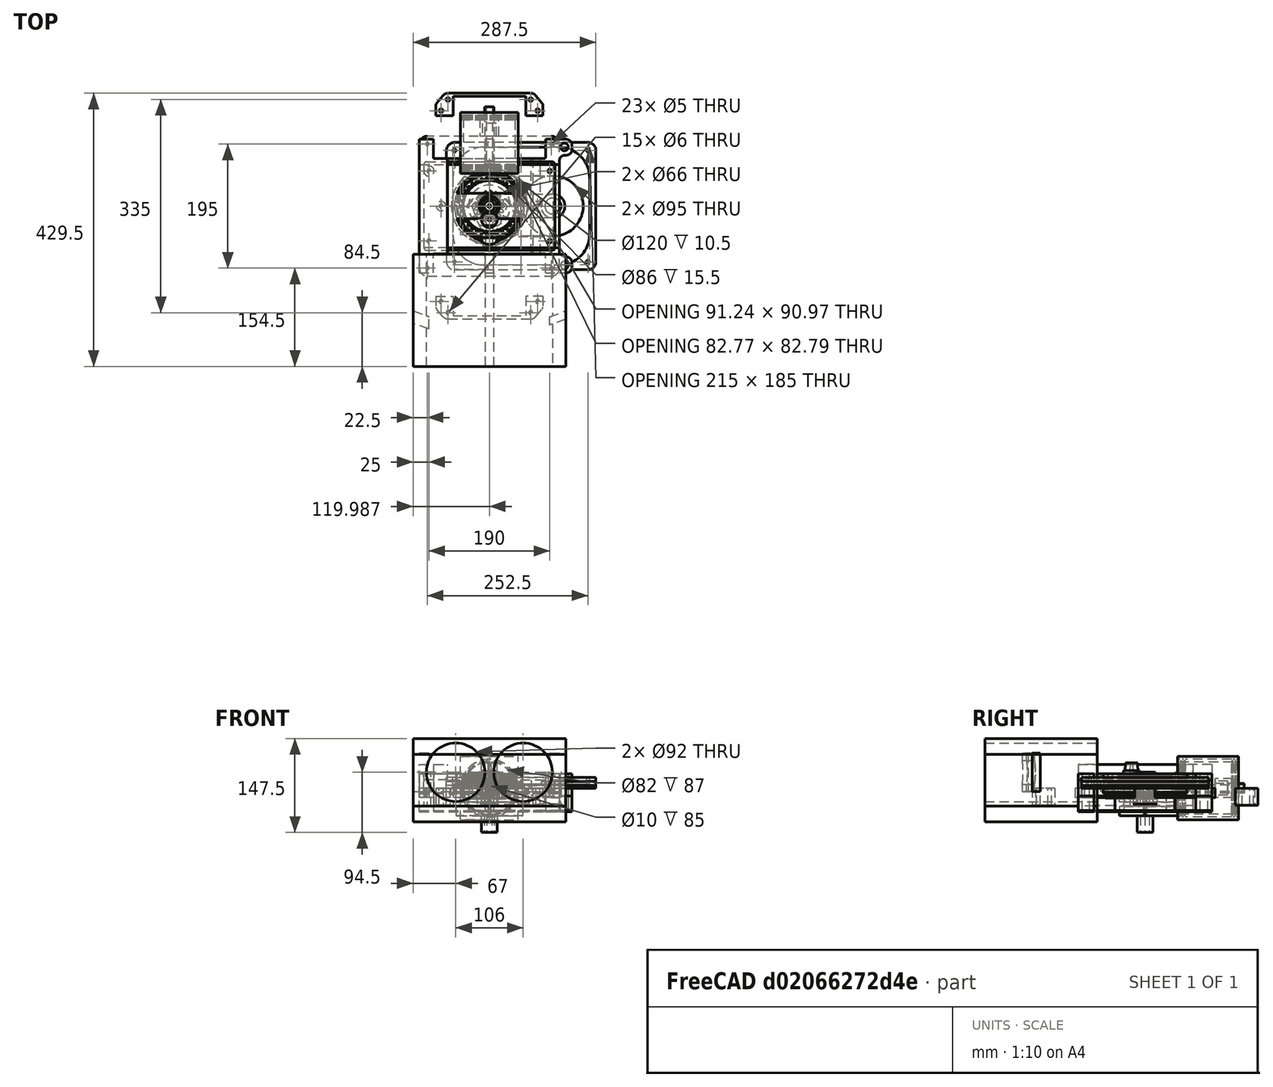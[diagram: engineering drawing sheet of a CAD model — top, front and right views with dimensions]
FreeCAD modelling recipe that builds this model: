
FCSTD DOCUMENT  (FreeCAD 1.0R38641 +678 (Git))
Label: assm4_X_at_Tusi_stirling
License: All rights reserved
objects: Sketcher::SketchObject×46, PartDesign::Body×30, PartDesign::Pad×28, PartDesign::CoordinateSystem×26, App::Link×23, PartDesign::Pocket×19, Mesh::Feature×12, PartDesign::FeatureBase×8, PartDesign::SubtractiveCylinder×5, App::DocumentObjectGroup×4, PartDesign::AdditiveCylinder×4, PartDesign::Boolean×2, Part::Extrusion×2, Part::FeaturePython×2, PartDesign::Hole×2, PartDesign::Fillet×2, App::FeaturePython×1, Spreadsheet::Sheet×1, Part::MultiFuse×1, PartDesign::Chamfer×1, +3 more types
note: 359 computed .brp shape members not serialized (recipe doc carries the construction recipe); baked Part::Feature solids carry a one-line shape summary decoded from their .brp

FEATURE [PartDesign::CoordinateSystem] LCS_Origin
  AttacherType = Attacher::AttachEngine3D
  AttachmentSupport = -> [X_Axis]
  MapMode = 2
FEATURE [App::DocumentObjectGroup] Constraints
FEATURE [App::FeaturePython] Variables  # WARN: FeaturePython — macro-defined, semantics opaque (R4)
  Crank_Angle = 0
  Type = App::PropertyContainer
FEATURE [App::DocumentObjectGroup] Configurations
FEATURE [Sketcher::SketchObject] Sketch002
  ArcFitTolerance = 0
  AttachmentSupport = -> [XY_Plane006]
  FullyConstrained = true
  MakeInternals = false
  MapMode = 5
  expr: Constraints[0] = <<Dim_table>>.crank_dia1
  expr: Constraints[20] = <<Dim_table>>.hex_size
  sketch-geometry (8):
    g0: Circle CenterX=0 CenterY=0 CenterZ=0 NormalX=0 NormalY=0 NormalZ=1 AngleXU=0 Radius=12.5
    g1: LineSegment StartX=4.04145 StartY=7 StartZ=0 EndX=-4.04145 EndY=7 EndZ=0
    g2: LineSegment StartX=-4.04145 StartY=7 StartZ=0 EndX=-8.0829 EndY=0 EndZ=0
    g3: LineSegment StartX=-8.0829 StartY=0 StartZ=0 EndX=-4.04145 EndY=-7 EndZ=0
    g4: LineSegment StartX=-4.04145 StartY=-7 StartZ=0 EndX=4.04145 EndY=-7 EndZ=0
    g5: LineSegment StartX=4.04145 StartY=-7 StartZ=0 EndX=8.0829 EndY=-9e-16 EndZ=0
    g6: LineSegment StartX=8.0829 StartY=-9e-16 StartZ=0 EndX=4.04145 EndY=7 EndZ=0
    g7: Circle [constr] CenterX=0 CenterY=0 CenterZ=0 NormalX=0 NormalY=0 NormalZ=1 AngleXU=0 Radius=8.0829
  constraints (18):
    c: Diameter(g0) = 25
    c: Coincident(g1,g2)
    c: Coincident(g2,g3)
    c: Coincident(g3,g4)
    c: Coincident(g4,g5)
    c: Coincident(g5,g6)
    c: Coincident(g6,g1)
    c: Equal(g1, g2-g6) x5
    c: PointOnObject(g1,g7)
    c: PointOnObject(g2,g7)
    c: PointOnObject(g3,g7)
    c: PointOnObject(g4,g7)
    c: PointOnObject(g5,g7)
    c: PointOnObject(g6,g7)
    c: Coincident(g7,g0)
    c: Horizontal(g1)
    c: DistanceY(g3,g1) = 14
    c: Coincident(g0,g-1)
FEATURE [PartDesign::Pad] Pad005
  Direction = (0,0,1)
  Length = 26
  Length2 = 10
  Profile = -> Sketch002
  ReferenceAxis = -> Sketch002 [N_Axis]
  Reversed = true
  Suppressed = false
  Type = 0
FEATURE [PartDesign::Body] Body005  label="Шейка коренная"
  AllowCompound = false
  Group = -> [Sketch002,Pad005]
  Origin = -> Origin006
  Placement = pos=(0,0,47) rot=(0,0,1;0rad)
  Tip = -> Pad005
FEATURE [PartDesign::FeatureBase] Clone004
  BaseFeature = -> Body005
  Suppressed = false
FEATURE [PartDesign::Body] Body054
  AllowCompound = false
  Group = -> [Clone004]
  Origin = -> Origin055
  Placement = pos=(0,0,-43.5) rot=(0,0,1;0rad)
  Tip = -> Clone004
FEATURE [Sketcher::SketchObject] Sketch003
  ArcFitTolerance = 0
  AttachmentSupport = -> [XY_Plane005]
  FullyConstrained = true
  MakeInternals = false
  MapMode = 5
  expr: Constraints[17] = <<Dim_table>>.fillet_r
  expr: Constraints[18] = <<Dim_table>>.fillet_r
  expr: Constraints[21] = <<Dim_table>>.inter_shaft_len - <<Dim_table>>.zazor
  expr: Constraints[23] = <<Dim_table>>.axle_hole_dia
  expr: Constraints[25] = 70
  expr: Constraints[26] = <<Dim_table>>.crank_dia2 * 1.5
  expr: Constraints[27] = <<Dim_table>>.crank_len
  sketch-geometry (14):
    g0: ArcOfCircle CenterX=0 CenterY=0 CenterZ=0 NormalX=0 NormalY=0 NormalZ=1 AngleXU=0 Radius=52.5 StartAngle=0.0396143 EndAngle=3.10198
    g1: ArcOfCircle CenterX=-1.2e-15 CenterY=-21.25 CenterZ=0 NormalX=0 NormalY=0 NormalZ=1 AngleXU=0 Radius=18.75 StartAngle=3.49066 EndAngle=5.93412
    g2: LineSegment [constr] StartX=-17.6192 StartY=-27.6629 StartZ=0 EndX=17.6192 EndY=-27.6629 EndZ=0
    g3: LineSegment StartX=-50.4604 StartY=0 StartZ=0 EndX=-29.0881 EndY=0 EndZ=0
    g4: LineSegment StartX=-27.2087 StartY=-1.31596 StartZ=0 EndX=-17.6192 EndY=-27.6629 EndZ=0
    g5: LineSegment StartX=17.6192 StartY=-27.6629 StartZ=0 EndX=27.2087 EndY=-1.31596 EndZ=0
    g6: LineSegment StartX=29.0881 StartY=-7e-16 StartZ=0 EndX=50.4604 EndY=-7e-16 EndZ=0
    g7: ArcOfCircle CenterX=-29.0881 CenterY=-2 CenterZ=0 NormalX=0 NormalY=0 NormalZ=1 AngleXU=0 Radius=2 StartAngle=0.349066 EndAngle=1.5708
    g8: ArcOfCircle CenterX=29.0881 CenterY=-2 CenterZ=0 NormalX=0 NormalY=0 NormalZ=1 AngleXU=0 Radius=2 StartAngle=1.5708 EndAngle=2.79253
    g9: ArcOfCircle CenterX=50.4604 CenterY=2 CenterZ=0 NormalX=0 NormalY=0 NormalZ=1 AngleXU=0 Radius=2 StartAngle=4.71239 EndAngle=6.3228
    g10: ArcOfCircle CenterX=-50.4604 CenterY=2 CenterZ=0 NormalX=0 NormalY=0 NormalZ=1 AngleXU=0 Radius=2 StartAngle=3.10198 EndAngle=4.71239
    g11: Circle [constr] CenterX=0 CenterY=0 CenterZ=0 NormalX=0 NormalY=0 NormalZ=1 AngleXU=0 Radius=49.75
    g12: Circle CenterX=0 CenterY=0 CenterZ=0 NormalX=0 NormalY=0 NormalZ=1 AngleXU=0 Radius=2.5
    g13: Circle [constr] CenterX=-1.2e-15 CenterY=-21.25 CenterZ=0 NormalX=0 NormalY=0 NormalZ=1 AngleXU=0 Radius=2.5
  constraints (31):
    c: Coincident(g2,g1)
    c: Coincident(g2,g1)
    c: Horizontal(g2)
    c: Horizontal(g3)
    c: Horizontal(g6)
    c: Tangent(g4,g1) = -1.5708
    c: Tangent(g5,g1) = -1.5708
    c: Tangent(g3,g7) = 1.5708
    c: Tangent(g4,g7) = 1.5708
    c: Tangent(g6,g8) = 1.5708
    c: Tangent(g5,g8) = 1.5708
    c: Tangent(g6,g9) = -1.5708
    c: Tangent(g0,g9) = -1.5708
    c: Tangent(g0,g10) = -1.5708
    c: Tangent(g3,g10) = -1.5708
    c: Symmetric(g7,g8,g-2)
    c: Symmetric(g10,g9,g-2)
    c: Radius(g10) = 2
    c: Radius(g7) = 2
    c: Coincident(g0,g-1)
    c: Coincident(g11,g0)
    c: Diameter(g11) = 99.5
    c: Coincident(g12,g11)
    c: Diameter(g12) = 5
    c: Diameter(g0) = 105
    c: Angle(g5) = 1.22173
    c: Diameter(g1) = 37.5
    c: DistanceY(g1,g12) = 21.25
    c: PointOnObject(g3,g-1)
    c: Coincident(g13,g1)
    c: Equal(g13,g12)
FEATURE [PartDesign::Pad] Pad004
  Direction = (0,0,1)
  Length = 15
  Length2 = 10
  Profile = -> Sketch003
  ReferenceAxis = -> Sketch003 [N_Axis]
  Suppressed = false
  Type = 0
FEATURE [PartDesign::Body] Body004  label="Щека"
  AllowCompound = false
  Group = -> [Sketch003,Pad004]
  Origin = -> Origin005
  Placement = pos=(0,0,12.5) rot=(0,0,1;0rad)
  Tip = -> Pad004
FEATURE [PartDesign::FeatureBase] Clone005
  BaseFeature = -> Body004
  Suppressed = false
FEATURE [PartDesign::Body] Body055
  AllowCompound = false
  Group = -> [Clone005]
  Origin = -> Origin056
  Placement = pos=(0,0,-43.5) rot=(0,0,1;0rad)
  Tip = -> Clone005
FEATURE [Sketcher::SketchObject] Sketch004
  ArcFitTolerance = 0
  AttachmentSupport = -> [XY_Plane004]
  FullyConstrained = true
  MakeInternals = false
  MapMode = 5
  expr: Constraints[0] = <<Dim_table>>.crank_dia2
  expr: Constraints[2] = <<Dim_table>>.crank_len
  expr: Constraints[4] = <<Dim_table>>.axle_hole_dia
  sketch-geometry (2):
    g0: Circle CenterX=0 CenterY=-21.25 CenterZ=0 NormalX=0 NormalY=0 NormalZ=1 AngleXU=0 Radius=12.5
    g1: Circle CenterX=0 CenterY=-21.25 CenterZ=0 NormalX=0 NormalY=0 NormalZ=1 AngleXU=0 Radius=2.5
  constraints (5):
    c: Diameter(g0) = 25
    c: PointOnObject(g0,g-2)
    c: DistanceY(g0,g-1) = 21.25
    c: Coincident(g1,g0)
    c: Diameter(g1) = 5
FEATURE [PartDesign::Pad] Pad003
  Direction = (0,0,1)
  Length = 63
  Length2 = 0
  Profile = -> Sketch004
  ReferenceAxis = -> Sketch004 [N_Axis]
  Suppressed = false
  Type = 0
FEATURE [Sketcher::SketchObject] Sketch005
  ArcFitTolerance = 0
  AttachmentSupport = -> [XY_Plane002]
  FullyConstrained = true
  MakeInternals = false
  MapMode = 5
  expr: Constraints[1] = <<Dim_table>>.crank_dia2 + <<Dim_table>>.zazor
  expr: Constraints[26] = 10
  expr: Constraints[27] = <<Dim_table>>.ecc_dia * 0.8
  expr: Constraints[28] = <<Dim_table>>.crank_dia2 * 2
  expr: Constraints[2] = <<Dim_table>>.ecc_dia + <<Dim_table>>.roller_dia
  expr: Constraints[3] = <<Dim_table>>.crank_len
  sketch-geometry (14):
    g0: Circle CenterX=0 CenterY=-21.25 CenterZ=0 NormalX=0 NormalY=0 NormalZ=1 AngleXU=0 Radius=41.5
    g1: Circle CenterX=0 CenterY=0 CenterZ=0 NormalX=0 NormalY=0 NormalZ=1 AngleXU=0 Radius=12.75
    g2: ArcOfCircle CenterX=0 CenterY=-21.25 CenterZ=0 NormalX=0 NormalY=0 NormalZ=1 AngleXU=0 Radius=32 StartAngle=3.32205 EndAngle=4.38515
    g3: ArcOfCircle CenterX=0 CenterY=-21.25 CenterZ=0 NormalX=0 NormalY=0 NormalZ=1 AngleXU=0 Radius=32 StartAngle=5.03963 EndAngle=6.10273
    g4: LineSegment StartX=-5 StartY=-27.5681 StartZ=0 EndX=-5 EndY=-47.7641 EndZ=0
    g5: LineSegment StartX=5 StartY=-27.5681 StartZ=0 EndX=5 EndY=-47.7641 EndZ=0
    g6: ArcOfCircle CenterX=0 CenterY=0 CenterZ=0 NormalX=0 NormalY=0 NormalZ=1 AngleXU=0 Radius=25 StartAngle=3.98424 EndAngle=4.39683
    g7: ArcOfCircle CenterX=0 CenterY=0 CenterZ=0 NormalX=0 NormalY=0 NormalZ=1 AngleXU=0 Radius=25 StartAngle=5.02794 EndAngle=5.44053
    g8: ArcOfCircle CenterX=-22.6265 CenterY=-25.3779 CenterZ=0 NormalX=0 NormalY=0 NormalZ=1 AngleXU=0 Radius=9 StartAngle=0.842651 EndAngle=3.32205
    g9: ArcOfCircle CenterX=22.6265 CenterY=-25.3779 CenterZ=0 NormalX=0 NormalY=0 NormalZ=1 AngleXU=0 Radius=9 StartAngle=6.10273 EndAngle=8.58213
    g10: ArcOfCircle CenterX=-9 CenterY=-47.7641 CenterZ=0 NormalX=0 NormalY=0 NormalZ=1 AngleXU=0 Radius=4 StartAngle=4.38515 EndAngle=6.28319
    g11: ArcOfCircle CenterX=9 CenterY=-47.7641 CenterZ=0 NormalX=0 NormalY=0 NormalZ=1 AngleXU=0 Radius=4 StartAngle=3.14159 EndAngle=5.03963
    g12: ArcOfCircle CenterX=-9 CenterY=-27.5681 CenterZ=0 NormalX=0 NormalY=0 NormalZ=1 AngleXU=0 Radius=4 StartAngle=0 EndAngle=1.25524
    g13: ArcOfCircle CenterX=9 CenterY=-27.5681 CenterZ=0 NormalX=0 NormalY=0 NormalZ=1 AngleXU=0 Radius=4 StartAngle=1.88635 EndAngle=3.14159
  constraints (32):
    c: PointOnObject(g0,g-2)
    c: Diameter(g1) = 25.5
    c: Diameter(g0) = 83
    c: Distance(g1,g0) = 21.25
    c: Coincident(g1,g-1)
    c: Coincident(g2,g0)
    c: Coincident(g3,g0)
    c: Equal(g2,g3)
    c: Vertical(g4)
    c: Coincident(g6,g1)
    c: Coincident(g7,g1)
    c: Tangent(g2,g8) = -1.5708
    c: Tangent(g6,g8) = 1.5708
    c: Tangent(g7,g9) = 1.5708
    c: Tangent(g3,g9) = -1.5708
    c: Tangent(g2,g10) = -1.5708
    c: Tangent(g4,g10) = 1.5708
    c: Tangent(g5,g11) = -1.5708
    c: Tangent(g3,g11) = -1.5708
    c: Tangent(g6,g12) = 1.5708
    c: Tangent(g4,g12) = 1.5708
    c: Tangent(g5,g13) = -1.5708
    c: Tangent(g7,g13) = 1.5708
    c: Symmetric(g12,g13,g-2)
    c: Symmetric(g10,g11,g-2)
    c: Symmetric(g8,g9,g-2)
    c: DistanceX(g4,g5) = 10
    c: Diameter(g2) = 64
    c: Diameter(g6) = 50
    c: Radius(g10) = 4
    c: Equal(g10,g12)
    c: Radius(g8) = 9
FEATURE [PartDesign::CoordinateSystem] Eccentr
  AttacherType = Attacher::AttachEngine3D
  AttachmentOffset = pos=(0,0,0) rot=(0,0,1;1.5708rad)
  AttachmentSupport = -> [Sketch005]
  MapMode = 11
  Placement = pos=(0,0,0) rot=(0,0,1;3.14159rad)
FEATURE [PartDesign::Pad] Pad001
  Direction = (0,0,1)
  Length = 16.5
  Length2 = 0
  Profile = -> Sketch005
  ReferenceAxis = -> Sketch005 [N_Axis]
  Reversed = true
  Suppressed = false
  Type = 0
  expr: Length = <<Dim_table>>.ecc_hei
FEATURE [Sketcher::SketchObject] Sketch007
  ArcFitTolerance = 0
  AttachmentSupport = -> [XY_Plane003]
  FullyConstrained = true
  MakeInternals = false
  MapMode = 5
  expr: Constraints[15] = <<Dim_table>>.ecc_dia * 1.3
  expr: Constraints[17] = <<Dim_table>>.ecc_dia * 0.8
  expr: Constraints[1] = <<Dim_table>>.ecc_dia + 2 * <<Dim_table>>.roller_dia
  sketch-geometry (15):
    g0: Circle CenterX=0 CenterY=0 CenterZ=0 NormalX=0 NormalY=0 NormalZ=1 AngleXU=0 Radius=43
    g1: ArcOfCircle CenterX=0 CenterY=0 CenterZ=0 NormalX=0 NormalY=0 NormalZ=1 AngleXU=0 Radius=52 StartAngle=1.86916 EndAngle=3.14159
    g2: ArcOfCircle CenterX=0 CenterY=0 CenterZ=0 NormalX=0 NormalY=0 NormalZ=1 AngleXU=0 Radius=52 StartAngle=0 EndAngle=1.27243
    g3: LineSegment StartX=-11.8314 StartY=53.6134 StartZ=0 EndX=-10 EndY=64 EndZ=0
    g4: LineSegment StartX=-10 StartY=64 StartZ=0 EndX=10 EndY=64 EndZ=0
    g5: LineSegment StartX=10 StartY=64 StartZ=0 EndX=11.8314 EndY=53.6134 EndZ=0
    g6: ArcOfCircle CenterX=-16.7555 CenterY=54.4817 CenterZ=0 NormalX=0 NormalY=0 NormalZ=1 AngleXU=0 Radius=5 StartAngle=5.01075 EndAngle=6.10865
    g7: ArcOfCircle CenterX=16.7555 CenterY=54.4817 CenterZ=0 NormalX=0 NormalY=0 NormalZ=1 AngleXU=0 Radius=5 StartAngle=3.31613 EndAngle=4.41403
    g8: ArcOfCircle CenterX=-2.7e-15 CenterY=2.94305e-05 CenterZ=0 NormalX=0 NormalY=0 NormalZ=1 AngleXU=0 Radius=52 StartAngle=3.14159 EndAngle=4.41403
    g9: ArcOfCircle CenterX=-16.7555 CenterY=-54.4817 CenterZ=0 NormalX=0 NormalY=0 NormalZ=1 AngleXU=0 Radius=5 StartAngle=0.174533 EndAngle=1.27243
    g10: LineSegment StartX=-11.8314 StartY=-53.6134 StartZ=0 EndX=-10 EndY=-64 EndZ=0
    g11: LineSegment StartX=-10 StartY=-64 StartZ=0 EndX=10 EndY=-64 EndZ=0
    g12: LineSegment StartX=10 StartY=-64 StartZ=0 EndX=11.8314 EndY=-53.6134 EndZ=0
    g13: ArcOfCircle CenterX=16.7555 CenterY=-54.4817 CenterZ=0 NormalX=0 NormalY=0 NormalZ=1 AngleXU=0 Radius=5 StartAngle=1.86916 EndAngle=2.96706
    g14: ArcOfCircle CenterX=-2.7e-15 CenterY=2.94305e-05 CenterZ=0 NormalX=0 NormalY=0 NormalZ=1 AngleXU=0 Radius=52 StartAngle=5.01075 EndAngle=6.28318
  constraints (36):
    c: Coincident(g0,g-1)
    c: Diameter(g0) = 86
    c: Coincident(g1,g0)
    c: Coincident(g2,g0)
    c: Equal(g1,g2)
    c: Coincident(g3,g4)
    c: Coincident(g4,g5)
    c: Tangent(g1,g6) = 1.5708
    c: Tangent(g3,g6) = -1.5708
    c: Tangent(g5,g7) = -1.5708
    c: Tangent(g2,g7) = 1.5708
    c: Symmetric(g6,g7,g-2)
    c: Symmetric(g3,g4,g-2)
    c: PointOnObject(g1,g-1)
    c: PointOnObject(g2,g-1)
    c: Diameter(g1) = 104
    c: Distance(g4,g4) = 20
    c: DistanceY(g0,g4) = 64
    c: Radius(g6) = 5
    c: Angle(g3,g-2) = 0.174533
    c: Equal(g8,g14)
    c: Coincident(g10,g11)
    c: Coincident(g11,g12)
    c: Tangent(g8,g9) = 1.5708
    c: Tangent(g10,g9) = 1.5708
    c: Tangent(g12,g13) = 1.5708
    c: Tangent(g14,g13) = 1.5708
    c: Equal(g8,g1)
    c: Equal(g13,g7)
    c: Symmetric(g9,g13,g-2)
    c: Symmetric(g11,g4,g-1)
    c: Symmetric(g10,g11,g-2)
    c: Parallel(g12,g3)
    c: Coincident(g8,g1)
    c: Coincident(g14,g2)
    c: Coincident(g8,g14)
FEATURE [PartDesign::Pad] Pad002
  Direction = (0,0,1)
  Length = 15.5
  Length2 = 10
  Midplane = true
  Profile = -> Sketch007
  ReferenceAxis = -> Sketch007 [N_Axis]
  Suppressed = false
  Type = 0
  expr: Length = <<Dim_table>>.ecc_hei - 1
FEATURE [PartDesign::CoordinateSystem] Shtok
  AttacherType = Attacher::AttachEngine3D
  AttachmentSupport = -> [Pad002]
  MapMode = 45
  Placement = pos=(-7.2e-15,2.69855e-05,-3e-16) rot=(0,0,1;0rad)
FEATURE [Sketcher::SketchObject] Main
  ArcFitTolerance = 0
  AttachmentSupport = -> [LCS_Origin]
  FullyConstrained = true
  MakeInternals = false
  MapMode = 5
  expr: Constraints[19] = <<Dim_table>>.piston_dia
  expr: Constraints[1] = <<Variables>>.Crank_Angle
  expr: Constraints[20] = <<Dim_table>>.piston_hei
  expr: Constraints[22] = <<Dim_table>>.ecc_dia
  expr: Constraints[23] = -<<Variables>>.Crank_Angle
  expr: Constraints[2] = <<Dim_table>>.crank_len
  expr: Constraints[35] = <<Dim_table>>.rod_len
  expr: Constraints[5] = <<Dim_table>>.crank_dia1
  expr: Constraints[6] = <<Dim_table>>.crank_dia2
  expr: Constraints[74] = <<Dim_table>>.crank_len / 2
  expr: Constraints[77] = <<Dim_table>>.crank_len / 2
  expr: Constraints[8] = <<Dim_table>>.crank_len * 2
  sketch-geometry (29):
    g0: LineSegment StartX=0 StartY=0 StartZ=0 EndX=-2.63e-14 EndY=21.25 EndZ=0
    g1: Circle [constr] CenterX=0 CenterY=0 CenterZ=0 NormalX=0 NormalY=0 NormalZ=1 AngleXU=0 Radius=12.5
    g2: Circle CenterX=-2.63e-14 CenterY=21.25 CenterZ=0 NormalX=0 NormalY=0 NormalZ=1 AngleXU=0 Radius=12.5
    g3: LineSegment [constr] StartX=-4.66e-14 StartY=1.23e-14 StartZ=0 EndX=-2.5e-15 EndY=42.5 EndZ=0
    g4: LineSegment StartX=-36 StartY=221.5 StartZ=0 EndX=36 EndY=221.5 EndZ=0
    g5: LineSegment StartX=36 StartY=221.5 StartZ=0 EndX=36 EndY=182.5 EndZ=0
    g6: LineSegment StartX=36 StartY=182.5 StartZ=0 EndX=-36 EndY=182.5 EndZ=0
    g7: LineSegment StartX=-36 StartY=182.5 StartZ=0 EndX=-36 EndY=221.5 EndZ=0
    g8: LineSegment [constr] StartX=-36 StartY=182.5 StartZ=0 EndX=36 EndY=221.5 EndZ=0
    g9: Circle CenterX=-2.5e-15 CenterY=42.5 CenterZ=0 NormalX=0 NormalY=0 NormalZ=1 AngleXU=0 Radius=40
    g10: LineSegment StartX=140 StartY=36 StartZ=0 EndX=140 EndY=-36 EndZ=0
    g11: LineSegment StartX=140 StartY=-36 StartZ=0 EndX=179 EndY=-36 EndZ=0
    g12: LineSegment StartX=179 StartY=-36 StartZ=0 EndX=179 EndY=36 EndZ=0
    g13: LineSegment StartX=179 StartY=36 StartZ=0 EndX=140 EndY=36 EndZ=0
    g14: LineSegment StartX=-2.5e-15 StartY=182.5 StartZ=0 EndX=-2.5e-15 EndY=42.5 EndZ=0
    g15: LineSegment [constr] StartX=140 StartY=1.23e-14 StartZ=0 EndX=-5.68e-14 EndY=1.23e-14 EndZ=0
    g16: LineSegment StartX=-36 StartY=-136.5 StartZ=0 EndX=36 EndY=-136.5 EndZ=0
    g17: LineSegment StartX=36 StartY=-136.5 StartZ=0 EndX=36 EndY=-97.5 EndZ=0
    g18: LineSegment StartX=36 StartY=-97.5 StartZ=0 EndX=-36 EndY=-97.5 EndZ=0
    g19: LineSegment StartX=-36 StartY=-97.5 StartZ=0 EndX=-36 EndY=-136.5 EndZ=0
    g20: LineSegment [constr] StartX=-2.5e-15 StartY=-97.5 StartZ=0 EndX=-2.5e-15 EndY=42.5 EndZ=0
    g21: LineSegment StartX=-140 StartY=36 StartZ=0 EndX=-140 EndY=-36 EndZ=0
    g22: LineSegment StartX=-140 StartY=-36 StartZ=0 EndX=-179 EndY=-36 EndZ=0
    g23: LineSegment StartX=-179 StartY=-36 StartZ=0 EndX=-179 EndY=36 EndZ=0
    g24: LineSegment StartX=-179 StartY=36 StartZ=0 EndX=-140 EndY=36 EndZ=0
    g25: LineSegment [constr] StartX=-140 StartY=1.23e-14 StartZ=0 EndX=-5.68e-14 EndY=1.23e-14 EndZ=0
    g26: Circle CenterX=-4.66e-14 CenterY=1.23e-14 CenterZ=0 NormalX=0 NormalY=0 NormalZ=1 AngleXU=0 Radius=40
    g27: LineSegment StartX=-2.63e-14 StartY=21.25 StartZ=0 EndX=-1.05e-14 EndY=31.875 EndZ=0
    g28: LineSegment StartX=-4.66e-14 StartY=1.23e-14 StartZ=0 EndX=10.625 EndY=1.23e-14 EndZ=0
  constraints (78):
    c: Coincident(g0,g-1)
    c: Angle(g0,g-2) = 0
    c: Distance(g0) = 21.25
    c: Coincident(g1,g0)
    c: Coincident(g2,g0)
    c: Diameter(g1) = 25
    c: Diameter(g2) = 25
    c: Symmetric(g3,g3,g0)
    c: Distance(g3) = 42.5
    c: Coincident(g4,g5)
    c: Coincident(g5,g6)
    c: Coincident(g6,g7)
    c: Coincident(g7,g4)
    c: Horizontal(g4)
    c: Horizontal(g6)
    c: Vertical(g5)
    c: Vertical(g7)
    c: Coincident(g8,g6)
    c: Coincident(g8,g4)
    c: Distance(g4) = 72
    c: Distance(g5) = 39
    c: Coincident(g9,g3)
    c: Diameter(g9) = 80
    c: Angle(g3,g-2) = 0
    c: Coincident(g10,g11)
    c: Coincident(g11,g12)
    c: Coincident(g12,g13)
    c: Coincident(g13,g10)
    c: Vertical(g10)
    c: Vertical(g12)
    c: Horizontal(g11)
    c: Horizontal(g13)
    c: Vertical(g14)
    c: Symmetric(g6,g5,g14)
    c: Coincident(g14,g3)
    c: Distance(g14,g14) = 140
    c: Symmetric(g10,g10,g15)
    c: Horizontal(g15)
    c: Equal(g5,g13)
    c: Equal(g4,g12)
    c: Equal(g14,g15)
    c: Coincident(g3,g15)
    c: Coincident(g16,g17)
    c: Coincident(g17,g18)
    c: Coincident(g18,g19)
    c: Coincident(g19,g16)
    c: Horizontal(g16)
    c: Horizontal(g18)
    c: Vertical(g17)
    c: Vertical(g19)
    c: Vertical(g20)
    c: Symmetric(g18,g17,g20)
    c: Equal(g18,g12)
    c: Equal(g17,g13)
    c: Equal(g20,g15)
    c: Coincident(g3,g20)
    c: Coincident(g21,g22)
    c: Coincident(g22,g23)
    c: Coincident(g23,g24)
    c: Coincident(g24,g21)
    c: Vertical(g21)
    c: Vertical(g23)
    c: Horizontal(g22)
    c: Horizontal(g24)
    c: Symmetric(g21,g21,g25)
    c: Horizontal(g25)
    c: Equal(g24,g13)
    c: Equal(g23,g12)
    c: Equal(g25,g15)
    c: Coincident(g3,g25)
    c: Coincident(g26,g3)
    c: Equal(g26,g9)
    c: Coincident(g27,g0)
    c: PointOnObject(g27,g3)
    c: Distance(g27,g27) = 10.625
    c: Coincident(g28,g3)
    c: PointOnObject(g28,g15)
    c: DistanceX(g28,g28) = 10.625
FEATURE [Sketcher::SketchObject] Sketch021
  ArcFitTolerance = 0
  AttachmentSupport = -> [XY_Plane062]
  FullyConstrained = false
  MakeInternals = false
  MapMode = 5
  sketch-geometry (30):
    g0: LineSegment [constr] StartX=-110 StartY=225 StartZ=0 EndX=110 EndY=225 EndZ=0
    g1: LineSegment [constr] StartX=110 StartY=225 StartZ=0 EndX=110 EndY=-225 EndZ=0
    g2: LineSegment [constr] StartX=110 StartY=-225 StartZ=0 EndX=-110 EndY=-225 EndZ=0
    g3: LineSegment [constr] StartX=-110 StartY=-225 StartZ=0 EndX=-110 EndY=225 EndZ=0
    g4: LineSegment [constr] StartX=-110 StartY=225 StartZ=0 EndX=-110 EndY=105 EndZ=0
    g5: LineSegment [constr] StartX=-110 StartY=105 StartZ=0 EndX=110 EndY=105 EndZ=0
    g6: LineSegment [constr] StartX=110 StartY=105 StartZ=0 EndX=110 EndY=225 EndZ=0
    g7: LineSegment [constr] StartX=-110 StartY=-225 StartZ=0 EndX=-110 EndY=-105 EndZ=0
    g8: LineSegment StartX=-110 StartY=-105 StartZ=0 EndX=110 EndY=-105 EndZ=0
    g9: LineSegment [constr] StartX=110 StartY=-105 StartZ=0 EndX=110 EndY=-225 EndZ=0
    g10: LineSegment [constr] StartX=-110 StartY=-105 StartZ=0 EndX=-110 EndY=105 EndZ=0
    g11: LineSegment StartX=110 StartY=105 StartZ=0 EndX=-110 EndY=105 EndZ=0
    g12: Circle CenterX=0 CenterY=0 CenterZ=0 NormalX=0 NormalY=0 NormalZ=1 AngleXU=0 Radius=33
    g13: LineSegment StartX=-110 StartY=105 StartZ=0 EndX=-110 EndY=0 EndZ=0
    g14: LineSegment [constr] StartX=110 StartY=-105 StartZ=0 EndX=110 EndY=105 EndZ=0
    g15: LineSegment StartX=110 StartY=105 StartZ=0 EndX=120.902 EndY=105 EndZ=0
    g16: LineSegment StartX=130 StartY=95.9016 StartZ=0 EndX=130 EndY=89.0984 EndZ=0
    g17: LineSegment StartX=120.902 StartY=80 StartZ=0 EndX=119.098 EndY=80 EndZ=0
    g18: ArcOfCircle CenterX=120.902 CenterY=95.9016 CenterZ=0 NormalX=0 NormalY=0 NormalZ=1 AngleXU=0 Radius=9.09838 StartAngle=0 EndAngle=1.5708
    g19: ArcOfCircle CenterX=120.902 CenterY=89.0984 CenterZ=0 NormalX=0 NormalY=0 NormalZ=1 AngleXU=0 Radius=9.09838 StartAngle=4.71239 EndAngle=6.28319
    g20: LineSegment StartX=110 StartY=70.9016 StartZ=0 EndX=110 EndY=0 EndZ=0
    g21: ArcOfCircle CenterX=119.098 CenterY=70.9016 CenterZ=0 NormalX=0 NormalY=0 NormalZ=1 AngleXU=0 Radius=9.09838 StartAngle=1.5708 EndAngle=3.14159
    g22: LineSegment StartX=110 StartY=-105 StartZ=0 EndX=120.902 EndY=-105 EndZ=0
    g23: LineSegment StartX=130 StartY=-95.9016 StartZ=0 EndX=130 EndY=-89.0984 EndZ=0
    g24: LineSegment StartX=120.902 StartY=-80 StartZ=0 EndX=119.098 EndY=-80 EndZ=0
    g25: ArcOfCircle CenterX=120.902 CenterY=-95.9016 CenterZ=0 NormalX=0 NormalY=0 NormalZ=1 AngleXU=0 Radius=9.09838 StartAngle=4.71239 EndAngle=6.28319
    g26: ArcOfCircle CenterX=120.902 CenterY=-89.0984 CenterZ=0 NormalX=0 NormalY=0 NormalZ=1 AngleXU=0 Radius=9.09838 StartAngle=0 EndAngle=1.5708
    g27: LineSegment StartX=110 StartY=-70.9016 StartZ=0 EndX=110 EndY=0 EndZ=0
    g28: ArcOfCircle CenterX=119.098 CenterY=-70.9016 CenterZ=0 NormalX=0 NormalY=0 NormalZ=1 AngleXU=0 Radius=9.09838 StartAngle=3.14159 EndAngle=4.71239
    g29: LineSegment StartX=-110 StartY=-105 StartZ=0 EndX=-110 EndY=0 EndZ=0
  constraints (61):
    c: Coincident(g0,g1)
    c: Coincident(g1,g2)
    c: Coincident(g2,g3)
    c: Coincident(g3,g0)
    c: Horizontal(g2)
    c: Vertical(g1)
    c: Symmetric(g0,g0,g-2)
    c: Symmetric(g0,g2,g-1)
    c: Coincident(g0,g4)
    c: PointOnObject(g4,g3)
    c: Coincident(g4,g5)
    c: PointOnObject(g5,g1)
    c: Horizontal(g5)
    c: Coincident(g6,g0)
    c: Coincident(g2,g7)
    c: PointOnObject(g7,g3)
    c: Horizontal(g8)
    c: Coincident(g9,g2)
    c: Equal(g9,g6)
    c: DistanceX(g2,g2) = 220
    c: DistanceY(g3,g3) = 450
    c: DistanceY(g9,g9) = 120
    c: Coincident(g10,g4)
    c: Coincident(g11,g10)
    c: Diameter(g12) = 66
    c: PointOnObject(g13,g-1)
    c: Vertical(g13)
    c: Vertical(g10)
    c: Vertical(g6)
    c: Coincident(g8,g9)
    c: Coincident(g8,g7)
    c: Coincident(g11,g5)
    c: Symmetric(g8,g11,g-1)
    c: Horizontal(g15)
    c: Horizontal(g17)
    c: Vertical(g16)
    c: Tangent(g15,g18) = 1.5708
    c: Tangent(g16,g18) = 1.5708
    c: Tangent(g16,g19) = 1.5708
    c: Tangent(g17,g19) = 1.5708
    c: Equal(g19,g18)
    c: Vertical(g20)
    c: Tangent(g17,g21) = -1.5708
    c: Tangent(g20,g21) = -1.5708
    c: Equal(g19,g21)
    c: Vertical(g14)
    c: Horizontal(g22)
    c: Horizontal(g24)
    c: Vertical(g23)
    c: Tangent(g22,g25) = -1.5708
    c: Tangent(g23,g25) = -1.5708
    c: Tangent(g23,g26) = -1.5708
    c: Tangent(g24,g26) = -1.5708
    c: Equal(g26,g25)
    c: Vertical(g27)
    c: Tangent(g24,g28) = 1.5708
    c: Tangent(g27,g28) = 1.5708
    c: Equal(g26,g28)
    c: Coincident(g13,g11)
    c: Coincident(g29,g8)
    c: Coincident(g29,g13)
FEATURE [Sketcher::SketchObject] Sketch022
  ArcFitTolerance = 0
  AttachmentSupport = -> [XY_Plane062]
  FullyConstrained = true
  MakeInternals = false
  MapMode = 5
  sketch-geometry (5):
    g0: LineSegment StartX=-110 StartY=-105 StartZ=0 EndX=-65.5 EndY=-105 EndZ=0
    g1: LineSegment StartX=-65.5 StartY=-105 StartZ=0 EndX=-65.5 EndY=105 EndZ=0
    g2: LineSegment StartX=-65.5 StartY=105 StartZ=0 EndX=-110 EndY=105 EndZ=0
    g3: LineSegment StartX=-110 StartY=105 StartZ=0 EndX=-110 EndY=-105 EndZ=0
    g4: LineSegment [constr] StartX=65.5 StartY=52.9337 StartZ=0 EndX=65.5 EndY=105 EndZ=0
  constraints (14):
    c: Coincident(g0,g1)
    c: Coincident(g1,g2)
    c: Coincident(g2,g3)
    c: Coincident(g3,g0)
    c: Horizontal(g0)
    c: Horizontal(g2)
    c: Vertical(g3)
    c: Vertical(g4)
    c: DistanceX(g1,g4) = 131
    c: Symmetric(g1,g4,g-2)
    c: DistanceY(g1,g1) = 210
    c: DistanceX(g0,g0) = 44.5
    c: Symmetric(g0,g1,g-1)
    c: Block(g4)
FEATURE [PartDesign::Pad] Pad012
  Direction = (0,0,1)
  Length = 35
  Length2 = 12.5
  Profile = -> Sketch021
  ReferenceAxis = -> Sketch021 [N_Axis]
  Reversed = true
  Suppressed = false
  Type = 4
FEATURE [PartDesign::Pad] Pad013
  BaseFeature = -> Pad012
  Direction = (0,0,1)
  Length = 37.5
  Length2 = -12.5
  Profile = -> Sketch022
  ReferenceAxis = -> Sketch022 [N_Axis]
  Suppressed = false
  Type = 4
FEATURE [Sketcher::SketchObject] Sketch_1
  ArcFitTolerance = 0
  FullyConstrained = false
  MakeInternals = false
  sketch-geometry (8):
    g0: Circle [constr] CenterX=0 CenterY=0 CenterZ=0 NormalX=0 NormalY=0 NormalZ=1 AngleXU=0 Radius=65.5
    g1: ArcOfCircle [constr] CenterX=0 CenterY=0 CenterZ=0 NormalX=0 NormalY=0 NormalZ=1 AngleXU=0 Radius=65.5 StartAngle=1.5708 EndAngle=4.71239
    g2: LineSegment StartX=145.598 StartY=65.5 StartZ=0 EndX=0 EndY=65.5 EndZ=0
    g3: LineSegment StartX=145.598 StartY=-65.5 StartZ=0 EndX=0 EndY=-65.5 EndZ=0
    g4: LineSegment StartX=145.598 StartY=65.5 StartZ=0 EndX=145.598 EndY=-65.5 EndZ=0
    g5: LineSegment StartX=-153.016 StartY=65.5 StartZ=0 EndX=0 EndY=65.5 EndZ=0
    g6: LineSegment StartX=-1.2e-14 StartY=-65.5 StartZ=0 EndX=-153.016 EndY=-65.5 EndZ=0
    g7: LineSegment StartX=-153.016 StartY=-65.5 StartZ=0 EndX=-153.016 EndY=65.5 EndZ=0
  constraints (18):
    c: Coincident(g0,g-1)
    c: Diameter(g0) = 131
    c: Coincident(g1,g0)
    c: PointOnObject(g1,g0)
    c: Horizontal(g2)
    c: Horizontal(g3)
    c: Tangent(g3,g1) = 1.5708
    c: Tangent(g1,g2) = -1.5708
    c: Coincident(g4,g2)
    c: Coincident(g4,g3)
    c: Vertical(g4)
    c: Coincident(g6,g7)
    c: Coincident(g7,g5)
    c: Horizontal(g5)
    c: Horizontal(g6)
    c: Vertical(g7)
    c: Coincident(g5,g2)
    c: Coincident(g6,g3)
FEATURE [PartDesign::Pocket] Pocket005
  BaseFeature = -> Pad013
  Direction = (0,0,-1)
  Length = 6.5
  Length2 = 13
  Profile = -> Sketch_1
  ReferenceAxis = -> Sketch_1 [N_Axis]
  Suppressed = false
  Type = 4
FEATURE [PartDesign::CoordinateSystem] Block_ribb
  AttacherType = Attacher::AttachEngine3D
  AttachmentSupport = -> [Pocket005]
  MapMode = 2
FEATURE [Sketcher::SketchObject] Sketch_2
  ArcFitTolerance = 0
  FullyConstrained = false
  MakeInternals = false
  sketch-geometry (44):
    g0: LineSegment StartX=-0.25 StartY=33.6074 StartZ=0 EndX=-0.25 EndY=47.5 EndZ=0
    g1: LineSegment StartX=-0.25 StartY=47.5 StartZ=0 EndX=126.736 EndY=47.5 EndZ=0
    g2: LineSegment StartX=126.736 StartY=47.5 StartZ=0 EndX=126.736 EndY=47 EndZ=0
    g3: LineSegment StartX=126.736 StartY=47 StartZ=0 EndX=0.25 EndY=47 EndZ=0
    g4: LineSegment StartX=0.25 StartY=47 StartZ=0 EndX=0.25 EndY=33.6074 EndZ=0
    g5: LineSegment StartX=0.25 StartY=33.6074 StartZ=0 EndX=-0.25 EndY=33.6074 EndZ=0
    g6: ArcOfCircle CenterX=86.75 CenterY=76.5 CenterZ=0 NormalX=0 NormalY=0 NormalZ=1 AngleXU=0 Radius=1.5 StartAngle=4.71239 EndAngle=6.28319
    g7: ArcOfCircle CenterX=8.25 CenterY=76.5 CenterZ=0 NormalX=0 NormalY=0 NormalZ=1 AngleXU=0 Radius=1.5 StartAngle=3.14159 EndAngle=4.71239
    g8: LineSegment StartX=86.75 StartY=75 StartZ=0 EndX=8.25 EndY=75 EndZ=0
    g9: LineSegment StartX=88.25 StartY=105 StartZ=0 EndX=6.75 EndY=105 EndZ=0
    g10: LineSegment StartX=6.75 StartY=105 StartZ=0 EndX=6.75 EndY=76.5 EndZ=0
    g11: LineSegment StartX=88.25 StartY=105 StartZ=0 EndX=88.25 EndY=76.5 EndZ=0
    g12: GeomPoint [constr] X=47.5 Y=105 Z=0
    g13: Circle CenterX=-118 CenterY=93 CenterZ=0 NormalX=0 NormalY=0 NormalZ=1 AngleXU=0 Radius=6
    g14: Circle CenterX=118 CenterY=93 CenterZ=0 NormalX=0 NormalY=0 NormalZ=1 AngleXU=0 Radius=6
    g15: LineSegment StartX=-0.067348 StartY=-33.6074 StartZ=0 EndX=-0.067348 EndY=-47.5 EndZ=0
    g16: LineSegment StartX=-0.067348 StartY=-47.5 StartZ=0 EndX=126.736 EndY=-47.5 EndZ=0
    g17: LineSegment StartX=126.736 StartY=-47.5 StartZ=0 EndX=126.736 EndY=-47 EndZ=0
    g18: LineSegment StartX=126.736 StartY=-47 StartZ=0 EndX=0.25 EndY=-47 EndZ=0
    g19: LineSegment StartX=0.25 StartY=-47 StartZ=0 EndX=0.25 EndY=-33.6074 EndZ=0
    g20: LineSegment StartX=0.25 StartY=-33.6074 StartZ=0 EndX=-0.067348 EndY=-33.6074 EndZ=0
    g21: ArcOfCircle CenterX=-86.75 CenterY=76.5 CenterZ=0 NormalX=0 NormalY=0 NormalZ=1 AngleXU=0 Radius=1.5 StartAngle=3.14159 EndAngle=4.71239
    g22: ArcOfCircle CenterX=-8.25 CenterY=76.5 CenterZ=0 NormalX=0 NormalY=0 NormalZ=1 AngleXU=0 Radius=1.5 StartAngle=4.71239 EndAngle=6.28319
    g23: LineSegment StartX=-86.75 StartY=75 StartZ=0 EndX=-8.25 EndY=75 EndZ=0
    g24: LineSegment StartX=-88.25 StartY=105 StartZ=0 EndX=-6.75 EndY=105 EndZ=0
    g25: LineSegment StartX=-6.75 StartY=105 StartZ=0 EndX=-6.75 EndY=76.5 EndZ=0
    g26: LineSegment StartX=-88.25 StartY=105 StartZ=0 EndX=-88.25 EndY=76.5 EndZ=0
    g27: GeomPoint [constr] X=-47.5 Y=105 Z=0
    g28: ArcOfCircle CenterX=86.75 CenterY=-76.5 CenterZ=0 NormalX=0 NormalY=0 NormalZ=1 AngleXU=0 Radius=1.5 StartAngle=0 EndAngle=1.5708
    g29: ArcOfCircle CenterX=8.25 CenterY=-76.5 CenterZ=0 NormalX=0 NormalY=0 NormalZ=1 AngleXU=0 Radius=1.5 StartAngle=1.5708 EndAngle=3.14159
    g30: LineSegment StartX=86.75 StartY=-75 StartZ=0 EndX=8.25 EndY=-75 EndZ=0
    g31: LineSegment StartX=88.25 StartY=-105 StartZ=0 EndX=6.75 EndY=-105 EndZ=0
    g32: LineSegment StartX=6.75 StartY=-105 StartZ=0 EndX=6.75 EndY=-76.5 EndZ=0
    g33: LineSegment StartX=88.25 StartY=-105 StartZ=0 EndX=88.25 EndY=-76.5 EndZ=0
    g34: GeomPoint [constr] X=47.5 Y=-105 Z=0
    g35: Circle CenterX=-118 CenterY=-93 CenterZ=0 NormalX=0 NormalY=0 NormalZ=1 AngleXU=0 Radius=6
    g36: Circle CenterX=118 CenterY=-93 CenterZ=0 NormalX=0 NormalY=0 NormalZ=1 AngleXU=0 Radius=6
    g37: ArcOfCircle CenterX=-86.75 CenterY=-76.5 CenterZ=0 NormalX=0 NormalY=0 NormalZ=1 AngleXU=0 Radius=1.5 StartAngle=1.5708 EndAngle=3.14159
    g38: ArcOfCircle CenterX=-8.25 CenterY=-76.5 CenterZ=0 NormalX=0 NormalY=0 NormalZ=1 AngleXU=0 Radius=1.5 StartAngle=0 EndAngle=1.5708
    g39: LineSegment StartX=-86.75 StartY=-75 StartZ=0 EndX=-8.25 EndY=-75 EndZ=0
    g40: LineSegment StartX=-88.25 StartY=-105 StartZ=0 EndX=-6.75 EndY=-105 EndZ=0
    g41: LineSegment StartX=-6.75 StartY=-105 StartZ=0 EndX=-6.75 EndY=-76.5 EndZ=0
    g42: LineSegment StartX=-88.25 StartY=-105 StartZ=0 EndX=-88.25 EndY=-76.5 EndZ=0
    g43: GeomPoint [constr] X=-47.5 Y=-105 Z=0
  constraints (95):
    c: Vertical(g0)
    c: Coincident(g0,g1)
    c: Horizontal(g1)
    c: Coincident(g1,g2)
    c: Coincident(g2,g3)
    c: Horizontal(g3)
    c: Coincident(g3,g4)
    c: Vertical(g4)
    c: Coincident(g4,g5)
    c: Coincident(g5,g0)
    c: Vertical(g2)
    c: DistanceY(g2,g2) = 0.5
    c: DistanceX(g5,g5) = 0.5
    c: Tangent(g6,g8) = 1.5708
    c: Tangent(g8,g7) = 1.5708
    c: Equal(g6,g7)
    c: Horizontal(g8)
    c: Horizontal(g9)
    c: Vertical(g11)
    c: Vertical(g10)
    c: Tangent(g6,g11) = 1.5708
    c: Tangent(g7,g10) = -1.5708
    c: Coincident(g11,g9)
    c: Coincident(g9,g10)
    c: Symmetric(g9,g9,g12)
    c: Radius(g7) = 1.5
    c: Distance(g7,g9) = 30
    c: Diameter(g13) = 12
    c: Symmetric(g0,g4,g-2)
    c: DistanceY(g-1,g13) = 93
    c: DistanceX(g13,g-1) = 118
    c: DistanceY(g-1,g9) = 105
    c: DistanceX(g9,g9) = 81.5
    c: DistanceX(g-1,g9) = 6.75
    c: Diameter(g14) = 12
    c: Vertical(g15)
    c: Coincident(g15,g16)
    c: Horizontal(g16)
    c: Coincident(g16,g17)
    c: Coincident(g17,g18)
    c: Horizontal(g18)
    c: Coincident(g18,g19)
    c: Vertical(g19)
    c: Coincident(g19,g20)
    c: Coincident(g20,g15)
    c: Vertical(g17)
    c: Tangent(g21,g23) = -1.5708
    c: Tangent(g23,g22) = -1.5708
    c: Equal(g21,g22)
    c: Horizontal(g23)
    c: Horizontal(g24)
    c: Vertical(g26)
    c: Vertical(g25)
    c: Tangent(g21,g26) = -1.5708
    c: Tangent(g22,g25) = 1.5708
    c: Coincident(g26,g24)
    c: Coincident(g24,g25)
    c: Symmetric(g24,g24,g27)
    c: Radius(g22) = 1.5
    c: Distance(g22,g24) = 30
    c: Tangent(g28,g30) = -1.5708
    c: Tangent(g30,g29) = -1.5708
    c: Equal(g28,g29)
    c: Horizontal(g30)
    c: Horizontal(g31)
    c: Vertical(g33)
    c: Vertical(g32)
    c: Tangent(g28,g33) = -1.5708
    c: Tangent(g29,g32) = 1.5708
    c: Coincident(g33,g31)
    c: Coincident(g31,g32)
    c: Symmetric(g31,g31,g34)
    c: Radius(g29) = 1.5
    c: Distance(g29,g31) = 30
    c: Diameter(g35) = 12
    c: Diameter(g36) = 12
    c: Tangent(g37,g39) = 1.5708
    c: Tangent(g39,g38) = 1.5708
    c: Equal(g37,g38)
    c: Horizontal(g39)
    c: Horizontal(g40)
    c: Vertical(g42)
    c: Vertical(g41)
    c: Tangent(g37,g42) = 1.5708
    c: Tangent(g38,g41) = -1.5708
    c: Coincident(g42,g40)
    c: Coincident(g40,g41)
    c: Symmetric(g40,g40,g43)
    c: Radius(g38) = 1.5
    c: Distance(g38,g40) = 30
    c: Symmetric(g19,g4,g-1)
    c: Horizontal(g20)
    c: Symmetric(g17,g2,g-1)
    c: DistanceY(g17,g17) = 0.5
    c: DistanceY(g16,g1) = 95
FEATURE [PartDesign::Pocket] Pocket006
  BaseFeature = -> Pocket005
  Direction = (0,0,-1)
  Length = 50
  Length2 = 50
  Profile = -> Sketch_2
  ReferenceAxis = -> Sketch_2 [N_Axis]
  Suppressed = false
  Type = 4
FEATURE [Sketcher::SketchObject] Sketch028
  ArcFitTolerance = 0
  FullyConstrained = true
  MakeInternals = false
  MapMode = 5
  Placement = pos=(0,-75,0) rot=(1,0,0;1.5708rad)
  sketch-geometry (1):
    g0: Circle CenterX=74 CenterY=-21.75 CenterZ=0 NormalX=0 NormalY=0 NormalZ=1 AngleXU=0 Radius=6
  constraints (3):
    c: Diameter(g0) = 12
    c: DistanceY(g0,g-1) = 21.75
    c: DistanceX(g-1,g0) = 74
FEATURE [PartDesign::Pocket] Pocket011
  BaseFeature = -> Pocket006
  Direction = (0,1,-2e-16)
  Length = 5
  Length2 = 5
  Profile = -> Sketch028
  ReferenceAxis = -> Sketch028 [N_Axis]
  Suppressed = false
  Type = 1
FEATURE [PartDesign::Body] Body061  label="перегородка"
  AllowCompound = false
  Group = -> [Sketch022,Sketch021,Pad012,Pad013,Sketch_1,Pocket005,Block_ribb,Sketch_2,Pocket006,Sketch028,Pocket011]
  Origin = -> Origin062
  Tip = -> Pocket011
FEATURE [PartDesign::Pad] Pad017
  Direction = (0,0,1)
  Length = 37
  Length2 = 22.5
  Profile = -> Sketch021
  ReferenceAxis = -> Sketch021 [N_Axis]
  Reversed = true
  Suppressed = false
  Type = 4
FEATURE [PartDesign::Pocket] Pocket017
  BaseFeature = -> Pad017
  Direction = (0,0,-1)
  Length = 8.5
  Length2 = 13
  Profile = -> Sketch_1
  ReferenceAxis = -> Sketch_1 [N_Axis]
  Suppressed = false
  Type = 4
FEATURE [PartDesign::CoordinateSystem] Block_ribb001
  AttacherType = Attacher::AttachEngine3D
  AttachmentSupport = -> [Pocket017]
  MapMode = 2
FEATURE [PartDesign::Pocket] Pocket018
  BaseFeature = -> Pocket017
  Direction = (0,0,-1)
  Length = 50
  Length2 = 50
  Profile = -> Sketch_2
  ReferenceAxis = -> Sketch_2 [N_Axis]
  Suppressed = false
  Type = 4
FEATURE [PartDesign::Pocket] Pocket019
  BaseFeature = -> Pocket018
  Direction = (0,1,-2e-16)
  Length = 5
  Length2 = 5
  Profile = -> Sketch028
  ReferenceAxis = -> Sketch028 [N_Axis]
  Suppressed = false
  Type = 1
FEATURE [Sketcher::SketchObject] Sketch034
  ArcFitTolerance = 0
  AttachmentSupport = -> [XY_Plane062]
  FullyConstrained = false
  MakeInternals = false
  MapMode = 5
  sketch-geometry (4):
    g0: LineSegment StartX=-154.224 StartY=65.5 StartZ=0 EndX=161.628 EndY=65.5 EndZ=0
    g1: LineSegment StartX=161.628 StartY=65.5 StartZ=0 EndX=161.628 EndY=-65.5 EndZ=0
    g2: LineSegment StartX=161.628 StartY=-65.5 StartZ=0 EndX=-154.224 EndY=-65.5 EndZ=0
    g3: LineSegment StartX=-154.224 StartY=-65.5 StartZ=0 EndX=-154.224 EndY=65.5 EndZ=0
  constraints (9):
    c: Coincident(g0,g1)
    c: Coincident(g1,g2)
    c: Coincident(g2,g3)
    c: Coincident(g3,g0)
    c: Horizontal(g0)
    c: Horizontal(g2)
    c: Vertical(g3)
    c: Symmetric(g1,g0,g-1)
    c: DistanceY(g1,g1) = 131
FEATURE [PartDesign::Pocket] Pocket020
  BaseFeature = -> Pocket019
  Direction = (0,0,-1)
  Length = 25
  Length2 = -10.5
  Profile = -> Sketch034
  ReferenceAxis = -> Sketch034 [N_Axis]
  Reversed = true
  Suppressed = false
  Type = 4
FEATURE [PartDesign::Body] Body063  label="Перегородка_передняя"
  AllowCompound = false
  Group = -> [Pad017,Pocket017,Block_ribb001,Pocket018,Pocket019,Sketch034,Pocket020]
  Origin = -> Origin064
  Tip = -> Pocket020
FEATURE [PartDesign::CoordinateSystem] Block_ribb002
  AttacherType = Attacher::AttachEngine3D
  MapMode = 2
FEATURE [PartDesign::Pad] Pad018
  Direction = (0,0,1)
  Length = 12.5
  Length2 = 12.5
  Profile = -> Sketch021
  ReferenceAxis = -> Sketch021 [N_Axis]
  Reversed = true
  Suppressed = false
  Type = 4
FEATURE [Sketcher::SketchObject] Sketch035
  ArcFitTolerance = 0
  FullyConstrained = false
  MakeInternals = false
  MapMode = 5
  sketch-geometry (9):
    g0: LineSegment [constr] StartX=-110 StartY=-105 StartZ=0 EndX=-65.5 EndY=-105 EndZ=0
    g1: LineSegment [constr] StartX=-65.5 StartY=-105 StartZ=0 EndX=-65.5 EndY=105 EndZ=0
    g2: LineSegment [constr] StartX=-65.5 StartY=105 StartZ=0 EndX=-110 EndY=105 EndZ=0
    g3: LineSegment [constr] StartX=-110 StartY=105 StartZ=0 EndX=-110 EndY=-105 EndZ=0
    g4: LineSegment [constr] StartX=65.5 StartY=52.7372 StartZ=0 EndX=65.5 EndY=105 EndZ=0
    g5: LineSegment StartX=-110 StartY=-105 StartZ=0 EndX=65.5 EndY=-105 EndZ=0
    g6: LineSegment StartX=65.5 StartY=-105 StartZ=0 EndX=65.5 EndY=105 EndZ=0
    g7: LineSegment StartX=65.5 StartY=105 StartZ=0 EndX=-110 EndY=105 EndZ=0
    g8: LineSegment StartX=-110 StartY=105 StartZ=0 EndX=-110 EndY=-105 EndZ=0
  constraints (23):
    c: Coincident(g0,g1)
    c: Coincident(g1,g2)
    c: Coincident(g2,g3)
    c: Coincident(g3,g0)
    c: Horizontal(g0)
    c: Horizontal(g2)
    c: Vertical(g3)
    c: Vertical(g4)
    c: DistanceX(g1,g4) = 131
    c: Symmetric(g1,g4,g-2)
    c: DistanceY(g1,g1) = 210
    c: DistanceX(g0,g0) = 44.5
    c: Symmetric(g0,g1,g-1)
    c: Coincident(g5,g6)
    c: Coincident(g6,g7)
    c: Coincident(g7,g8)
    c: Coincident(g8,g5)
    c: Horizontal(g5)
    c: Horizontal(g7)
    c: Vertical(g6)
    c: Vertical(g8)
    c: Coincident(g5,g0)
    c: Coincident(g6,g4)
FEATURE [Sketcher::SketchObject] Sketch_004
  ArcFitTolerance = 0
  FullyConstrained = false
  MakeInternals = false
  sketch-geometry (32):
    g0: ArcOfCircle CenterX=86.75 CenterY=76.5 CenterZ=0 NormalX=0 NormalY=0 NormalZ=1 AngleXU=0 Radius=1.5 StartAngle=4.71239 EndAngle=6.28319
    g1: ArcOfCircle CenterX=8.25 CenterY=76.5 CenterZ=0 NormalX=0 NormalY=0 NormalZ=1 AngleXU=0 Radius=1.5 StartAngle=3.14159 EndAngle=4.71239
    g2: LineSegment StartX=86.75 StartY=75 StartZ=0 EndX=8.25 EndY=75 EndZ=0
    g3: LineSegment StartX=88.25 StartY=105 StartZ=0 EndX=6.75 EndY=105 EndZ=0
    g4: LineSegment StartX=6.75 StartY=105 StartZ=0 EndX=6.75 EndY=76.5 EndZ=0
    g5: LineSegment StartX=88.25 StartY=105 StartZ=0 EndX=88.25 EndY=76.5 EndZ=0
    g6: GeomPoint [constr] X=47.5 Y=105 Z=0
    g7: Circle CenterX=-118 CenterY=93 CenterZ=0 NormalX=0 NormalY=0 NormalZ=1 AngleXU=0 Radius=6
    g8: Circle CenterX=118 CenterY=93 CenterZ=0 NormalX=0 NormalY=0 NormalZ=1 AngleXU=0 Radius=6
    g9: ArcOfCircle CenterX=-86.75 CenterY=76.5 CenterZ=0 NormalX=0 NormalY=0 NormalZ=1 AngleXU=0 Radius=1.5 StartAngle=3.14159 EndAngle=4.71239
    g10: ArcOfCircle CenterX=-8.25 CenterY=76.5 CenterZ=0 NormalX=0 NormalY=0 NormalZ=1 AngleXU=0 Radius=1.5 StartAngle=4.71239 EndAngle=6.28319
    g11: LineSegment StartX=-86.75 StartY=75 StartZ=0 EndX=-8.25 EndY=75 EndZ=0
    g12: LineSegment StartX=-88.25 StartY=105 StartZ=0 EndX=-6.75 EndY=105 EndZ=0
    g13: LineSegment StartX=-6.75 StartY=105 StartZ=0 EndX=-6.75 EndY=76.5 EndZ=0
    g14: LineSegment StartX=-88.25 StartY=105 StartZ=0 EndX=-88.25 EndY=76.5 EndZ=0
    g15: GeomPoint [constr] X=-47.5 Y=105 Z=0
    g16: ArcOfCircle CenterX=86.75 CenterY=-76.5 CenterZ=0 NormalX=0 NormalY=0 NormalZ=1 AngleXU=0 Radius=1.5 StartAngle=0 EndAngle=1.5708
    g17: ArcOfCircle CenterX=8.25 CenterY=-76.5 CenterZ=0 NormalX=0 NormalY=0 NormalZ=1 AngleXU=0 Radius=1.5 StartAngle=1.5708 EndAngle=3.14159
    g18: LineSegment StartX=86.75 StartY=-75 StartZ=0 EndX=8.25 EndY=-75 EndZ=0
    g19: LineSegment StartX=88.25 StartY=-105 StartZ=0 EndX=6.75 EndY=-105 EndZ=0
    g20: LineSegment StartX=6.75 StartY=-105 StartZ=0 EndX=6.75 EndY=-76.5 EndZ=0
    g21: LineSegment StartX=88.25 StartY=-105 StartZ=0 EndX=88.25 EndY=-76.5 EndZ=0
    g22: GeomPoint [constr] X=47.5 Y=-105 Z=0
    g23: Circle CenterX=-118 CenterY=-93 CenterZ=0 NormalX=0 NormalY=0 NormalZ=1 AngleXU=0 Radius=6
    g24: Circle CenterX=118 CenterY=-93 CenterZ=0 NormalX=0 NormalY=0 NormalZ=1 AngleXU=0 Radius=6
    g25: ArcOfCircle CenterX=-86.75 CenterY=-76.5 CenterZ=0 NormalX=0 NormalY=0 NormalZ=1 AngleXU=0 Radius=1.5 StartAngle=1.5708 EndAngle=3.14159
    g26: ArcOfCircle CenterX=-8.25 CenterY=-76.5 CenterZ=0 NormalX=0 NormalY=0 NormalZ=1 AngleXU=0 Radius=1.5 StartAngle=0 EndAngle=1.5708
    g27: LineSegment StartX=-86.75 StartY=-75 StartZ=0 EndX=-8.25 EndY=-75 EndZ=0
    g28: LineSegment StartX=-88.25 StartY=-105 StartZ=0 EndX=-6.75 EndY=-105 EndZ=0
    g29: LineSegment StartX=-6.75 StartY=-105 StartZ=0 EndX=-6.75 EndY=-76.5 EndZ=0
    g30: LineSegment StartX=-88.25 StartY=-105 StartZ=0 EndX=-88.25 EndY=-76.5 EndZ=0
    g31: GeomPoint [constr] X=-47.5 Y=-105 Z=0
  constraints (65):
    c: Tangent(g0,g2) = 1.5708
    c: Tangent(g2,g1) = 1.5708
    c: Equal(g0,g1)
    c: Horizontal(g2)
    c: Horizontal(g3)
    c: Vertical(g5)
    c: Vertical(g4)
    c: Tangent(g0,g5) = 1.5708
    c: Tangent(g1,g4) = -1.5708
    c: Coincident(g5,g3)
    c: Coincident(g3,g4)
    c: Symmetric(g3,g3,g6)
    c: Radius(g1) = 1.5
    c: Distance(g1,g3) = 30
    c: Diameter(g7) = 12
    c: DistanceY(g-1,g7) = 93
    c: DistanceX(g7,g-1) = 118
    c: DistanceY(g-1,g3) = 105
    c: DistanceX(g3,g3) = 81.5
    c: DistanceX(g-1,g3) = 6.75
    c: Diameter(g8) = 12
    c: Tangent(g9,g11) = -1.5708
    c: Tangent(g11,g10) = -1.5708
    c: Equal(g9,g10)
    c: Horizontal(g11)
    c: Horizontal(g12)
    c: Vertical(g14)
    c: Vertical(g13)
    c: Tangent(g9,g14) = -1.5708
    c: Tangent(g10,g13) = 1.5708
    c: Coincident(g14,g12)
    c: Coincident(g12,g13)
    c: Symmetric(g12,g12,g15)
    c: Radius(g10) = 1.5
    c: Distance(g10,g12) = 30
    c: Tangent(g16,g18) = -1.5708
    c: Tangent(g18,g17) = -1.5708
    c: Equal(g16,g17)
    c: Horizontal(g18)
    c: Horizontal(g19)
    c: Vertical(g21)
    c: Vertical(g20)
    c: Tangent(g16,g21) = -1.5708
    c: Tangent(g17,g20) = 1.5708
    c: Coincident(g21,g19)
    c: Coincident(g19,g20)
    c: Symmetric(g19,g19,g22)
    c: Radius(g17) = 1.5
    c: Distance(g17,g19) = 30
    c: Diameter(g23) = 12
    c: Diameter(g24) = 12
    c: Tangent(g25,g27) = 1.5708
    c: Tangent(g27,g26) = 1.5708
    c: Equal(g25,g26)
    c: Horizontal(g27)
    c: Horizontal(g28)
    c: Vertical(g30)
    c: Vertical(g29)
    c: Tangent(g25,g30) = 1.5708
    c: Tangent(g26,g29) = -1.5708
    c: Coincident(g30,g28)
    c: Coincident(g28,g29)
    c: Symmetric(g28,g28,g31)
    c: Radius(g26) = 1.5
    c: Distance(g26,g28) = 30
FEATURE [PartDesign::Pocket] Pocket021
  BaseFeature = -> Pad018
  Direction = (0,0,-1)
  Length = 20
  Length2 = 20
  Profile = -> Sketch_004
  ReferenceAxis = -> Sketch_004 [N_Axis]
  Suppressed = false
  Type = 4
FEATURE [PartDesign::Pocket] Pocket022
  BaseFeature = -> Pocket021
  Direction = (0,0,-1)
  Length = 20
  Length2 = 20
  Profile = -> Sketch035
  ReferenceAxis = -> Sketch035 [N_Axis]
  Suppressed = false
  Type = 4
FEATURE [PartDesign::Body] Body064  label="перегородка_ползуна"
  AllowCompound = false
  Group = -> [Sketch035,Pad018,Block_ribb002,Sketch_004,Pocket021,Pocket022]
  Origin = -> Origin065
  Tip = -> Pocket022
FEATURE [Sketcher::SketchObject] Sketch038
  ArcFitTolerance = 0
  FullyConstrained = true
  MakeInternals = false
  MapMode = 5
  sketch-geometry (26):
    g0: LineSegment [constr] StartX=-103 StartY=-65 StartZ=0 EndX=103 EndY=-65 EndZ=0
    g1: LineSegment StartX=103 StartY=-65 StartZ=0 EndX=103 EndY=65 EndZ=0
    g2: LineSegment [constr] StartX=103 StartY=65 StartZ=0 EndX=-103 EndY=65 EndZ=0
    g3: LineSegment StartX=-103 StartY=65 StartZ=0 EndX=-103 EndY=-65 EndZ=0
    g4: ArcOfCircle CenterX=0 CenterY=40 CenterZ=0 NormalX=0 NormalY=0 NormalZ=1 AngleXU=0 Radius=20.25 StartAngle=1.05267 EndAngle=2.08892
    g5: ArcOfCircle CenterX=0 CenterY=0 CenterZ=0 NormalX=0 NormalY=0 NormalZ=1 AngleXU=0 Radius=55 StartAngle=2.08892 EndAngle=4.19427
    g6: ArcOfCircle CenterX=0 CenterY=0 CenterZ=0 NormalX=0 NormalY=0 NormalZ=1 AngleXU=0 Radius=55 StartAngle=5.23051 EndAngle=7.33586
    g7: ArcOfCircle CenterX=0 CenterY=-40 CenterZ=0 NormalX=0 NormalY=0 NormalZ=1 AngleXU=0 Radius=20.25 StartAngle=4.19427 EndAngle=5.23051
    g8: LineSegment StartX=-27.2388 StartY=47.7813 StartZ=0 EndX=-10.0288 EndY=57.5922 EndZ=0
    g9: LineSegment StartX=10.0288 StartY=57.5922 StartZ=0 EndX=27.2388 EndY=47.7813 EndZ=0
    g10: LineSegment StartX=-27.2388 StartY=-47.7812 StartZ=0 EndX=-10.0288 EndY=-57.5922 EndZ=0
    g11: LineSegment StartX=10.0288 StartY=-57.5922 StartZ=0 EndX=27.2388 EndY=-47.7812 EndZ=0
    g12: LineSegment StartX=-99 StartY=69.5 StartZ=0 EndX=99 EndY=69.5 EndZ=0
    g13: LineSegment StartX=-103 StartY=65 StartZ=0 EndX=-103 EndY=65.5 EndZ=0
    g14: LineSegment StartX=103 StartY=65.5 StartZ=0 EndX=103 EndY=65 EndZ=0
    g15: ArcOfCircle CenterX=-99 CenterY=65.5 CenterZ=0 NormalX=0 NormalY=0 NormalZ=1 AngleXU=0 Radius=4 StartAngle=1.5708 EndAngle=3.14159
    g16: ArcOfCircle CenterX=99 CenterY=65.5 CenterZ=0 NormalX=0 NormalY=0 NormalZ=1 AngleXU=0 Radius=4 StartAngle=4e-16 EndAngle=1.5708
    g17: ArcOfCircle CenterX=-99 CenterY=-65.5 CenterZ=0 NormalX=0 NormalY=0 NormalZ=1 AngleXU=0 Radius=4 StartAngle=3.14159 EndAngle=4.71239
    g18: LineSegment StartX=-103 StartY=-65 StartZ=0 EndX=-103 EndY=-65.5 EndZ=0
    g19: LineSegment StartX=-99 StartY=-69.5 StartZ=0 EndX=99 EndY=-69.5 EndZ=0
    g20: ArcOfCircle CenterX=99 CenterY=-65.5 CenterZ=0 NormalX=0 NormalY=0 NormalZ=1 AngleXU=0 Radius=4 StartAngle=4.71239 EndAngle=6.28319
    g21: LineSegment StartX=103 StartY=-65.5 StartZ=0 EndX=103 EndY=-65 EndZ=0
    g22: Circle CenterX=-95 CenterY=55 CenterZ=0 NormalX=0 NormalY=0 NormalZ=1 AngleXU=0 Radius=3
    g23: Circle CenterX=95 CenterY=55 CenterZ=0 NormalX=0 NormalY=0 NormalZ=1 AngleXU=0 Radius=3
    g24: Circle CenterX=-95 CenterY=-55 CenterZ=0 NormalX=0 NormalY=0 NormalZ=1 AngleXU=0 Radius=3
    g25: Circle CenterX=95 CenterY=-55 CenterZ=0 NormalX=0 NormalY=0 NormalZ=1 AngleXU=0 Radius=3
  constraints (58):
    c: Coincident(g0,g1)
    c: Coincident(g1,g2)
    c: Coincident(g2,g3)
    c: Coincident(g3,g0)
    c: Horizontal(g0)
    c: Vertical(g1)
    c: Symmetric(g2,g1,g-2)
    c: Symmetric(g2,g0,g-1)
    c: DistanceX(g2,g2) = 206
    c: PointOnObject(g4,g-2)
    c: Diameter(g4) = 40.5
    c: Equal(g4,g7)
    c: Symmetric(g4,g7,g-1)
    c: Equal(g5,g6)
    c: Tangent(g5,g10) = -1.5708
    c: Tangent(g5,g8) = 1.5708
    c: Tangent(g4,g8) = 1.5708
    c: Tangent(g4,g9) = 1.5708
    c: Tangent(g7,g11) = -1.5708
    c: Tangent(g7,g10) = -1.5708
    c: Tangent(g6,g9) = 1.5708
    c: Tangent(g6,g11) = -1.5708
    c: Distance(g-1,g4) = 40
    c: DistanceY(g1,g1) = 130
    c: Radius(g6) = 55
    c: Coincident(g5,g-1)
    c: Coincident(g6,g5)
    c: Coincident(g13,g3)
    c: Coincident(g14,g1)
    c: Tangent(g13,g15) = 1.5708
    c: Tangent(g12,g15) = 1.5708
    c: Tangent(g12,g16) = 1.5708
    c: Tangent(g14,g16) = 1.5708
    c: Vertical(g13)
    c: Vertical(g14)
    c: Symmetric(g15,g16,g-2)
    c: DistanceY(g1,g12) = 4.5
    c: Radius(g16) = 4
    c: Tangent(g18,g17) = -1.5708
    c: Tangent(g19,g17) = -1.5708
    c: Tangent(g19,g20) = -1.5708
    c: Vertical(g18)
    c: Symmetric(g17,g20,g-2)
    c: Symmetric(g17,g15,g-1)
    c: Coincident(g18,g3)
    c: Coincident(g21,g1)
    c: Vertical(g21)
    c: Equal(g21,g18)
    c: Coincident(g20,g21)
    c: Equal(g22,g23)
    c: Equal(g23,g25)
    c: Equal(g25,g24)
    c: Diameter(g23) = 6
    c: Symmetric(g22,g23,g-2)
    c: Symmetric(g24,g25,g-2)
    c: Symmetric(g24,g22,g-1)
    c: DistanceY(g24,g22) = 110
    c: DistanceX(g24,g25) = 190
FEATURE [PartDesign::Pad] Pad020
  Direction = (0,0,1)
  Length = 22.5
  Length2 = 5.5
  Midplane = true
  Profile = -> Sketch038
  ReferenceAxis = -> Sketch038 [N_Axis]
  Suppressed = false
  Type = 4
FEATURE [PartDesign::CoordinateSystem] Shtok003
  AttacherType = Attacher::AttachEngine3D
  AttachmentSupport = -> [Sketch038]
  MapMode = 2
FEATURE [PartDesign::CoordinateSystem] Piston001
  AttacherType = Attacher::AttachEngine3D
  AttachmentSupport = -> [XZ_Plane071]
  MapMode = 2
  Placement = pos=(0,0,0) rot=(1,0,0;1.5708rad)
FEATURE [Sketcher::SketchObject] Sketch041
  ArcFitTolerance = 0
  AttachmentSupport = -> [XY_Plane069]
  FullyConstrained = true
  MakeInternals = false
  MapMode = 5
  sketch-geometry (6):
    g0: Circle [constr] CenterX=0 CenterY=85 CenterZ=0 NormalX=0 NormalY=0 NormalZ=1 AngleXU=0 Radius=11.5
    g1: LineSegment StartX=-45.5 StartY=147 StartZ=0 EndX=45.5 EndY=147 EndZ=0
    g2: LineSegment StartX=-45.5 StartY=147 StartZ=0 EndX=-45.5 EndY=51 EndZ=0
    g3: LineSegment StartX=0 StartY=51 StartZ=0 EndX=-45.5 EndY=51 EndZ=0
    g4: LineSegment StartX=45.5 StartY=147 StartZ=0 EndX=45.5 EndY=51 EndZ=0
    g5: LineSegment StartX=0 StartY=51 StartZ=0 EndX=45.5 EndY=51 EndZ=0
  constraints (15):
    c: Coincident(g2,g1)
    c: Vertical(g2)
    c: Symmetric(g1,g1,g-2)
    c: DistanceX(g1,g1) = 91
    c: PointOnObject(g3,g-2)
    c: Vertical(g4)
    c: Block(g0)
    c: Coincident(g1,g4)
    c: DistanceY(g0,g1) = 62
    c: DistanceY(g3,g0) = 34
    c: Horizontal(g3)
    c: Coincident(g2,g3)
    c: Coincident(g5,g3)
    c: Coincident(g5,g4)
    c: Horizontal(g5)
FEATURE [PartDesign::Pad] Pad021
  Direction = (0,0,1)
  Length = 100
  Length2 = 10
  Midplane = true
  Profile = -> Sketch041
  ReferenceAxis = -> Sketch041 [N_Axis]
  Suppressed = false
  Type = 0
FEATURE [PartDesign::Body] Body070  label="Поршень003"
  AllowCompound = false
  Group = -> [Sketch041,Pad021]
  Origin = -> Origin071
  Tip = -> Pad021
FEATURE [Sketcher::SketchObject] Sketch042
  ArcFitTolerance = 0
  AttachmentSupport = -> [XZ_Plane071]
  FullyConstrained = false
  MakeInternals = false
  MapMode = 5
  Placement = pos=(0,0,0) rot=(1,0,0;1.5708rad)
  sketch-geometry (2):
    g0: GeomPoint [constr] X=-87.5 Y=-1.47e-14 Z=0
    g1: Circle CenterX=0 CenterY=0 CenterZ=0 NormalX=0 NormalY=0 NormalZ=1 AngleXU=0 Radius=45.5
  constraints (2):
    c: Coincident(g1,g-1)
    c: Diameter(g1) = 91
FEATURE [PartDesign::Pad] Pad022
  Direction = (0,-1,2e-16)
  Length = 200
  Length2 = 10
  Placement = pos=(0,0,0) rot=(1,0,0;1.5708rad)
  Profile = -> Sketch042
  ReferenceAxis = -> Sketch042 [N_Axis]
  Reversed = true
  Suppressed = false
  Type = 0
FEATURE [PartDesign::Boolean] Boolean004
  BaseFeature = -> Pad022
  Group = -> [Body070]
  Suppressed = false
  Type = 2
  UsePlacement = false
FEATURE [Sketcher::SketchObject] Sketch043
  ArcFitTolerance = 0
  FullyConstrained = true
  MakeInternals = false
  MapMode = 5
  Placement = pos=(0,0,0) rot=(1,0,0;1.5708rad)
  sketch-geometry (2):
    g0: Circle CenterX=0 CenterY=0 CenterZ=0 NormalX=0 NormalY=0 NormalZ=1 AngleXU=0 Radius=41
    g1: Circle CenterX=0 CenterY=0 CenterZ=0 NormalX=0 NormalY=0 NormalZ=1 AngleXU=0 Radius=15
  constraints (4):
    c: Coincident(g0,g-1)
    c: Diameter(g0) = 82
    c: Coincident(g1,g0)
    c: Diameter(g1) = 30
FEATURE [PartDesign::Pocket] Pocket025
  BaseFeature = -> Boolean004
  Direction = (0,1,-2e-16)
  Length = 138
  Length2 = 5
  Profile = -> Sketch043
  ReferenceAxis = -> Sketch043 [N_Axis]
  Suppressed = false
  Type = 0
FEATURE [Sketcher::SketchObject] Sketch044
  ArcFitTolerance = 0
  AttachmentSupport = -> [XZ_Plane071]
  FullyConstrained = false
  MakeInternals = false
  MapMode = 5
  Placement = pos=(0,0,0) rot=(1,0,0;1.5708rad)
  sketch-geometry (3):
    g0: GeomPoint [constr] X=-87.5 Y=-1.47e-14 Z=0
    g1: Circle CenterX=0 CenterY=0 CenterZ=0 NormalX=0 NormalY=0 NormalZ=1 AngleXU=0 Radius=43
    g2: Circle CenterX=0 CenterY=0 CenterZ=0 NormalX=0 NormalY=0 NormalZ=1 AngleXU=0 Radius=47.5
  constraints (4):
    c: Coincident(g1,g-1)
    c: Coincident(g2,g1)
    c: Diameter(g1) = 86
    c: Diameter(g2) = 95
FEATURE [PartDesign::Pocket] Pocket026  label="Pocket002-ring002"
  BaseFeature = -> Pocket025
  Direction = (0,1,-2e-16)
  Length = 143
  Length2 = -141
  Profile = -> Sketch044
  ReferenceAxis = -> Sketch044 [N_Axis]
  Suppressed = false
  Type = 4
FEATURE [PartDesign::Pocket] Pocket027  label="Pocket003-ring003"
  BaseFeature = -> Pocket026
  Direction = (0,1,-2e-16)
  Length = 138
  Length2 = -136
  Profile = -> Sketch044
  ReferenceAxis = -> Sketch044 [N_Axis]
  Suppressed = false
  Type = 4
FEATURE [PartDesign::Pocket] Pocket028  label="Pocket004-komp-ring001"
  BaseFeature = -> Pocket027
  Direction = (0,1,-2e-16)
  Length = 55
  Length2 = -58
  Profile = -> Sketch044
  ReferenceAxis = -> Sketch044 [N_Axis]
  Suppressed = false
  Type = 4
FEATURE [Sketcher::SketchObject] Sketch045
  ArcFitTolerance = 0
  AttachmentSupport = -> [XY_Plane072]
  FullyConstrained = true
  MakeInternals = false
  MapMode = 5
  sketch-geometry (11):
    g0: LineSegment [constr] StartX=-120 StartY=252 StartZ=0 EndX=120 EndY=252 EndZ=0
    g1: LineSegment [constr] StartX=120 StartY=252 StartZ=0 EndX=120 EndY=-252 EndZ=0
    g2: LineSegment StartX=120 StartY=-252 StartZ=0 EndX=-120 EndY=-252 EndZ=0
    g3: LineSegment [constr] StartX=-120 StartY=-252 StartZ=0 EndX=-120 EndY=252 EndZ=0
    g4: LineSegment [constr] StartX=-120 StartY=252 StartZ=0 EndX=-120 EndY=75.5 EndZ=0
    g5: LineSegment [constr] StartX=-120 StartY=75.5 StartZ=0 EndX=120 EndY=75.5 EndZ=0
    g6: LineSegment [constr] StartX=120 StartY=75.5 StartZ=0 EndX=120 EndY=252 EndZ=0
    g7: LineSegment StartX=-120 StartY=-252 StartZ=0 EndX=-120 EndY=-75.5 EndZ=0
    g8: LineSegment StartX=-120 StartY=-75.5 StartZ=0 EndX=120 EndY=-75.5 EndZ=0
    g9: LineSegment [constr] StartX=120 StartY=-75.5 StartZ=0 EndX=120 EndY=-252 EndZ=0
    g10: LineSegment StartX=120 StartY=-75.5 StartZ=0 EndX=120 EndY=-252 EndZ=0
  constraints (28):
    c: Coincident(g0,g1)
    c: Coincident(g1,g2)
    c: Coincident(g2,g3)
    c: Coincident(g3,g0)
    c: Horizontal(g2)
    c: Vertical(g1)
    c: Symmetric(g0,g0,g-2)
    c: Symmetric(g0,g2,g-1)
    c: Coincident(g0,g4)
    c: PointOnObject(g4,g3)
    c: Coincident(g4,g5)
    c: PointOnObject(g5,g1)
    c: Horizontal(g5)
    c: Coincident(g5,g6)
    c: Coincident(g6,g0)
    c: Coincident(g2,g7)
    c: PointOnObject(g7,g3)
    c: Coincident(g7,g8)
    c: PointOnObject(g8,g1)
    c: Horizontal(g8)
    c: Coincident(g8,g9)
    c: Coincident(g9,g2)
    c: Equal(g9,g6)
    c: DistanceX(g2,g2) = 240
    c: Coincident(g10,g8)
    c: Coincident(g10,g2)
    c: DistanceY(g2,g-1) = 252
    c: DistanceY(g7,g7) = 176.5
FEATURE [PartDesign::Pad] Pad024
  Direction = (0,0,1)
  Length = 28
  Length2 = 78
  Midplane = true
  Profile = -> Sketch045
  ReferenceAxis = -> Sketch045 [N_Axis]
  Suppressed = false
  Type = 4
FEATURE [PartDesign::Body] Body073
  AllowCompound = false
  Group = -> [Sketch045,Pad024]
  Origin = -> Origin074
  Placement = pos=(0,0,25) rot=(0,0,1;0rad)
  Tip = -> Pad024
FEATURE [PartDesign::CoordinateSystem] Cylynder001
  AttacherType = Attacher::AttachEngine3D
  AttachmentSupport = -> [Body073]
  MapMode = 2
  Placement = pos=(0,0,25) rot=(0,0,1;0rad)
FEATURE [Sketcher::SketchObject] Sketch046
  ArcFitTolerance = 0
  AttachmentSupport = -> [XZ_Plane072]
  FullyConstrained = false
  MakeInternals = false
  MapMode = 5
  Placement = pos=(0,0,0) rot=(1,0,0;1.5708rad)
  sketch-geometry (12):
    g0: ArcOfCircle [constr] CenterX=-53 CenterY=1.3e-15 CenterZ=0 NormalX=0 NormalY=0 NormalZ=1 AngleXU=0 Radius=46 StartAngle=1.5708 EndAngle=4.71239
    g1: ArcOfCircle [constr] CenterX=0 CenterY=0 CenterZ=0 NormalX=0 NormalY=0 NormalZ=1 AngleXU=0 Radius=46 StartAngle=4.71239 EndAngle=7.85398
    g2: LineSegment [constr] StartX=-53 StartY=-46 StartZ=0 EndX=-7.1e-15 EndY=-46 EndZ=0
    g3: LineSegment [constr] StartX=1.41e-14 StartY=46 StartZ=0 EndX=-53 EndY=46 EndZ=0
    g4: LineSegment StartX=-222.305 StartY=100 StartZ=0 EndX=222.305 EndY=100 EndZ=0
    g5: LineSegment StartX=222.305 StartY=100 StartZ=0 EndX=222.305 EndY=-100 EndZ=0
    g6: LineSegment StartX=222.305 StartY=-100 StartZ=0 EndX=-222.305 EndY=-100 EndZ=0
    g7: LineSegment StartX=-222.305 StartY=-100 StartZ=0 EndX=-222.305 EndY=100 EndZ=0
    g8: Circle CenterX=-53 CenterY=1.3e-15 CenterZ=0 NormalX=0 NormalY=0 NormalZ=1 AngleXU=0 Radius=46
    g9: Circle [constr] CenterX=0 CenterY=0 CenterZ=0 NormalX=0 NormalY=0 NormalZ=1 AngleXU=0 Radius=46
    g10: Circle CenterX=53 CenterY=0 CenterZ=0 NormalX=0 NormalY=0 NormalZ=1 AngleXU=0 Radius=46
    g11: LineSegment [constr] StartX=1.41e-14 StartY=46 StartZ=0 EndX=53 EndY=46 EndZ=0
  constraints (28):
    c: Tangent(g0,g2) = -1.5708
    c: Tangent(g2,g1) = -1.5708
    c: Tangent(g1,g3) = -1.5708
    c: Tangent(g3,g0) = -1.5708
    c: Equal(g0,g1)
    c: Horizontal(g2)
    c: DistanceY(g0,g0) = 92
    c: Coincident(g4,g5)
    c: Coincident(g5,g6)
    c: Coincident(g6,g7)
    c: Coincident(g7,g4)
    c: Horizontal(g6)
    c: Vertical(g7)
    c: DistanceY(g5,g5) = 200
    c: Symmetric(g5,g4,g-1)
    c: Symmetric(g4,g4,g-2)
    c: Coincident(g8,g0)
    c: Coincident(g9,g1)
    c: Equal(g8,g0)
    c: Equal(g9,g1)
    c: Coincident(g9,g-1)
    c: PointOnObject(g10,g-1)
    c: Equal(g9,g10)
    c: Coincident(g11,g1)
    c: PointOnObject(g11,g10)
    c: Horizontal(g11)
    c: Equal(g3,g11)
    c: DistanceX(g8,g10) = 106
FEATURE [PartDesign::Pad] Pad023
  Direction = (0,-1,2e-16)
  Length = 300
  Length2 = 10
  Placement = pos=(0,0,0) rot=(1,0,0;1.5708rad)
  Profile = -> Sketch046
  ReferenceAxis = -> Sketch046 [N_Axis]
  Suppressed = false
  Type = 0
FEATURE [PartDesign::Boolean] Boolean005
  BaseFeature = -> Pad023
  Group = -> [Body073]
  Suppressed = false
  Type = 2
  UsePlacement = false
FEATURE [Sketcher::SketchObject] Sketch047
  ArcFitTolerance = 0
  AttachmentSupport = -> [XY_Plane071]
  FullyConstrained = true
  MakeInternals = false
  MapMode = 5
  sketch-geometry (2):
    g0: Circle CenterX=-137 CenterY=-90 CenterZ=0 NormalX=0 NormalY=0 NormalZ=1 AngleXU=0 Radius=30.5
    g1: Circle CenterX=137 CenterY=-90 CenterZ=0 NormalX=0 NormalY=0 NormalZ=1 AngleXU=0 Radius=30.5
  constraints (5):
    c: Diameter(g0) = 61
    c: Symmetric(g0,g1,g-2)
    c: DistanceY(g0,g-1) = 90
    c: DistanceX(g0,g1) = 274
    c: Equal(g1,g0)
FEATURE [Sketcher::SketchObject] Sketch048
  ArcFitTolerance = 0
  AttachmentSupport = -> [XY_Plane071]
  FullyConstrained = false
  MakeInternals = false
  MapMode = 5
  sketch-geometry (17):
    g0: LineSegment [constr] StartX=72.5228 StartY=-25.9373 StartZ=0 EndX=72.5228 EndY=-109 EndZ=0
    g1: LineSegment [constr] StartX=72.5228 StartY=-109 StartZ=0 EndX=-72.5228 EndY=-109 EndZ=0
    g2: LineSegment [constr] StartX=-72.5228 StartY=-109 StartZ=0 EndX=-72.5228 EndY=-25.9373 EndZ=0
    g3: LineSegment StartX=-72.5228 StartY=-25.9373 StartZ=0 EndX=-160.839 EndY=-25.9373 EndZ=0
    g4: LineSegment StartX=-160.839 StartY=-25.9373 StartZ=0 EndX=-160.839 EndY=-150.037 EndZ=0
    g5: LineSegment StartX=-160.839 StartY=-150.037 StartZ=0 EndX=-95 EndY=-174 EndZ=0
    g6: LineSegment StartX=-95 StartY=-174 StartZ=0 EndX=-95 EndY=-193.155 EndZ=0
    g7: LineSegment StartX=-95 StartY=-193.155 StartZ=0 EndX=-179.18 EndY=-162.516 EndZ=0
    g8: LineSegment StartX=-179.18 StartY=-162.516 StartZ=0 EndX=-179.18 EndY=-8.0171 EndZ=0
    g9: LineSegment StartX=-179.18 StartY=-8.0171 StartZ=0 EndX=179.18 EndY=-8.0171 EndZ=0
    g10: LineSegment StartX=179.18 StartY=-8.0171 StartZ=0 EndX=179.18 EndY=-156.131 EndZ=0
    g11: LineSegment StartX=179.18 StartY=-156.131 StartZ=0 EndX=95 EndY=-186.77 EndZ=0
    g12: LineSegment StartX=95 StartY=-186.77 StartZ=0 EndX=95 EndY=-174 EndZ=0
    g13: LineSegment StartX=95 StartY=-174 StartZ=0 EndX=160.839 EndY=-150.037 EndZ=0
    g14: LineSegment StartX=160.839 StartY=-150.037 StartZ=0 EndX=160.839 EndY=-25.9373 EndZ=0
    g15: LineSegment StartX=160.839 StartY=-25.9373 StartZ=0 EndX=72.5228 EndY=-25.9373 EndZ=0
    g16: LineSegment StartX=-72.5228 StartY=-25.9373 StartZ=0 EndX=72.5228 EndY=-25.9373 EndZ=0
  constraints (43):
    c: Coincident(g0,g1)
    c: Coincident(g1,g2)
    c: Vertical(g0)
    c: Vertical(g2)
    c: DistanceY(g0,g-1) = 109
    c: Symmetric(g1,g0,g-2)
    c: Coincident(g2,g3)
    c: Horizontal(g3)
    c: Coincident(g3,g4)
    c: Vertical(g4)
    c: Coincident(g4,g5)
    c: Coincident(g5,g6)
    c: Vertical(g6)
    c: Coincident(g6,g7)
    c: Coincident(g7,g8)
    c: Vertical(g8)
    c: Coincident(g8,g9)
    c: Coincident(g9,g10)
    c: Vertical(g10)
    c: Coincident(g10,g11)
    c: Coincident(g11,g12)
    c: Vertical(g12)
    c: Coincident(g12,g13)
    c: Coincident(g13,g14)
    c: Vertical(g14)
    c: Coincident(g14,g15)
    c: Coincident(g15,g0)
    c: Horizontal(g15)
    c: Symmetric(g8,g9,g-2)
    c: Equal(g3,g15)
    c: Parallel(g5,g7)
    c: Parallel(g13,g11)
    c: Distance(g12,g11) = 12
    c: Angle(g5) = -0.349066
    c: Angle(g13) = 0.349066
    c: Symmetric(g5,g12,g-2)
    c: DistanceX(g5,g12) = 190
    c: DistanceY(g5,g-1) = 174
    c: Block(g9)
    c: Distance(g5,g7) = 18
    c: Coincident(g16,g3)
    c: Coincident(g16,g15)
    c: Horizontal(g16)
FEATURE [PartDesign::Pocket] Pocket029
  BaseFeature = -> Boolean005
  Direction = (0,0,-1)
  Length = 60
  Length2 = 5
  Midplane = true
  Profile = -> Sketch048
  ReferenceAxis = -> Sketch048 [N_Axis]
  Suppressed = false
  Type = 0
FEATURE [Sketcher::SketchObject] Sketch049
  ArcFitTolerance = 0
  FullyConstrained = true
  MakeInternals = false
  MapMode = 5
  Placement = pos=(0,0,0) rot=(1,0,0;1.5708rad)
  sketch-geometry (1):
    g0: Circle CenterX=0 CenterY=0 CenterZ=0 NormalX=0 NormalY=0 NormalZ=1 AngleXU=0 Radius=30
  constraints (2):
    c: Coincident(g0,g-1)
    c: Diameter(g0) = 60
FEATURE [PartDesign::Pocket] Pocket030  label="Pocket023-conrod-polzun001"
  BaseFeature = -> Pocket028
  Direction = (0,1,-2e-16)
  Length = 110
  Length2 = 5
  Profile = -> Sketch049
  ReferenceAxis = -> Sketch049 [N_Axis]
  Suppressed = false
  Type = 0
FEATURE [PartDesign::Pocket] Pocket031  label="Pocket002-ring3"
  BaseFeature = -> Pocket030
  Direction = (0,1,-2e-16)
  Length = 63
  Length2 = -61
  Profile = -> Sketch044
  ReferenceAxis = -> Sketch044 [N_Axis]
  Suppressed = false
  Type = 4
FEATURE [Sketcher::SketchObject] Sketch050
  ArcFitTolerance = 0
  AttachmentSupport = -> [YZ_Plane072]
  FullyConstrained = false
  MakeInternals = false
  MapMode = 5
  Placement = pos=(0,0,0) rot=(0.57735,0.57735,0.57735;2.0944rad)
  sketch-geometry (4):
    g0: LineSegment StartX=-184.527 StartY=91.8627 StartZ=0 EndX=-217.963 EndY=0 EndZ=0
    g1: LineSegment StartX=-217.963 StartY=0 StartZ=0 EndX=-202 EndY=0 EndZ=0
    g2: LineSegment StartX=-202 StartY=0 StartZ=0 EndX=-168.565 EndY=91.8627 EndZ=0
    g3: LineSegment StartX=-168.565 StartY=91.8627 StartZ=0 EndX=-184.527 EndY=91.8627 EndZ=0
  constraints (11):
    c: Coincident(g0,g1)
    c: Horizontal(g1)
    c: Coincident(g1,g2)
    c: Coincident(g2,g3)
    c: Coincident(g3,g0)
    c: Horizontal(g3)
    c: Equal(g1,g3)
    c: Angle(g2) = 1.22173
    c: Distance(g1,g0) = 15
    c: PointOnObject(g1,g-1)
    c: DistanceX(g1,g-1) = 202
FEATURE [PartDesign::Body] Body072  label="Цилиндр"
  AllowCompound = false
  Group = -> [Sketch046,Pad023,Boolean005,Cylynder001,Sketch047,Sketch048,Pocket029,Sketch050]
  Origin = -> Origin073
  Placement = pos=(0,0,25) rot=(0,0,1;0rad)
  Tip = -> Pocket029
FEATURE [PartDesign::CoordinateSystem] Pin
  AttacherType = Attacher::AttachEngine3D
  AttachmentSupport = -> [XY_Plane001]
  MapMode = 5
FEATURE [Sketcher::SketchObject] Sketch052
  ArcFitTolerance = 0
  FullyConstrained = true
  MakeInternals = false
  MapMode = 5
  Placement = pos=(0,0,0) rot=(1,0,0;1.5708rad)
  sketch-geometry (1):
    g0: Circle CenterX=0 CenterY=0 CenterZ=0 NormalX=0 NormalY=0 NormalZ=1 AngleXU=0 Radius=11
  constraints (2):
    c: Coincident(g0,g-1)
    c: Diameter(g0) = 22
FEATURE [PartDesign::Pocket] Pocket032
  BaseFeature = -> Pocket031
  Direction = (0,1,-2e-16)
  Length = 130
  Length2 = 5
  Profile = -> Sketch052
  ReferenceAxis = -> Sketch052 [N_Axis]
  Suppressed = false
  Type = 4
FEATURE [PartDesign::Body] Body071  label="Поршень_2T_92mm"
  AllowCompound = false
  Group = -> [Sketch042,Pad022,Boolean004,Sketch043,Pocket025,Sketch044,Pocket026,Pocket027,Pocket028,Piston001,Sketch049,Pocket030,Pocket031,Sketch052,Pocket032]
  Origin = -> Origin072
  Tip = -> Pocket032
FEATURE [Sketcher::SketchObject] Sketch053
  ArcFitTolerance = 0
  AttachmentOffset = pos=(0,0,-66) rot=(0,0,1;0rad)
  AttachmentSupport = -> [XZ_Plane001]
  FullyConstrained = true
  MakeInternals = false
  MapMode = 5
  Placement = pos=(0,66,-1.47e-14) rot=(1,0,0;1.5708rad)
  sketch-geometry (2):
    g0: Circle CenterX=0 CenterY=0 CenterZ=0 NormalX=0 NormalY=0 NormalZ=1 AngleXU=0 Radius=7.5
    g1: Circle CenterX=0 CenterY=0 CenterZ=0 NormalX=0 NormalY=0 NormalZ=1 AngleXU=0 Radius=5
  constraints (4):
    c: Coincident(g0,g-1)
    c: Coincident(g1,g0)
    c: Diameter(g0) = 15
    c: Diameter(g1) = 10
FEATURE [PartDesign::Pad] Pad
  Direction = (0,-1,2e-16)
  Length = 90
  Length2 = 1
  Placement = pos=(0,0,0) rot=(1,0,0;1.5708rad)
  Profile = -> Sketch053
  ReferenceAxis = -> Sketch053 [N_Axis]
  Reversed = true
  Suppressed = false
  Type = 0
FEATURE [Sketcher::SketchObject] Sketch055
  ArcFitTolerance = 0
  AttachmentOffset = pos=(0,0,-66) rot=(0,0,1;0rad)
  AttachmentSupport = -> [XZ_Plane001]
  FullyConstrained = true
  MakeInternals = false
  MapMode = 5
  Placement = pos=(0,66,-1.47e-14) rot=(1,0,0;1.5708rad)
  sketch-geometry (2):
    g0: Circle CenterX=0 CenterY=0 CenterZ=0 NormalX=0 NormalY=0 NormalZ=1 AngleXU=0 Radius=5
    g1: Circle CenterX=0 CenterY=0 CenterZ=0 NormalX=0 NormalY=0 NormalZ=1 AngleXU=0 Radius=2
  constraints (4):
    c: Diameter(g0) = 10
    c: Coincident(g1,g0)
    c: Coincident(g0,g-1)
    c: Diameter(g1) = 4
FEATURE [PartDesign::Pad] Pad026
  BaseFeature = -> Pad
  Direction = (0,-1,2e-16)
  Length = 5
  Length2 = 17
  Placement = pos=(0,0,0) rot=(1,0,0;1.5708rad)
  Profile = -> Sketch055
  ReferenceAxis = -> Sketch055 [N_Axis]
  Reversed = true
  Suppressed = false
  Type = 4
FEATURE [Sketcher::SketchObject] Sketch058
  ArcFitTolerance = 0
  AttachmentSupport = -> [XY_Plane077]
  FullyConstrained = false
  MakeInternals = false
  MapMode = 5
  sketch-geometry (32):
    g0: LineSegment [constr] StartX=-103 StartY=-65 StartZ=0 EndX=103 EndY=-65 EndZ=0
    g1: LineSegment [constr] StartX=103 StartY=-65 StartZ=0 EndX=103 EndY=65 EndZ=0
    g2: LineSegment [constr] StartX=103 StartY=65 StartZ=0 EndX=-103 EndY=65 EndZ=0
    g3: LineSegment [constr] StartX=-103 StartY=65 StartZ=0 EndX=-103 EndY=-65 EndZ=0
    g4: LineSegment [constr] StartX=-99 StartY=69.5 StartZ=0 EndX=99 EndY=69.5 EndZ=0
    g5: LineSegment [constr] StartX=-103 StartY=65 StartZ=0 EndX=-103 EndY=65.5 EndZ=0
    g6: LineSegment [constr] StartX=103 StartY=65.5 StartZ=0 EndX=103 EndY=65 EndZ=0
    g7: ArcOfCircle [constr] CenterX=-99 CenterY=65.5 CenterZ=0 NormalX=0 NormalY=0 NormalZ=1 AngleXU=0 Radius=4 StartAngle=1.5708 EndAngle=3.14159
    g8: ArcOfCircle [constr] CenterX=99 CenterY=65.5 CenterZ=0 NormalX=0 NormalY=0 NormalZ=1 AngleXU=0 Radius=4 StartAngle=-9e-16 EndAngle=1.5708
    g9: ArcOfCircle [constr] CenterX=-99 CenterY=-65.5 CenterZ=0 NormalX=0 NormalY=0 NormalZ=1 AngleXU=0 Radius=4 StartAngle=3.14159 EndAngle=4.71239
    g10: LineSegment [constr] StartX=-103 StartY=-65 StartZ=0 EndX=-103 EndY=-65.5 EndZ=0
    g11: LineSegment [constr] StartX=-99 StartY=-69.5 StartZ=0 EndX=99 EndY=-69.5 EndZ=0
    g12: ArcOfCircle [constr] CenterX=99 CenterY=-65.5 CenterZ=0 NormalX=0 NormalY=0 NormalZ=1 AngleXU=0 Radius=4 StartAngle=4.71239 EndAngle=6.28319
    g13: LineSegment [constr] StartX=103 StartY=-65.5 StartZ=0 EndX=103 EndY=-65 EndZ=0
    g14: Circle CenterX=-95 CenterY=55 CenterZ=0 NormalX=0 NormalY=0 NormalZ=1 AngleXU=0 Radius=3
    g15: Circle [constr] CenterX=95 CenterY=55 CenterZ=0 NormalX=0 NormalY=0 NormalZ=1 AngleXU=0 Radius=3
    g16: Circle [constr] CenterX=-95 CenterY=-55 CenterZ=0 NormalX=0 NormalY=0 NormalZ=1 AngleXU=0 Radius=3
    g17: Circle [constr] CenterX=95 CenterY=-55 CenterZ=0 NormalX=0 NormalY=0 NormalZ=1 AngleXU=0 Radius=3
    g18: Circle [constr] CenterX=0 CenterY=0 CenterZ=0 NormalX=0 NormalY=0 NormalZ=1 AngleXU=0 Radius=32.25
    g19: LineSegment [constr] StartX=-103 StartY=-65 StartZ=0 EndX=-91.9993 EndY=-65 EndZ=0
    g20: LineSegment [constr] StartX=-91.9993 StartY=-65 StartZ=0 EndX=-91.9993 EndY=-49.9993 EndZ=0
    g21: LineSegment [constr] StartX=-91.9993 StartY=-49.9993 StartZ=0 EndX=-103 EndY=-49.9993 EndZ=0
    g22: LineSegment [constr] StartX=-103 StartY=-49.9993 StartZ=0 EndX=-103 EndY=-65 EndZ=0
    g23: LineSegment [constr] StartX=103 StartY=-65 StartZ=0 EndX=91.9993 EndY=-65 EndZ=0
    g24: LineSegment [constr] StartX=91.9993 StartY=-65 StartZ=0 EndX=91.9993 EndY=-49.9993 EndZ=0
    g25: LineSegment [constr] StartX=91.9993 StartY=-49.9993 StartZ=0 EndX=103 EndY=-49.9993 EndZ=0
    g26: LineSegment [constr] StartX=103 StartY=-49.9993 StartZ=0 EndX=103 EndY=-65 EndZ=0
    g27: LineSegment [constr] StartX=103 StartY=65 StartZ=0 EndX=91.9993 EndY=65 EndZ=0
    g28: LineSegment [constr] StartX=91.9993 StartY=65 StartZ=0 EndX=91.9993 EndY=49.9993 EndZ=0
    g29: LineSegment [constr] StartX=91.9993 StartY=49.9993 StartZ=0 EndX=103 EndY=49.9993 EndZ=0
    g30: LineSegment [constr] StartX=103 StartY=49.9993 StartZ=0 EndX=103 EndY=65 EndZ=0
    g31: Circle CenterX=-95 CenterY=55 CenterZ=0 NormalX=0 NormalY=0 NormalZ=1 AngleXU=0 Radius=8
  constraints (75):
    c: Coincident(g0,g1)
    c: Coincident(g1,g2)
    c: Coincident(g2,g3)
    c: Coincident(g3,g0)
    c: Horizontal(g0)
    c: Vertical(g1)
    c: Symmetric(g2,g1,g-2)
    c: Symmetric(g2,g0,g-1)
    c: DistanceX(g2,g2) = 206
    c: DistanceY(g1,g1) = 130
    c: Coincident(g5,g3)
    c: Coincident(g6,g1)
    c: Tangent(g5,g7) = 1.5708
    c: Tangent(g4,g7) = 1.5708
    c: Tangent(g4,g8) = 1.5708
    c: Tangent(g6,g8) = 1.5708
    c: Vertical(g5)
    c: Vertical(g6)
    c: Symmetric(g7,g8,g-2)
    c: DistanceY(g1,g4) = 4.5
    c: Radius(g8) = 4
    c: Tangent(g10,g9) = -1.5708
    c: Tangent(g11,g9) = -1.5708
    c: Tangent(g11,g12) = -1.5708
    c: Vertical(g10)
    c: Symmetric(g9,g12,g-2)
    c: Symmetric(g9,g7,g-1)
    c: Coincident(g10,g3)
    c: Coincident(g13,g1)
    c: Vertical(g13)
    c: Equal(g13,g10)
    c: Coincident(g12,g13)
    c: Equal(g14,g15)
    c: Equal(g15,g17)
    c: Equal(g17,g16)
    c: Diameter(g15) = 6
    c: Symmetric(g14,g15,g-2)
    c: Symmetric(g16,g17,g-2)
    c: Symmetric(g16,g14,g-1)
    c: DistanceY(g16,g14) = 110
    c: DistanceX(g16,g17) = 190
    c: Coincident(g18,g-1)
    c: Diameter(g18) = 64.5
    c: Coincident(g19,g20)
    c: Coincident(g20,g21)
    c: Coincident(g21,g22)
    c: Coincident(g22,g19)
    c: Horizontal(g19)
    c: Horizontal(g21)
    c: Vertical(g20)
    c: Vertical(g22)
    c: Coincident(g19,g0)
    c: Coincident(g23,g24)
    c: Coincident(g24,g25)
    c: Coincident(g25,g26)
    c: Coincident(g26,g23)
    c: Horizontal(g23)
    c: Horizontal(g25)
    c: Vertical(g24)
    c: Vertical(g26)
    c: Coincident(g23,g0)
    c: Coincident(g27,g28)
    c: Coincident(g28,g29)
    c: Coincident(g29,g30)
    c: Coincident(g30,g27)
    c: Horizontal(g27)
    c: Horizontal(g29)
    c: Vertical(g28)
    c: Vertical(g30)
    c: Coincident(g27,g1)
    c: Equal(g25,g29)
    c: Equal(g28,g24)
    c: Equal(g24,g20)
    c: Coincident(g31,g14)
    c: Tangent(g31,g3)
FEATURE [PartDesign::Pad] Pad029
  Direction = (0,0,1)
  Length = 25
  Length2 = 28.5
  Midplane = true
  Profile = -> Sketch058
  ReferenceAxis = -> Sketch058 [N_Axis]
  Suppressed = false
  Type = 4
FEATURE [PartDesign::CoordinateSystem] Shtok005
  AttacherType = Attacher::AttachEngine3D
  AttachmentSupport = -> [Sketch058]
  MapMode = 2
FEATURE [PartDesign::Body] Body077  label="проставка_корпуса"
  AllowCompound = false
  Group = -> [Sketch058,Pad029,Shtok005]
  Origin = -> Origin078
  Tip = -> Pad029
FEATURE [Sketcher::SketchObject] Sketch060
  ArcFitTolerance = 0
  FullyConstrained = true
  MakeInternals = false
  Placement = pos=(0,0,0) rot=(1,0,0;3.14159rad)
  expr: Constraints[11] = <<Dim_table>>.crank_dia1 + <<Dim_table>>.zazor
  expr: Constraints[14] = <<Dim_table>>.crank_dia2
  expr: Constraints[15] = <<Dim_table>>.inter_shaft_len / 2
  expr: Constraints[6] = <<Dim_table>>.inter_shaft_len
  expr: Constraints[7] = <<Dim_table>>.crank_dia1 * 1.5
  sketch-geometry (7):
    g0: ArcOfCircle CenterX=0 CenterY=0 CenterZ=0 NormalX=0 NormalY=0 NormalZ=1 AngleXU=0 Radius=18.75 StartAngle=1.5708 EndAngle=4.71239
    g1: ArcOfCircle CenterX=100 CenterY=-1.6e-15 CenterZ=0 NormalX=0 NormalY=0 NormalZ=1 AngleXU=0 Radius=18.75 StartAngle=4.71239 EndAngle=7.85398
    g2: LineSegment StartX=-3.4e-15 StartY=-18.75 StartZ=0 EndX=100 EndY=-18.75 EndZ=0
    g3: LineSegment StartX=100 StartY=18.75 StartZ=0 EndX=1.42e-14 EndY=18.75 EndZ=0
    g4: Circle CenterX=0 CenterY=0 CenterZ=0 NormalX=0 NormalY=0 NormalZ=1 AngleXU=0 Radius=12.75
    g5: Circle CenterX=100 CenterY=-1.6e-15 CenterZ=0 NormalX=0 NormalY=0 NormalZ=1 AngleXU=0 Radius=12.75
    g6: Circle CenterX=50 CenterY=0 CenterZ=0 NormalX=0 NormalY=0 NormalZ=1 AngleXU=0 Radius=12.5
  constraints (16):
    c: Tangent(g0,g2) = -1.5708
    c: Tangent(g2,g1) = -1.5708
    c: Tangent(g1,g3) = -1.5708
    c: Tangent(g3,g0) = -1.5708
    c: Equal(g0,g1)
    c: Horizontal(g2)
    c: DistanceX(g0,g1) = 100
    c: Diameter(g0) = 37.5
    c: Coincident(g4,g0)
    c: Coincident(g5,g1)
    c: Equal(g4,g5)
    c: Diameter(g4) = 25.5
    c: Coincident(g0,g-1)
    c: PointOnObject(g6,g-1)
    c: Diameter(g6) = 25
    c: DistanceX(g0,g6) = 50
FEATURE [Sketcher::SketchObject] Sketch061
  ArcFitTolerance = 0
  AttachmentSupport = -> [Pad020]
  FullyConstrained = false
  MakeInternals = false
  MapMode = 5
  Placement = pos=(0,0,22.5) rot=(0,0,1;0rad)
  sketch-geometry (5):
    g0: Circle CenterX=0 CenterY=0 CenterZ=0 NormalX=0 NormalY=0 NormalZ=1 AngleXU=0 Radius=8.25
    g1: LineSegment StartX=-79.3827 StartY=20 StartZ=0 EndX=79.3827 EndY=20 EndZ=0
    g2: LineSegment StartX=79.3827 StartY=20 StartZ=0 EndX=79.3827 EndY=-20 EndZ=0
    g3: LineSegment StartX=79.3827 StartY=-20 StartZ=0 EndX=-79.3827 EndY=-20 EndZ=0
    g4: LineSegment StartX=-79.3827 StartY=-20 StartZ=0 EndX=-79.3827 EndY=20 EndZ=0
  constraints (12):
    c: Coincident(g0,g-1)
    c: Diameter(g0) = 16.5
    c: Coincident(g1,g2)
    c: Coincident(g2,g3)
    c: Coincident(g3,g4)
    c: Coincident(g4,g1)
    c: Horizontal(g1)
    c: Horizontal(g3)
    c: Vertical(g2)
    c: Vertical(g4)
    c: Symmetric(g3,g1,g0)
    c: DistanceY(g2,g2) = 40
FEATURE [PartDesign::Pad] Pad032
  BaseFeature = -> Pad020
  Direction = (0,0,1)
  Length = 16
  Length2 = 10
  Profile = -> Sketch061
  ReferenceAxis = -> Sketch061 [N_Axis]
  Reversed = true
  Suppressed = false
  Type = 0
FEATURE [PartDesign::Body] Body066  label="направляющая_орто_ползуна"
  AllowCompound = false
  Group = -> [Sketch038,Pad020,Shtok003,Sketch061,Pad032]
  Origin = -> Origin067
  Tip = -> Pad032
FEATURE [Spreadsheet::Sheet] Spreadsheet  label="Dim_table"
  cells = A1(crank_dia1)=25; B1='crank_dia1; A2(crank_dia2)=25; B2='crank_dia2; A3(crank_dia3)=16; B3='crank_dia3; A4(crank_len)==85 / 4; B4='crank_len; A5(crank_gear_ecc)=10; B5='crank_gear_ecc; A6(ecc_dia)=80; B6='ecc_dia; A7(ecc_hei)=16.5; B7='ecc_hei; A8(inter_shaft_len)=100; B8='inter_shaft_len; A9(piston_dia)=72; B9='piston_dia; A10(piston_hei)=39; B10='piston_hei; A11(piston_pin_dia)=12; B11='piston_pin_dia; A12(rod_len)=140; B12='rod_len; A13(zazor)=0.5; B13='zazor; A14(delta)=0.05; B14='delta; A15(hex_size)=14; B15='hex_size; A16(fillet_r)=2; B16='fillet_r; A17(axle_hole_dia)=5; B17='axle_hole_dia; A18(roller_dia)=3; B18='roller_dia
FEATURE [Sketcher::SketchObject] Sketch064
  ArcFitTolerance = 0
  FullyConstrained = true
  MakeInternals = false
  Placement = pos=(0,0,0) rot=(1,0,0;3.14159rad)
  expr: Constraints[1] = <<Dim_table>>.inter_shaft_len * 1.2
  sketch-geometry (1):
    g0: Circle CenterX=0 CenterY=0 CenterZ=0 NormalX=0 NormalY=0 NormalZ=1 AngleXU=0 Radius=60
  constraints (2):
    c: Coincident(g0,g-1)
    c: Diameter(g0) = 120
FEATURE [Sketcher::SketchObject] Sketch066
  ArcFitTolerance = 0
  FullyConstrained = false
  MakeInternals = false
  MapMode = 5
  sketch-geometry (40):
    g0: Circle CenterX=-65 CenterY=167.5 CenterZ=0 NormalX=0 NormalY=0 NormalZ=1 AngleXU=0 Radius=3
    g1: Circle CenterX=-76 CenterY=150 CenterZ=0 NormalX=0 NormalY=0 NormalZ=1 AngleXU=0 Radius=3
    g2: ArcOfCircle CenterX=-80 CenterY=159.195 CenterZ=0 NormalX=0 NormalY=0 NormalZ=1 AngleXU=0 Radius=4 StartAngle=2.43396 EndAngle=3.14159
    g3: ArcOfCircle CenterX=-65 CenterY=167.5 CenterZ=0 NormalX=0 NormalY=0 NormalZ=1 AngleXU=0 Radius=10 StartAngle=1.5708 EndAngle=2.43396
    g4: LineSegment StartX=-65 StartY=177.5 StartZ=0 EndX=65 EndY=177.5 EndZ=0
    g5: LineSegment StartX=-57.25 StartY=172.5 StartZ=0 EndX=57.25 EndY=172.5 EndZ=0
    g6: Circle CenterX=-76 CenterY=0 CenterZ=0 NormalX=0 NormalY=0 NormalZ=1 AngleXU=0 Radius=3
    g7: LineSegment StartX=-84 StartY=141.772 StartZ=0 EndX=-57.25 EndY=141.772 EndZ=0
    g8: LineSegment StartX=-57.25 StartY=141.772 StartZ=0 EndX=-57.25 EndY=172.5 EndZ=0
    g9: Circle CenterX=-76 CenterY=0 CenterZ=0 NormalX=0 NormalY=0 NormalZ=1 AngleXU=0 Radius=7.35704
    g10: LineSegment StartX=-72.599 StartY=174 StartZ=0 EndX=-83.0396 EndY=161.795 EndZ=0
    g11: LineSegment StartX=-84 StartY=141.772 StartZ=0 EndX=-84 EndY=159.195 EndZ=0
    g12: Circle CenterX=65 CenterY=167.5 CenterZ=0 NormalX=0 NormalY=0 NormalZ=1 AngleXU=0 Radius=3
    g13: Circle CenterX=76 CenterY=150 CenterZ=0 NormalX=0 NormalY=0 NormalZ=1 AngleXU=0 Radius=3
    g14: ArcOfCircle CenterX=80 CenterY=159.195 CenterZ=0 NormalX=0 NormalY=0 NormalZ=1 AngleXU=0 Radius=4 StartAngle=-1.634e-13 EndAngle=0.707637
    g15: ArcOfCircle CenterX=65 CenterY=167.5 CenterZ=0 NormalX=0 NormalY=0 NormalZ=1 AngleXU=0 Radius=10 StartAngle=0.707637 EndAngle=1.5708
    g16: LineSegment StartX=84 StartY=141.772 StartZ=0 EndX=57.25 EndY=141.772 EndZ=0
    g17: LineSegment StartX=57.25 StartY=141.772 StartZ=0 EndX=57.25 EndY=172.5 EndZ=0
    g18: LineSegment StartX=72.599 StartY=174 StartZ=0 EndX=83.0396 EndY=161.795 EndZ=0
    g19: LineSegment StartX=84 StartY=141.772 StartZ=0 EndX=84 EndY=159.195 EndZ=0
    g20: Circle CenterX=76 CenterY=0 CenterZ=0 NormalX=0 NormalY=0 NormalZ=1 AngleXU=0 Radius=3
    g21: Circle CenterX=76 CenterY=0 CenterZ=0 NormalX=0 NormalY=0 NormalZ=1 AngleXU=0 Radius=7.35704
    g22: Circle CenterX=-65 CenterY=-167.5 CenterZ=0 NormalX=0 NormalY=0 NormalZ=1 AngleXU=0 Radius=3
    g23: Circle CenterX=-76 CenterY=-150 CenterZ=0 NormalX=0 NormalY=0 NormalZ=1 AngleXU=0 Radius=3
    g24: ArcOfCircle CenterX=-80 CenterY=-159.195 CenterZ=0 NormalX=0 NormalY=0 NormalZ=1 AngleXU=0 Radius=4 StartAngle=3.14159 EndAngle=3.84923
    g25: ArcOfCircle CenterX=-65 CenterY=-167.5 CenterZ=0 NormalX=0 NormalY=0 NormalZ=1 AngleXU=0 Radius=10 StartAngle=3.84923 EndAngle=4.71239
    g26: LineSegment StartX=-65 StartY=-177.5 StartZ=0 EndX=65 EndY=-177.5 EndZ=0
    g27: LineSegment StartX=-57.25 StartY=-172.5 StartZ=0 EndX=57.25 EndY=-172.5 EndZ=0
    g28: LineSegment StartX=-84 StartY=-141.772 StartZ=0 EndX=-57.25 EndY=-141.772 EndZ=0
    g29: LineSegment StartX=-57.25 StartY=-141.772 StartZ=0 EndX=-57.25 EndY=-172.5 EndZ=0
    g30: LineSegment StartX=-72.599 StartY=-174 StartZ=0 EndX=-83.0396 EndY=-161.795 EndZ=0
    g31: LineSegment StartX=-84 StartY=-141.772 StartZ=0 EndX=-84 EndY=-159.195 EndZ=0
    g32: Circle CenterX=65 CenterY=-167.5 CenterZ=0 NormalX=0 NormalY=0 NormalZ=1 AngleXU=0 Radius=3
    g33: Circle CenterX=76 CenterY=-150 CenterZ=0 NormalX=0 NormalY=0 NormalZ=1 AngleXU=0 Radius=3
    g34: ArcOfCircle CenterX=80 CenterY=-159.195 CenterZ=0 NormalX=0 NormalY=0 NormalZ=1 AngleXU=0 Radius=4 StartAngle=5.57555 EndAngle=6.28319
    g35: ArcOfCircle CenterX=65 CenterY=-167.5 CenterZ=0 NormalX=0 NormalY=0 NormalZ=1 AngleXU=0 Radius=10 StartAngle=4.71239 EndAngle=5.57555
    g36: LineSegment StartX=84 StartY=-141.772 StartZ=0 EndX=57.25 EndY=-141.772 EndZ=0
    g37: LineSegment StartX=57.25 StartY=-141.772 StartZ=0 EndX=57.25 EndY=-172.5 EndZ=0
    g38: LineSegment StartX=72.599 StartY=-174 StartZ=0 EndX=83.0396 EndY=-161.795 EndZ=0
    g39: LineSegment StartX=84 StartY=-141.772 StartZ=0 EndX=84 EndY=-159.195 EndZ=0
  constraints (44):
    c: Coincident(g0,g-6)
    c: Coincident(g1,g-7)
    c: Equal(g-7,g1)
    c: Equal(g-6,g0)
    c: Coincident(g2,g-10)
    c: Coincident(g2,g-11)
    c: Coincident(g3,g-5)
    c: Coincident(g4,g3)
    c: Coincident(g5,g-9)
    c: Coincident(g6,g-12)
    c: Equal(g-12,g6)
    c: Horizontal(g7)
    c: Coincident(g8,g7)
    c: Coincident(g8,g5)
    c: Coincident(g9,g6)
    c: Coincident(g5,g-9)
    c: Coincident(g4,g-3)
    c: Tangent(g3,g-4) = -1.5708
    c: Coincident(g10,g3)
    c: Tangent(g2,g10) = -1.5708
    c: Coincident(g11,g7)
    c: Tangent(g11,g2) = 1.5708
    c: PointOnObject(g7,g-8)
    c: Horizontal(g16)
    c: Coincident(g17,g16)
    c: Coincident(g18,g15)
    c: Tangent(g14,g18) = 1.5708
    c: Coincident(g19,g16)
    c: Tangent(g19,g14) = -1.5708
    c: Coincident(g21,g20)
    c: Coincident(g26,g25)
    c: Horizontal(g28)
    c: Coincident(g29,g28)
    c: Coincident(g29,g27)
    c: Coincident(g30,g25)
    c: Tangent(g24,g30) = 1.5708
    c: Coincident(g31,g28)
    c: Tangent(g31,g24) = -1.5708
    c: Horizontal(g36)
    c: Coincident(g37,g36)
    c: Coincident(g38,g35)
    c: Tangent(g34,g38) = -1.5708
    c: Coincident(g39,g36)
    c: Tangent(g39,g34) = 1.5708
FEATURE [Part::Extrusion] Extrude  label="проставка ползуна_001"
  Base = -> Sketch066
  Dir = (0,0,1)
  DirMode = 2
  FaceMakerClass = Part::FaceMakerBullseye
  FaceMakerMode = 3
  LengthFwd = 26.75
  LengthRev = 0
  Reversed = true
  Solid = true
  Symmetric = false
FEATURE [Sketcher::SketchObject] Sketch067
  ArcFitTolerance = 0
  AttachmentSupport = -> [XY_Plane085]
  FullyConstrained = true
  MakeInternals = false
  MapMode = 5
  expr: Constraints[14] = <<Dim_table>>.inter_shaft_len * 2.15
  expr: Constraints[15] = <<Dim_table>>.ecc_dia * 1.2
  expr: Constraints[16] = <<Dim_table>>.inter_shaft_len * 1.85
  expr: Constraints[22] = <<Dim_table>>.inter_shaft_len / 2
  expr: Constraints[37] = <<Dim_table>>.inter_shaft_len * 2.35
  expr: Constraints[38] = <<Dim_table>>.crank_dia2
  expr: Constraints[39] = <<Dim_table>>.inter_shaft_len * 2
  expr: Constraints[45] = <<Dim_table>>.inter_shaft_len / 2
  expr: Constraints[53] = <<Dim_table>>.axle_hole_dia
  expr: Constraints[56] = <<Dim_table>>.inter_shaft_len
  expr: Constraints[58] = <<Dim_table>>.crank_dia2 + <<Dim_table>>.zazor
  sketch-geometry (27):
    g0: LineSegment [constr] StartX=-9.5 StartY=-92.5 StartZ=0 EndX=109.5 EndY=-92.5 EndZ=0
    g1: LineSegment [constr] StartX=157.5 StartY=-44.5 StartZ=0 EndX=157.5 EndY=44.5 EndZ=0
    g2: LineSegment [constr] StartX=109.5 StartY=92.5 StartZ=0 EndX=-9.5 EndY=92.5 EndZ=0
    g3: LineSegment [constr] StartX=-57.5 StartY=44.5 StartZ=0 EndX=-57.5 EndY=-44.5 EndZ=0
    g4: ArcOfCircle [constr] CenterX=-9.5 CenterY=44.5 CenterZ=0 NormalX=0 NormalY=0 NormalZ=1 AngleXU=0 Radius=48 StartAngle=1.5708 EndAngle=3.14159
    g5: ArcOfCircle [constr] CenterX=109.5 CenterY=44.5 CenterZ=0 NormalX=0 NormalY=0 NormalZ=1 AngleXU=0 Radius=48 StartAngle=0 EndAngle=1.5708
    g6: ArcOfCircle [constr] CenterX=-9.5 CenterY=-44.5 CenterZ=0 NormalX=0 NormalY=0 NormalZ=1 AngleXU=0 Radius=48 StartAngle=3.14159 EndAngle=4.71239
    g7: ArcOfCircle [constr] CenterX=109.5 CenterY=-44.5 CenterZ=0 NormalX=0 NormalY=0 NormalZ=1 AngleXU=0 Radius=48 StartAngle=4.71239 EndAngle=6.28319
    g8: LineSegment [constr] StartX=-57.5 StartY=-44.5 StartZ=0 EndX=157.5 EndY=44.5 EndZ=0
    g9: GeomPoint [constr] X=50 Y=0 Z=0
    g10: ArcOfCircle CenterX=-55 CenterY=87.5 CenterZ=0 NormalX=0 NormalY=0 NormalZ=1 AngleXU=0 Radius=12.5 StartAngle=1.5708 EndAngle=3.14159
    g11: LineSegment StartX=155 StartY=100 StartZ=0 EndX=-55 EndY=100 EndZ=0
    g12: ArcOfCircle CenterX=155 CenterY=87.5 CenterZ=0 NormalX=0 NormalY=0 NormalZ=1 AngleXU=0 Radius=12.5 StartAngle=7.02e-14 EndAngle=1.5708
    g13: LineSegment StartX=167.5 StartY=-87.5 StartZ=0 EndX=167.5 EndY=87.5 EndZ=0
    g14: ArcOfCircle CenterX=155 CenterY=-87.5 CenterZ=0 NormalX=0 NormalY=0 NormalZ=1 AngleXU=0 Radius=12.5 StartAngle=4.71239 EndAngle=6.28319
    g15: LineSegment StartX=-55 StartY=-100 StartZ=0 EndX=155 EndY=-100 EndZ=0
    g16: ArcOfCircle CenterX=-55 CenterY=-87.5 CenterZ=0 NormalX=0 NormalY=0 NormalZ=1 AngleXU=0 Radius=12.5 StartAngle=3.14159 EndAngle=4.71239
    g17: LineSegment StartX=-67.5 StartY=87.5 StartZ=0 EndX=-67.5 EndY=-87.5 EndZ=0
    g18: LineSegment [constr] StartX=-55 StartY=100 StartZ=0 EndX=155 EndY=-100 EndZ=0
    g19: GeomPoint [constr] X=50 Y=0 Z=0
    g20: Circle CenterX=-55 CenterY=87.5 CenterZ=0 NormalX=0 NormalY=0 NormalZ=1 AngleXU=0 Radius=2.5
    g21: Circle CenterX=155 CenterY=87.5 CenterZ=0 NormalX=0 NormalY=0 NormalZ=1 AngleXU=0 Radius=2.5
    g22: Circle CenterX=-55 CenterY=-87.5 CenterZ=0 NormalX=0 NormalY=0 NormalZ=1 AngleXU=0 Radius=2.5
    g23: Circle CenterX=155 CenterY=-87.5 CenterZ=0 NormalX=0 NormalY=0 NormalZ=1 AngleXU=0 Radius=2.5
    g24: Circle CenterX=0 CenterY=0 CenterZ=0 NormalX=0 NormalY=0 NormalZ=1 AngleXU=0 Radius=12.75
    g25: Circle CenterX=100 CenterY=0 CenterZ=0 NormalX=0 NormalY=0 NormalZ=1 AngleXU=0 Radius=12.75
    g26: Circle CenterX=50 CenterY=0 CenterZ=0 NormalX=0 NormalY=0 NormalZ=1 AngleXU=0 Radius=12.75
  constraints (61):
    c: Horizontal(g0)
    c: Horizontal(g2)
    c: Vertical(g1)
    c: Vertical(g3)
    c: Tangent(g2,g4) = -1.5708
    c: Tangent(g3,g4) = -1.5708
    c: Tangent(g2,g5) = -1.5708
    c: Tangent(g1,g5) = -1.5708
    c: Tangent(g3,g6) = -1.5708
    c: Tangent(g0,g6) = -1.5708
    c: Tangent(g0,g7) = -1.5708
    c: Tangent(g1,g7) = -1.5708
    c: Equal(g4,g5)
    c: Equal(g5,g7)
    c: DistanceX(g3,g1) = 215
    c: Diameter(g4) = 96
    c: DistanceY(g0,g2) = 185
    c: Symmetric(g2,g0,g-1)
    c: Coincident(g8,g3)
    c: Coincident(g8,g1)
    c: PointOnObject(g9,g-1)
    c: PointOnObject(g9,g8)
    c: DistanceX(g-1,g9) = 50
    c: Horizontal(g15)
    c: Horizontal(g11)
    c: Vertical(g13)
    c: Vertical(g17)
    c: Tangent(g11,g10) = -1.5708
    c: Tangent(g17,g10) = -1.5708
    c: Tangent(g11,g12) = -1.5708
    c: Tangent(g13,g12) = -1.5708
    c: Tangent(g17,g16) = -1.5708
    c: Tangent(g15,g16) = -1.5708
    c: Tangent(g15,g14) = -1.5708
    c: Tangent(g13,g14) = -1.5708
    c: Equal(g10,g12)
    c: Equal(g12,g14)
    c: DistanceX(g17,g13) = 235
    c: Diameter(g10) = 25
    c: DistanceY(g15,g11) = 200
    c: Symmetric(g10,g16,g-1)
    c: Coincident(g18,g10)
    c: Coincident(g18,g14)
    c: PointOnObject(g19,g-1)
    c: PointOnObject(g19,g18)
    c: DistanceX(g-1,g19) = 50
    c: Coincident(g20,g10)
    c: Coincident(g21,g12)
    c: Coincident(g22,g16)
    c: Coincident(g23,g14)
    c: Equal(g22,g23)
    c: Equal(g23,g21)
    c: Equal(g21,g20)
    c: Diameter(g20) = 5
    c: Coincident(g24,g-1)
    c: PointOnObject(g25,g-1)
    c: DistanceX(g24,g25) = 100
    c: Equal(g25,g24)
    c: Diameter(g24) = 25.5
    c: Coincident(g26,g9)
    c: Equal(g24,g26)
FEATURE [PartDesign::CoordinateSystem] LCS_Origin006
  AttacherType = Attacher::AttachEngine3D
  AttachmentSupport = -> [X_Axis083]
  MapMode = 2
FEATURE [PartDesign::Pad] Pad036
  Direction = (0,0,1)
  Length = 4
  Length2 = 10
  Profile = -> Sketch067
  ReferenceAxis = -> Sketch067 [N_Axis]
  Suppressed = false
  Type = 0
FEATURE [Part::FeaturePython] InvoluteGear006  label="crank_gear_01-1"  # WARN: FeaturePython — macro-defined, semantics opaque (R4)
  AttacherType = Attacher::AttachEngine3D
  addendum_diameter = 47.5
  angular_backlash = 0
  axle_hole = true
  axle_holesize = 25.5
  backlash = 0
  clearance = 0.25
  double_helix = false
  head = 0
  head_fillet = 0
  height = 10
  helix_angle = 0
  module = 2.5
  num_teeth = 17
  numpoints = 20
  offset_hole = true
  offset_holeoffset = 20
  offset_holesize = 1
  pitch_diameter = 42.5
  pressure_angle = 20
  properties_from_tool = false
  reversed_backlash = false
  root_diameter = 36.25
  root_fillet = 0
  shift = 0
  simple = false
  transverse_pitch = 7.85398
  traverse_module = 2.5
  undercut = false
  version = 1.3.0
  expr: angular_backlash = backlash / pitch_diameter * 360 ° / pi
  expr: axle_holesize = <<Dim_table>>.crank_dia2 + <<Dim_table>>.zazor
FEATURE [Part::FeaturePython] InternalInvoluteGear001  label="crank_int_gear_01-1"  # WARN: FeaturePython — macro-defined, semantics opaque (R4)
  AttacherType = Attacher::AttachEngine3D
  addendum_diameter = 82
  angular_backlash = 0
  backlash = 0
  clearance = 0.25
  double_helix = false
  head = -0.4
  head_fillet = 0
  height = 10
  helix_angle = 0
  module = 2.5
  num_teeth = 34
  numpoints = 20
  outside_diameter = 100
  pitch_diameter = 85
  pressure_angle = 20
  properties_from_tool = false
  reversed_backlash = false
  root_diameter = 91.25
  root_fillet = 0
  shift = 0
  simple = false
  thickness = 7.5
  transverse_pitch = 7.85398
  version = 1.3.0
  expr: angular_backlash = backlash / pitch_diameter * 360 ° / pi
FEATURE [PartDesign::FeatureBase] BaseFeature
  BaseFeature = -> InvoluteGear006
  Suppressed = false
FEATURE [PartDesign::FeatureBase] BaseFeature001
  BaseFeature = -> InternalInvoluteGear001
  Suppressed = false
FEATURE [PartDesign::CoordinateSystem] Local_CS004
  AttacherType = Attacher::AttachEngine3D
  AttachmentSupport = -> [BaseFeature001]
  MapMode = 2
FEATURE [PartDesign::Body] Body088  label="crank_int_gear_01"
  AllowCompound = false
  BaseFeature = -> InternalInvoluteGear001
  Group = -> [BaseFeature001,Local_CS004]
  Origin = -> Origin091
  Tip = -> BaseFeature001
FEATURE [PartDesign::CoordinateSystem] Local_CS005
  AttacherType = Attacher::AttachEngine3D
  AttachmentOffset = pos=(0,0,0) rot=(0,0,1;0.279253rad)
  AttachmentSupport = -> [BaseFeature]
  MapMode = 2
  Placement = pos=(0,0,0) rot=(0,0,1;0.279253rad)
FEATURE [PartDesign::CoordinateSystem] LCS_6  label="crank"
  AttacherType = Attacher::AttachEngine3D
  AttachmentSupport = -> [Main]
  MapMode = 7
  Placement = pos=(0,0,0) rot=(1,0,0;1.5708rad)
FEATURE [PartDesign::CoordinateSystem] crank2_axle  label="ecc"
  AttacherType = Attacher::AttachEngine3D
  AttachmentSupport = -> [Main]
  MapMode = 7
  Placement = pos=(-2.63e-14,21.25,0) rot=(1,0,0;1.5708rad)
  expr: .Placement.Base.x = <<Dim_table>>.inter_shaft_len
FEATURE [PartDesign::CoordinateSystem] Shtok_rama  label="shtok1"
  AttacherType = Attacher::AttachEngine3D
  AttachmentSupport = -> [Main]
  MapMode = 1
  Placement = pos=(-2e-15,42.5,0) rot=(0,0,1;0rad)
FEATURE [App::Link] _____________________________  label="Колевал (секция)001"
  AttachedBy = #Crank_shaft
  AttachedTo = Parent Assembly#LCS_Origin
  AttachmentOffset = pos=(0,0,-28) rot=(0,0,1;-1.5708rad)
  LinkPlacement = pos=(0,0,0.5) rot=(0,0,1;3.14159rad)
  LinkedObject = -> Body057
  Placement = pos=(0,0,0.5) rot=(0,0,1;3.14159rad)
  SolverId = Asm4EE
  expr: .AttachmentOffset.Rotation.Angle = -<<Variables>>.Crank_Angle - 90
  expr: Placement = LCS_Origin.Placement * AttachmentOffset * Crank_shaft.Placement ^ -1
FEATURE [Sketcher::SketchObject] Sketch070
  ArcFitTolerance = 0
  AttachmentSupport = -> [Pad003]
  FullyConstrained = true
  MakeInternals = false
  MapMode = 11
  Placement = pos=(0,-21.25,63) rot=(0,0,1;1.5708rad)
  expr: Constraints[12] = <<Dim_table>>.crank_dia2
  expr: Constraints[13] = <<Dim_table>>.axle_hole_dia
  expr: Constraints[14] = 0
  expr: Constraints[3] = <<Dim_table>>.crank_dia2 * 0.8
  sketch-geometry (5):
    g0: ArcOfCircle CenterX=0 CenterY=0 CenterZ=0 NormalX=0 NormalY=0 NormalZ=1 AngleXU=0 Radius=12.5 StartAngle=0.643501 EndAngle=2.49809
    g1: ArcOfCircle CenterX=0 CenterY=0 CenterZ=0 NormalX=0 NormalY=0 NormalZ=1 AngleXU=0 Radius=12.5 StartAngle=3.78509 EndAngle=5.63968
    g2: LineSegment StartX=10 StartY=7.5 StartZ=0 EndX=10 EndY=-7.5 EndZ=0
    g3: LineSegment StartX=-10 StartY=7.5 StartZ=0 EndX=-10 EndY=-7.5 EndZ=0
    g4: Circle CenterX=0 CenterY=0 CenterZ=0 NormalX=0 NormalY=0 NormalZ=1 AngleXU=0 Radius=2.5
  constraints (15):
    c: Coincident(g2,g0)
    c: Coincident(g2,g1)
    c: Vertical(g2)
    c: DistanceX(g0,g0) = 20
    c: Coincident(g3,g0)
    c: Coincident(g3,g1)
    c: Vertical(g3)
    c: Equal(g3,g2)
    c: Equal(g1,g0)
    c: Coincident(g1,g0)
    c: Coincident(g4,g0)
    c: PointOnObject(g0,g-2)
    c: Diameter(g0) = 25
    c: Diameter(g4) = 5
    c: DistanceY(g-1,g0) = 0
FEATURE [PartDesign::Pad] Pad038
  BaseFeature = -> Pad003
  Direction = (0,0,1)
  Length = 12
  Length2 = 10
  Profile = -> Sketch070
  ReferenceAxis = -> Sketch070 [N_Axis]
  Suppressed = false
  TaperAngle = -2
  Type = 0
FEATURE [PartDesign::Body] Body003  label="Шейка_шатунная"
  AllowCompound = false
  Group = -> [Sketch004,Pad003,Sketch070,Pad038]
  Origin = -> Origin004
  Placement = pos=(0,0,-25) rot=(0,0,1;0rad)
  Tip = -> Pad038
FEATURE [PartDesign::FeatureBase] Clone002
  BaseFeature = -> Body003
  Suppressed = false
FEATURE [PartDesign::Body] Body052
  AllowCompound = false
  Group = -> [Clone002]
  Origin = -> Origin053
  Placement = pos=(0,0,-35.5) rot=(0,0,1;0rad)
  Tip = -> Clone002
FEATURE [Part::MultiFuse] Fusion  label="Колевал (секция) Сбор"
  Placement = pos=(0,0,-49) rot=(0,0,1;0rad)
  Shapes = -> [Body052,Body054,Body055]
FEATURE [PartDesign::FeatureBase] Clone007
  BaseFeature = -> Fusion
  Suppressed = false
FEATURE [PartDesign::CoordinateSystem] Crank_shaft
  AttacherType = Attacher::AttachEngine3D
  AttachmentSupport = -> [Clone007]
  MapMode = 11
  Placement = pos=(0,0,-28.5) rot=(0,0,1;1.5708rad)
FEATURE [Sketcher::SketchObject] Sketch071
  ArcFitTolerance = 0
  FullyConstrained = true
  MakeInternals = false
  MapMode = 5
  expr: Constraints[0] = <<Dim_table>>.crank_dia2
  expr: Constraints[3] = <<Dim_table>>.axle_hole_dia
  sketch-geometry (2):
    g0: Circle CenterX=0 CenterY=0 CenterZ=0 NormalX=0 NormalY=0 NormalZ=1 AngleXU=0 Radius=12.5
    g1: Circle CenterX=0 CenterY=0 CenterZ=0 NormalX=0 NormalY=0 NormalZ=1 AngleXU=0 Radius=2.5
  constraints (4):
    c: Diameter(g0) = 25
    c: Coincident(g0,g-1)
    c: Coincident(g1,g0)
    c: Diameter(g1) = 5
FEATURE [PartDesign::Pad] Pad039
  Direction = (0,0,1)
  Length = 26
  Length2 = 10
  Profile = -> Sketch071
  ReferenceAxis = -> Sketch071 [N_Axis]
  Suppressed = false
  Type = 0
FEATURE [Sketcher::SketchObject] Sketch072
  ArcFitTolerance = 0
  AttachmentSupport = -> [XY_Plane094]
  FullyConstrained = true
  MakeInternals = false
  MapMode = 5
  expr: Constraints[17] = <<Dim_table>>.fillet_r
  expr: Constraints[18] = <<Dim_table>>.fillet_r
  expr: Constraints[23] = <<Dim_table>>.axle_hole_dia
  expr: Constraints[24] = 70
  expr: Constraints[25] = <<Dim_table>>.crank_dia2 * 1.5
  expr: Constraints[26] = <<Dim_table>>.crank_len
  sketch-geometry (14):
    g0: ArcOfCircle CenterX=0 CenterY=0 CenterZ=0 NormalX=0 NormalY=0 NormalZ=1 AngleXU=0 Radius=52.5 StartAngle=0.0396143 EndAngle=3.10198
    g1: ArcOfCircle CenterX=3e-16 CenterY=-21.25 CenterZ=0 NormalX=0 NormalY=0 NormalZ=1 AngleXU=0 Radius=18.75 StartAngle=3.49066 EndAngle=5.93412
    g2: LineSegment [constr] StartX=-17.6192 StartY=-27.6629 StartZ=0 EndX=17.6192 EndY=-27.6629 EndZ=0
    g3: LineSegment StartX=-50.4604 StartY=0 StartZ=0 EndX=-29.0881 EndY=0 EndZ=0
    g4: LineSegment StartX=-27.2087 StartY=-1.31596 StartZ=0 EndX=-17.6192 EndY=-27.6629 EndZ=0
    g5: LineSegment StartX=17.6192 StartY=-27.6629 StartZ=0 EndX=27.2087 EndY=-1.31596 EndZ=0
    g6: LineSegment StartX=29.0881 StartY=2.9e-15 StartZ=0 EndX=50.4604 EndY=2.9e-15 EndZ=0
    g7: ArcOfCircle CenterX=-29.0881 CenterY=-2 CenterZ=0 NormalX=0 NormalY=0 NormalZ=1 AngleXU=0 Radius=2 StartAngle=0.349066 EndAngle=1.5708
    g8: ArcOfCircle CenterX=29.0881 CenterY=-2 CenterZ=0 NormalX=0 NormalY=0 NormalZ=1 AngleXU=0 Radius=2 StartAngle=1.5708 EndAngle=2.79253
    g9: ArcOfCircle CenterX=50.4604 CenterY=2 CenterZ=0 NormalX=0 NormalY=0 NormalZ=1 AngleXU=0 Radius=2 StartAngle=4.71239 EndAngle=6.3228
    g10: ArcOfCircle CenterX=-50.4604 CenterY=2 CenterZ=0 NormalX=0 NormalY=0 NormalZ=1 AngleXU=0 Radius=2 StartAngle=3.10198 EndAngle=4.71239
    g11: Circle [constr] CenterX=0 CenterY=0 CenterZ=0 NormalX=0 NormalY=0 NormalZ=1 AngleXU=0 Radius=52.5
    g12: Circle CenterX=0 CenterY=0 CenterZ=0 NormalX=0 NormalY=0 NormalZ=1 AngleXU=0 Radius=2.5
    g13: Circle CenterX=3e-16 CenterY=-21.25 CenterZ=0 NormalX=0 NormalY=0 NormalZ=1 AngleXU=0 Radius=2.5
  constraints (31):
    c: Coincident(g2,g1)
    c: Coincident(g2,g1)
    c: Horizontal(g2)
    c: Horizontal(g3)
    c: Horizontal(g6)
    c: Tangent(g4,g1) = -1.5708
    c: Tangent(g5,g1) = -1.5708
    c: Tangent(g3,g7) = 1.5708
    c: Tangent(g4,g7) = 1.5708
    c: Tangent(g6,g8) = 1.5708
    c: Tangent(g5,g8) = 1.5708
    c: Tangent(g6,g9) = -1.5708
    c: Tangent(g0,g9) = -1.5708
    c: Tangent(g0,g10) = -1.5708
    c: Tangent(g3,g10) = -1.5708
    c: Symmetric(g7,g8,g-2)
    c: Symmetric(g10,g9,g-2)
    c: Radius(g10) = 2
    c: Radius(g7) = 2
    c: Coincident(g0,g-1)
    c: Coincident(g11,g0)
    c: Diameter(g11) = 105
    c: Coincident(g12,g11)
    c: Diameter(g12) = 5
    c: Angle(g5) = 1.22173
    c: Diameter(g1) = 37.5
    c: DistanceY(g1,g12) = 21.25
    c: PointOnObject(g3,g-1)
    c: Coincident(g13,g1)
    c: Equal(g13,g12)
    c: Equal(g0,g11)
FEATURE [PartDesign::Pad] Pad040
  BaseFeature = -> Pad039
  Direction = (0,0,1)
  Length = 15
  Length2 = 10
  Profile = -> Sketch072
  ReferenceAxis = -> Sketch072 [N_Axis]
  Reversed = true
  Suppressed = false
  Type = 0
FEATURE [PartDesign::Chamfer] Chamfer001
  Angle = 45
  Base = -> Pad040 [Edge14]
  BaseFeature = -> Pad040
  ChamferType = 0
  FlipDirection = false
  Size = 1.5
  Size2 = 1
  SupportTransform = false
  Suppressed = false
  UseAllEdges = false
FEATURE [PartDesign::Body] Body090  label="Шейка_и_щека_задняя"
  AllowCompound = false
  Group = -> [Sketch071,Pad039,Sketch072,Pad040,Chamfer001]
  Origin = -> Origin093
  Placement = pos=(0,0,-6.5) rot=(0,0,1;0rad)
  Tip = -> Chamfer001
FEATURE [Part::Cut] Cut  label="Шейка_и_щека_задняя001"
  Base = -> Body090
  Tool = -> Fusion
FEATURE [PartDesign::FeatureBase] Clone
  BaseFeature = -> Cut
  Suppressed = false
FEATURE [PartDesign::CoordinateSystem] LCS_2
  AttacherType = Attacher::AttachEngine3D
  AttachmentSupport = -> [Cut]
  MapMode = 11
  Placement = pos=(0,0,-21.5) rot=(0,0,1;1.5708rad)
FEATURE [App::Link] ____________________________________cl  label="Шейка_и_щека_задняя_cl001"
  AttachedBy = #LCS_2
  AttachedTo = Parent Assembly#LCS_Origin
  AttachmentOffset = pos=(0,0,28) rot=(0,0,1;-1.5708rad)
  LinkPlacement = pos=(0,0,49.5) rot=(0,0,1;3.14159rad)
  LinkedObject = -> Body091
  Placement = pos=(0,0,49.5) rot=(0,0,1;3.14159rad)
  SolverId = Asm4EE
  expr: .AttachmentOffset.Rotation.Angle = -<<Variables>>.Crank_Angle - 90
  expr: Placement = LCS_Origin.Placement * AttachmentOffset * LCS_2.Placement ^ -1
FEATURE [Sketcher::SketchObject] Sketch073
  ArcFitTolerance = 0
  AttachmentSupport = -> [XY_Plane085]
  FullyConstrained = true
  MakeInternals = false
  MapMode = 5
  expr: Constraints[6] = <<Dim_table>>.crank_dia2 + <<Dim_table>>.zazor
  expr: Constraints[7] = <<Dim_table>>.crank_dia2 * 1.5
  expr: Constraints[8] = <<Dim_table>>.inter_shaft_len
  sketch-geometry (4):
    g0: Circle CenterX=0 CenterY=0 CenterZ=0 NormalX=0 NormalY=0 NormalZ=1 AngleXU=0 Radius=12.75
    g1: Circle CenterX=0 CenterY=0 CenterZ=0 NormalX=0 NormalY=0 NormalZ=1 AngleXU=0 Radius=18.75
    g2: Circle CenterX=100 CenterY=0 CenterZ=0 NormalX=0 NormalY=0 NormalZ=1 AngleXU=0 Radius=12.75
    g3: Circle CenterX=100 CenterY=0 CenterZ=0 NormalX=0 NormalY=0 NormalZ=1 AngleXU=0 Radius=18.75
  constraints (9):
    c: Coincident(g0,g-1)
    c: Coincident(g1,g0)
    c: PointOnObject(g2,g-1)
    c: Coincident(g3,g2)
    c: Equal(g0,g2)
    c: Equal(g1,g3)
    c: Diameter(g0) = 25.5
    c: Diameter(g1) = 37.5
    c: DistanceX(g-1,g2) = 100
FEATURE [PartDesign::Pad] Pad041
  BaseFeature = -> Pad036
  Direction = (0,0,1)
  Length = 10
  Length2 = 10
  Profile = -> Sketch073
  ReferenceAxis = -> Sketch073 [N_Axis]
  Suppressed = false
  Type = 0
FEATURE [PartDesign::Body] ___________________________  label="корпус_верхний"
  AllowCompound = false
  Group = -> [LCS_Origin006,Sketch067,Pad036,Sketch073,Pad041]
  Origin = -> Origin084
  Tip = -> Pad041
FEATURE [Sketcher::SketchObject] Sketch074
  ArcFitTolerance = 0
  AttachmentSupport = -> [XY_Plane076]
  FullyConstrained = true
  MakeInternals = false
  MapMode = 5
  expr: Constraints[14] = <<Dim_table>>.ecc_dia * 1.2
  expr: Constraints[33] = <<Dim_table>>.crank_dia2
  expr: Constraints[34] = <<Dim_table>>.inter_shaft_len * 2.2
  expr: Constraints[46] = <<Dim_table>>.axle_hole_dia
  expr: Constraints[48] = 32
  expr: Constraints[53] = <<Dim_table>>.inter_shaft_len * 1.8
  sketch-geometry (25):
    g0: LineSegment [constr] StartX=-42 StartY=-90 StartZ=0 EndX=42 EndY=-90 EndZ=0
    g1: LineSegment [constr] StartX=90 StartY=-42 StartZ=0 EndX=90 EndY=42 EndZ=0
    g2: LineSegment [constr] StartX=42 StartY=90 StartZ=0 EndX=-42 EndY=90 EndZ=0
    g3: LineSegment [constr] StartX=-90 StartY=42 StartZ=0 EndX=-90 EndY=-42 EndZ=0
    g4: ArcOfCircle [constr] CenterX=-42 CenterY=42 CenterZ=0 NormalX=0 NormalY=0 NormalZ=1 AngleXU=0 Radius=48 StartAngle=1.5708 EndAngle=3.14159
    g5: ArcOfCircle [constr] CenterX=42 CenterY=42 CenterZ=0 NormalX=0 NormalY=0 NormalZ=1 AngleXU=0 Radius=48 StartAngle=1e-16 EndAngle=1.5708
    g6: ArcOfCircle [constr] CenterX=-42 CenterY=-42 CenterZ=0 NormalX=0 NormalY=0 NormalZ=1 AngleXU=0 Radius=48 StartAngle=3.14159 EndAngle=4.71239
    g7: ArcOfCircle [constr] CenterX=42 CenterY=-42 CenterZ=0 NormalX=0 NormalY=0 NormalZ=1 AngleXU=0 Radius=48 StartAngle=4.71239 EndAngle=6.28319
    g8: LineSegment [constr] StartX=-90 StartY=-42 StartZ=0 EndX=90 EndY=42 EndZ=0
    g9: GeomPoint [constr] X=0 Y=0 Z=0
    g10: ArcOfCircle CenterX=-97.5 CenterY=97.5 CenterZ=0 NormalX=0 NormalY=0 NormalZ=1 AngleXU=0 Radius=12.5 StartAngle=1.5708 EndAngle=3.14159
    g11: LineSegment StartX=97.5 StartY=110 StartZ=0 EndX=-97.5 EndY=110 EndZ=0
    g12: ArcOfCircle CenterX=97.5 CenterY=97.5 CenterZ=0 NormalX=0 NormalY=0 NormalZ=1 AngleXU=0 Radius=12.5 StartAngle=4.16e-13 EndAngle=1.5708
    g13: LineSegment StartX=110 StartY=-97.5 StartZ=0 EndX=110 EndY=97.5 EndZ=0
    g14: ArcOfCircle CenterX=97.5 CenterY=-97.5 CenterZ=0 NormalX=0 NormalY=0 NormalZ=1 AngleXU=0 Radius=12.5 StartAngle=4.71239 EndAngle=6.28319
    g15: LineSegment StartX=-97.5 StartY=-110 StartZ=0 EndX=97.5 EndY=-110 EndZ=0
    g16: ArcOfCircle CenterX=-97.5 CenterY=-97.5 CenterZ=0 NormalX=0 NormalY=0 NormalZ=1 AngleXU=0 Radius=12.5 StartAngle=3.14159 EndAngle=4.71239
    g17: LineSegment StartX=-110 StartY=97.5 StartZ=0 EndX=-110 EndY=-97.5 EndZ=0
    g18: LineSegment [constr] StartX=-97.5 StartY=110 StartZ=0 EndX=97.5 EndY=-110 EndZ=0
    g19: GeomPoint [constr] X=0 Y=0 Z=0
    g20: Circle CenterX=-97.5 CenterY=97.5 CenterZ=0 NormalX=0 NormalY=0 NormalZ=1 AngleXU=0 Radius=2.5
    g21: Circle CenterX=97.5 CenterY=97.5 CenterZ=0 NormalX=0 NormalY=0 NormalZ=1 AngleXU=0 Radius=2.5
    g22: Circle CenterX=-97.5 CenterY=-97.5 CenterZ=0 NormalX=0 NormalY=0 NormalZ=1 AngleXU=0 Radius=2.5
    g23: Circle CenterX=97.5 CenterY=-97.5 CenterZ=0 NormalX=0 NormalY=0 NormalZ=1 AngleXU=0 Radius=2.5
    g24: Circle CenterX=0 CenterY=0 CenterZ=0 NormalX=0 NormalY=0 NormalZ=1 AngleXU=0 Radius=16
  constraints (54):
    c: Horizontal(g0)
    c: Horizontal(g2)
    c: Vertical(g1)
    c: Vertical(g3)
    c: Tangent(g2,g4) = -1.5708
    c: Tangent(g3,g4) = -1.5708
    c: Tangent(g2,g5) = -1.5708
    c: Tangent(g1,g5) = -1.5708
    c: Tangent(g3,g6) = -1.5708
    c: Tangent(g0,g6) = -1.5708
    c: Tangent(g0,g7) = -1.5708
    c: Tangent(g1,g7) = -1.5708
    c: Equal(g4,g5)
    c: Equal(g5,g7)
    c: Diameter(g4) = 96
    c: Symmetric(g2,g0,g-1)
    c: Coincident(g8,g3)
    c: Coincident(g8,g1)
    c: PointOnObject(g9,g8)
    c: Horizontal(g15)
    c: Horizontal(g11)
    c: Vertical(g13)
    c: Vertical(g17)
    c: Tangent(g11,g10) = -1.5708
    c: Tangent(g17,g10) = -1.5708
    c: Tangent(g11,g12) = -1.5708
    c: Tangent(g13,g12) = -1.5708
    c: Tangent(g17,g16) = -1.5708
    c: Tangent(g15,g16) = -1.5708
    c: Tangent(g15,g14) = -1.5708
    c: Tangent(g13,g14) = -1.5708
    c: Equal(g10,g12)
    c: Equal(g12,g14)
    c: Diameter(g10) = 25
    c: DistanceY(g15,g11) = 220
    c: Symmetric(g10,g16,g-1)
    c: Coincident(g18,g10)
    c: Coincident(g18,g14)
    c: PointOnObject(g19,g18)
    c: Coincident(g20,g10)
    c: Coincident(g21,g12)
    c: Coincident(g22,g16)
    c: Coincident(g23,g14)
    c: Equal(g22,g23)
    c: Equal(g23,g21)
    c: Equal(g21,g20)
    c: Diameter(g20) = 5
    c: Coincident(g24,g9)
    c: Diameter(g24) = 32
    c: Coincident(g9,g19)
    c: Coincident(g-1,g9)
    c: Equal(g11,g13)
    c: Equal(g2,g1)
    c: DistanceX(g3,g1) = 180
FEATURE [PartDesign::CoordinateSystem] Shtok004
  AttacherType = Attacher::AttachEngine3D
  AttachmentSupport = -> [Sketch074]
  MapMode = 2
FEATURE [PartDesign::Pad] Pad042
  Direction = (0,0,1)
  Length = 15
  Length2 = 10
  Profile = -> Sketch074
  ReferenceAxis = -> Sketch074 [N_Axis]
  Reversed = true
  Suppressed = false
  Type = 0
FEATURE [PartDesign::Pad] Pad043
  BaseFeature = -> Pad042
  Direction = (0,-1e-16,-1)
  Length = 25
  Length2 = 10
  Profile = -> Sketch060
  ReferenceAxis = -> Sketch060 [N_Axis]
  Suppressed = false
  Type = 0
FEATURE [PartDesign::Pocket] Pocket036
  BaseFeature = -> Pad043
  Direction = (0,1e-16,1)
  Length = 10.5
  Length2 = 5
  Profile = -> Sketch064
  ReferenceAxis = -> Sketch064 [N_Axis]
  Reversed = true
  Suppressed = false
  Type = 0
FEATURE [PartDesign::Body] Body076  label="корпус_нижний"
  AllowCompound = false
  Group = -> [Shtok004,Sketch060,Sketch064,Sketch074,Pad042,Pad043,Pocket036]
  Origin = -> Origin077
  Tip = -> Pocket036
FEATURE [App::Link] _________________________  label="корпус_нижний001"
  AttachedBy = #Shtok004
  AttachedTo = Parent Assembly#LCS_Origin
  AttachmentOffset = pos=(0,0,-5.25) rot=(0,0,1;0rad)
  LinkPlacement = pos=(0,0,-5.25) rot=(0,0,1;0rad)
  LinkedObject = -> Body076
  Placement = pos=(0,0,-5.25) rot=(0,0,1;0rad)
  SolverId = Asm4EE
  expr: Placement = LCS_Origin.Placement * AttachmentOffset * Shtok004.Placement ^ -1
FEATURE [App::Link] ___________________________002  label="корпус_верхний001"
  AttachedBy = #LCS_Origin006
  AttachedTo = Parent Assembly#LCS_Origin
  AttachmentOffset = pos=(0,0,22) rot=(0,0,1;0rad)
  LinkPlacement = pos=(0,0,22) rot=(0,0,1;0rad)
  LinkedObject = -> ___________________________
  Placement = pos=(0,0,22) rot=(0,0,1;0rad)
  SolverId = Asm4EE
  expr: Placement = LCS_Origin.Placement * AttachmentOffset * LCS_Origin006.Placement ^ -1
FEATURE [Sketcher::SketchObject] Sketch075
  ArcFitTolerance = 0
  AttachmentSupport = -> [XY_Plane096]
  FullyConstrained = true
  MakeInternals = false
  MapMode = 5
  expr: Constraints[14] = <<Dim_table>>.inter_shaft_len * 2.15
  expr: Constraints[15] = <<Dim_table>>.ecc_dia * 1.2
  expr: Constraints[16] = <<Dim_table>>.inter_shaft_len * 1.85
  expr: Constraints[22] = <<Dim_table>>.inter_shaft_len / 2
  expr: Constraints[37] = <<Dim_table>>.inter_shaft_len * 2.35
  expr: Constraints[38] = <<Dim_table>>.crank_dia2
  expr: Constraints[39] = <<Dim_table>>.inter_shaft_len * 2
  expr: Constraints[45] = <<Dim_table>>.inter_shaft_len / 2
  expr: Constraints[53] = <<Dim_table>>.axle_hole_dia
  expr: Constraints[56] = <<Dim_table>>.inter_shaft_len
  expr: Constraints[58] = <<Dim_table>>.inter_shaft_len * 0.95
  sketch-geometry (26):
    g0: LineSegment [constr] StartX=-9.5 StartY=-92.5 StartZ=0 EndX=109.5 EndY=-92.5 EndZ=0
    g1: LineSegment [constr] StartX=157.5 StartY=-44.5 StartZ=0 EndX=157.5 EndY=44.5 EndZ=0
    g2: LineSegment [constr] StartX=109.5 StartY=92.5 StartZ=0 EndX=-9.5 EndY=92.5 EndZ=0
    g3: LineSegment [constr] StartX=-57.5 StartY=44.5 StartZ=0 EndX=-57.5 EndY=-44.5 EndZ=0
    g4: ArcOfCircle [constr] CenterX=-9.5 CenterY=44.5 CenterZ=0 NormalX=0 NormalY=0 NormalZ=1 AngleXU=0 Radius=48 StartAngle=1.5708 EndAngle=3.14159
    g5: ArcOfCircle [constr] CenterX=109.5 CenterY=44.5 CenterZ=0 NormalX=0 NormalY=0 NormalZ=1 AngleXU=0 Radius=48 StartAngle=0 EndAngle=1.5708
    g6: ArcOfCircle [constr] CenterX=-9.5 CenterY=-44.5 CenterZ=0 NormalX=0 NormalY=0 NormalZ=1 AngleXU=0 Radius=48 StartAngle=3.14159 EndAngle=4.71239
    g7: ArcOfCircle [constr] CenterX=109.5 CenterY=-44.5 CenterZ=0 NormalX=0 NormalY=0 NormalZ=1 AngleXU=0 Radius=48 StartAngle=4.71239 EndAngle=6.28319
    g8: LineSegment [constr] StartX=-57.5 StartY=-44.5 StartZ=0 EndX=157.5 EndY=44.5 EndZ=0
    g9: GeomPoint [constr] X=50 Y=0 Z=0
    g10: ArcOfCircle CenterX=-55 CenterY=87.5 CenterZ=0 NormalX=0 NormalY=0 NormalZ=1 AngleXU=0 Radius=12.5 StartAngle=1.5708 EndAngle=3.14159
    g11: LineSegment StartX=155 StartY=100 StartZ=0 EndX=-55 EndY=100 EndZ=0
    g12: ArcOfCircle CenterX=155 CenterY=87.5 CenterZ=0 NormalX=0 NormalY=0 NormalZ=1 AngleXU=0 Radius=12.5 StartAngle=7.01e-14 EndAngle=1.5708
    g13: LineSegment StartX=167.5 StartY=-87.5 StartZ=0 EndX=167.5 EndY=87.5 EndZ=0
    g14: ArcOfCircle CenterX=155 CenterY=-87.5 CenterZ=0 NormalX=0 NormalY=0 NormalZ=1 AngleXU=0 Radius=12.5 StartAngle=4.71239 EndAngle=6.28319
    g15: LineSegment StartX=-55 StartY=-100 StartZ=0 EndX=155 EndY=-100 EndZ=0
    g16: ArcOfCircle CenterX=-55 CenterY=-87.5 CenterZ=0 NormalX=0 NormalY=0 NormalZ=1 AngleXU=0 Radius=12.5 StartAngle=3.14159 EndAngle=4.71239
    g17: LineSegment StartX=-67.5 StartY=87.5 StartZ=0 EndX=-67.5 EndY=-87.5 EndZ=0
    g18: LineSegment [constr] StartX=-55 StartY=100 StartZ=0 EndX=155 EndY=-100 EndZ=0
    g19: GeomPoint [constr] X=50 Y=0 Z=0
    g20: Circle CenterX=-55 CenterY=87.5 CenterZ=0 NormalX=0 NormalY=0 NormalZ=1 AngleXU=0 Radius=2.5
    g21: Circle CenterX=155 CenterY=87.5 CenterZ=0 NormalX=0 NormalY=0 NormalZ=1 AngleXU=0 Radius=2.5
    g22: Circle CenterX=-55 CenterY=-87.5 CenterZ=0 NormalX=0 NormalY=0 NormalZ=1 AngleXU=0 Radius=2.5
    g23: Circle CenterX=155 CenterY=-87.5 CenterZ=0 NormalX=0 NormalY=0 NormalZ=1 AngleXU=0 Radius=2.5
    g24: Circle CenterX=0 CenterY=0 CenterZ=0 NormalX=0 NormalY=0 NormalZ=1 AngleXU=0 Radius=47.5
    g25: Circle CenterX=100 CenterY=0 CenterZ=0 NormalX=0 NormalY=0 NormalZ=1 AngleXU=0 Radius=47.5
  constraints (59):
    c: Horizontal(g0)
    c: Horizontal(g2)
    c: Vertical(g1)
    c: Vertical(g3)
    c: Tangent(g2,g4) = -1.5708
    c: Tangent(g3,g4) = -1.5708
    c: Tangent(g2,g5) = -1.5708
    c: Tangent(g1,g5) = -1.5708
    c: Tangent(g3,g6) = -1.5708
    c: Tangent(g0,g6) = -1.5708
    c: Tangent(g0,g7) = -1.5708
    c: Tangent(g1,g7) = -1.5708
    c: Equal(g4,g5)
    c: Equal(g5,g7)
    c: DistanceX(g3,g1) = 215
    c: Diameter(g4) = 96
    c: DistanceY(g0,g2) = 185
    c: Symmetric(g2,g0,g-1)
    c: Coincident(g8,g3)
    c: Coincident(g8,g1)
    c: PointOnObject(g9,g-1)
    c: PointOnObject(g9,g8)
    c: DistanceX(g-1,g9) = 50
    c: Horizontal(g15)
    c: Horizontal(g11)
    c: Vertical(g13)
    c: Vertical(g17)
    c: Tangent(g11,g10) = -1.5708
    c: Tangent(g17,g10) = -1.5708
    c: Tangent(g11,g12) = -1.5708
    c: Tangent(g13,g12) = -1.5708
    c: Tangent(g17,g16) = -1.5708
    c: Tangent(g15,g16) = -1.5708
    c: Tangent(g15,g14) = -1.5708
    c: Tangent(g13,g14) = -1.5708
    c: Equal(g10,g12)
    c: Equal(g12,g14)
    c: DistanceX(g17,g13) = 235
    c: Diameter(g10) = 25
    c: DistanceY(g15,g11) = 200
    c: Symmetric(g10,g16,g-1)
    c: Coincident(g18,g10)
    c: Coincident(g18,g14)
    c: PointOnObject(g19,g-1)
    c: PointOnObject(g19,g18)
    c: DistanceX(g-1,g19) = 50
    c: Coincident(g20,g10)
    c: Coincident(g21,g12)
    c: Coincident(g22,g16)
    c: Coincident(g23,g14)
    c: Equal(g22,g23)
    c: Equal(g23,g21)
    c: Equal(g21,g20)
    c: Diameter(g20) = 5
    c: Coincident(g24,g-1)
    c: PointOnObject(g25,g-1)
    c: DistanceX(g24,g25) = 100
    c: Equal(g25,g24)
    c: Diameter(g24) = 95
FEATURE [Sketcher::SketchObject] Sketch076
  ArcFitTolerance = 0
  AttachmentSupport = -> [XY_Plane096]
  FullyConstrained = true
  MakeInternals = false
  MapMode = 5
  expr: Constraints[14] = <<Dim_table>>.inter_shaft_len * 2.15
  expr: Constraints[15] = <<Dim_table>>.ecc_dia * 1.2
  expr: Constraints[16] = <<Dim_table>>.inter_shaft_len * 1.85
  expr: Constraints[22] = <<Dim_table>>.inter_shaft_len / 2
  expr: Constraints[37] = <<Dim_table>>.inter_shaft_len * 2.35
  expr: Constraints[38] = <<Dim_table>>.crank_dia2
  expr: Constraints[39] = <<Dim_table>>.inter_shaft_len * 2
  expr: Constraints[45] = <<Dim_table>>.inter_shaft_len / 2
  expr: Constraints[53] = <<Dim_table>>.axle_hole_dia
  sketch-geometry (24):
    g0: LineSegment StartX=-9.5 StartY=-92.5 StartZ=0 EndX=109.5 EndY=-92.5 EndZ=0
    g1: LineSegment StartX=157.5 StartY=-44.5 StartZ=0 EndX=157.5 EndY=44.5 EndZ=0
    g2: LineSegment StartX=109.5 StartY=92.5 StartZ=0 EndX=-9.5 EndY=92.5 EndZ=0
    g3: LineSegment StartX=-57.5 StartY=44.5 StartZ=0 EndX=-57.5 EndY=-44.5 EndZ=0
    g4: ArcOfCircle CenterX=-9.5 CenterY=44.5 CenterZ=0 NormalX=0 NormalY=0 NormalZ=1 AngleXU=0 Radius=48 StartAngle=1.5708 EndAngle=3.14159
    g5: ArcOfCircle CenterX=109.5 CenterY=44.5 CenterZ=0 NormalX=0 NormalY=0 NormalZ=1 AngleXU=0 Radius=48 StartAngle=0 EndAngle=1.5708
    g6: ArcOfCircle CenterX=-9.5 CenterY=-44.5 CenterZ=0 NormalX=0 NormalY=0 NormalZ=1 AngleXU=0 Radius=48 StartAngle=3.14159 EndAngle=4.71239
    g7: ArcOfCircle CenterX=109.5 CenterY=-44.5 CenterZ=0 NormalX=0 NormalY=0 NormalZ=1 AngleXU=0 Radius=48 StartAngle=4.71239 EndAngle=6.28319
    g8: LineSegment [constr] StartX=-57.5 StartY=-44.5 StartZ=0 EndX=157.5 EndY=44.5 EndZ=0
    g9: GeomPoint [constr] X=50 Y=0 Z=0
    g10: ArcOfCircle CenterX=-55 CenterY=87.5 CenterZ=0 NormalX=0 NormalY=0 NormalZ=1 AngleXU=0 Radius=12.5 StartAngle=1.5708 EndAngle=3.14159
    g11: LineSegment StartX=155 StartY=100 StartZ=0 EndX=-55 EndY=100 EndZ=0
    g12: ArcOfCircle CenterX=155 CenterY=87.5 CenterZ=0 NormalX=0 NormalY=0 NormalZ=1 AngleXU=0 Radius=12.5 StartAngle=7e-14 EndAngle=1.5708
    g13: LineSegment StartX=167.5 StartY=-87.5 StartZ=0 EndX=167.5 EndY=87.5 EndZ=0
    g14: ArcOfCircle CenterX=155 CenterY=-87.5 CenterZ=0 NormalX=0 NormalY=0 NormalZ=1 AngleXU=0 Radius=12.5 StartAngle=4.71239 EndAngle=6.28319
    g15: LineSegment StartX=-55 StartY=-100 StartZ=0 EndX=155 EndY=-100 EndZ=0
    g16: ArcOfCircle CenterX=-55 CenterY=-87.5 CenterZ=0 NormalX=0 NormalY=0 NormalZ=1 AngleXU=0 Radius=12.5 StartAngle=3.14159 EndAngle=4.71239
    g17: LineSegment StartX=-67.5 StartY=87.5 StartZ=0 EndX=-67.5 EndY=-87.5 EndZ=0
    g18: LineSegment [constr] StartX=-55 StartY=100 StartZ=0 EndX=155 EndY=-100 EndZ=0
    g19: GeomPoint [constr] X=50 Y=0 Z=0
    g20: Circle CenterX=-55 CenterY=87.5 CenterZ=0 NormalX=0 NormalY=0 NormalZ=1 AngleXU=0 Radius=2.5
    g21: Circle CenterX=155 CenterY=87.5 CenterZ=0 NormalX=0 NormalY=0 NormalZ=1 AngleXU=0 Radius=2.5
    g22: Circle CenterX=-55 CenterY=-87.5 CenterZ=0 NormalX=0 NormalY=0 NormalZ=1 AngleXU=0 Radius=2.5
    g23: Circle CenterX=155 CenterY=-87.5 CenterZ=0 NormalX=0 NormalY=0 NormalZ=1 AngleXU=0 Radius=2.5
  constraints (54):
    c: Horizontal(g0)
    c: Horizontal(g2)
    c: Vertical(g1)
    c: Vertical(g3)
    c: Tangent(g2,g4) = -1.5708
    c: Tangent(g3,g4) = -1.5708
    c: Tangent(g2,g5) = -1.5708
    c: Tangent(g1,g5) = -1.5708
    c: Tangent(g3,g6) = -1.5708
    c: Tangent(g0,g6) = -1.5708
    c: Tangent(g0,g7) = -1.5708
    c: Tangent(g1,g7) = -1.5708
    c: Equal(g4,g5)
    c: Equal(g5,g7)
    c: DistanceX(g3,g1) = 215
    c: Diameter(g4) = 96
    c: DistanceY(g0,g2) = 185
    c: Symmetric(g2,g0,g-1)
    c: Coincident(g8,g3)
    c: Coincident(g8,g1)
    c: PointOnObject(g9,g-1)
    c: PointOnObject(g9,g8)
    c: DistanceX(g-1,g9) = 50
    c: Horizontal(g15)
    c: Horizontal(g11)
    c: Vertical(g13)
    c: Vertical(g17)
    c: Tangent(g11,g10) = -1.5708
    c: Tangent(g17,g10) = -1.5708
    c: Tangent(g11,g12) = -1.5708
    c: Tangent(g13,g12) = -1.5708
    c: Tangent(g17,g16) = -1.5708
    c: Tangent(g15,g16) = -1.5708
    c: Tangent(g15,g14) = -1.5708
    c: Tangent(g13,g14) = -1.5708
    c: Equal(g10,g12)
    c: Equal(g12,g14)
    c: DistanceX(g17,g13) = 235
    c: Diameter(g10) = 25
    c: DistanceY(g15,g11) = 200
    c: Symmetric(g10,g16,g-1)
    c: Coincident(g18,g10)
    c: Coincident(g18,g14)
    c: PointOnObject(g19,g-1)
    c: PointOnObject(g19,g18)
    c: DistanceX(g-1,g19) = 50
    c: Coincident(g20,g10)
    c: Coincident(g21,g12)
    c: Coincident(g22,g16)
    c: Coincident(g23,g14)
    c: Equal(g22,g23)
    c: Equal(g23,g21)
    c: Equal(g21,g20)
    c: Diameter(g20) = 5
FEATURE [PartDesign::CoordinateSystem] LCS_Origin007
  AttacherType = Attacher::AttachEngine3D
  AttachmentSupport = -> [X_Axis094]
  MapMode = 2
FEATURE [PartDesign::Pad] Pad044
  Direction = (0,0,1)
  Length = 6
  Length2 = 10
  Profile = -> Sketch075
  ReferenceAxis = -> Sketch075 [N_Axis]
  Suppressed = false
  Type = 0
FEATURE [PartDesign::Pad] Pad045
  BaseFeature = -> Pad044
  Direction = (0,0,1)
  Length = 16.75
  Length2 = 10
  Profile = -> Sketch076
  ReferenceAxis = -> Sketch076 [N_Axis]
  Suppressed = false
  Type = 0
FEATURE [PartDesign::Body] Body_2  label="проставка_корпуса_с_шестернями"
  AllowCompound = false
  Group = -> [LCS_Origin007,Sketch075,Pad044,Sketch076,Pad045]
  Origin = -> Origin095
  Tip = -> Pad045
FEATURE [App::Link] _________________________________________________________  label="проставка_корпуса_с_шестернями001"
  AttachedBy = #LCS_Origin007
  AttachedTo = Parent Assembly#LCS_Origin
  AttachmentOffset = pos=(0,0,5.25) rot=(0,0,1;0rad)
  LinkPlacement = pos=(0,0,5.25) rot=(0,0,1;0rad)
  LinkedObject = -> Body_2
  Placement = pos=(0,0,5.25) rot=(0,0,1;0rad)
  SolverId = Asm4EE
  expr: Placement = LCS_Origin.Placement * AttachmentOffset * LCS_Origin007.Placement ^ -1
FEATURE [Sketcher::SketchObject] Sketch077
  ArcFitTolerance = 0
  AttachmentSupport = -> [XY_Plane096]
  FullyConstrained = true
  MakeInternals = false
  MapMode = 5
  expr: Constraints[14] = <<Dim_table>>.inter_shaft_len * 2.15
  expr: Constraints[15] = <<Dim_table>>.ecc_dia * 1.2
  expr: Constraints[16] = <<Dim_table>>.inter_shaft_len * 1.85
  expr: Constraints[22] = <<Dim_table>>.inter_shaft_len / 2
  expr: Constraints[37] = <<Dim_table>>.inter_shaft_len * 2.35
  expr: Constraints[38] = <<Dim_table>>.crank_dia2
  expr: Constraints[39] = <<Dim_table>>.inter_shaft_len * 2
  expr: Constraints[45] = <<Dim_table>>.inter_shaft_len / 2
  expr: Constraints[53] = <<Dim_table>>.axle_hole_dia
  sketch-geometry (36):
    g0: LineSegment [constr] StartX=-9.5 StartY=-92.5 StartZ=0 EndX=109.5 EndY=-92.5 EndZ=0
    g1: LineSegment StartX=157.5 StartY=-44.5 StartZ=0 EndX=157.5 EndY=44.5 EndZ=0
    g2: LineSegment [constr] StartX=109.5 StartY=92.5 StartZ=0 EndX=-9.5 EndY=92.5 EndZ=0
    g3: LineSegment StartX=-57.5 StartY=44.5 StartZ=0 EndX=-57.5 EndY=-44.5 EndZ=0
    g4: ArcOfCircle CenterX=-9.5 CenterY=44.5 CenterZ=0 NormalX=0 NormalY=0 NormalZ=1 AngleXU=0 Radius=48 StartAngle=1.5708 EndAngle=3.14159
    g5: ArcOfCircle CenterX=109.5 CenterY=44.5 CenterZ=0 NormalX=0 NormalY=0 NormalZ=1 AngleXU=0 Radius=48 StartAngle=0 EndAngle=1.5708
    g6: ArcOfCircle CenterX=-9.5 CenterY=-44.5 CenterZ=0 NormalX=0 NormalY=0 NormalZ=1 AngleXU=0 Radius=48 StartAngle=3.14159 EndAngle=4.71239
    g7: ArcOfCircle CenterX=109.5 CenterY=-44.5 CenterZ=0 NormalX=0 NormalY=0 NormalZ=1 AngleXU=0 Radius=48 StartAngle=4.71239 EndAngle=6.28319
    g8: LineSegment [constr] StartX=-57.5 StartY=-44.5 StartZ=0 EndX=157.5 EndY=44.5 EndZ=0
    g9: GeomPoint [constr] X=50 Y=0 Z=0
    g10: ArcOfCircle CenterX=-55 CenterY=87.5 CenterZ=0 NormalX=0 NormalY=0 NormalZ=1 AngleXU=0 Radius=12.5 StartAngle=1.5708 EndAngle=3.14159
    g11: LineSegment [constr] StartX=155 StartY=100 StartZ=0 EndX=-55 EndY=100 EndZ=0
    g12: ArcOfCircle CenterX=155 CenterY=87.5 CenterZ=0 NormalX=0 NormalY=0 NormalZ=1 AngleXU=0 Radius=12.5 StartAngle=1.549e-13 EndAngle=1.5708
    g13: LineSegment StartX=167.5 StartY=-87.5 StartZ=0 EndX=167.5 EndY=87.5 EndZ=0
    g14: ArcOfCircle CenterX=155 CenterY=-87.5 CenterZ=0 NormalX=0 NormalY=0 NormalZ=1 AngleXU=0 Radius=12.5 StartAngle=4.71239 EndAngle=6.28319
    g15: LineSegment [constr] StartX=-55 StartY=-100 StartZ=0 EndX=155 EndY=-100 EndZ=0
    g16: ArcOfCircle CenterX=-55 CenterY=-87.5 CenterZ=0 NormalX=0 NormalY=0 NormalZ=1 AngleXU=0 Radius=12.5 StartAngle=3.14159 EndAngle=4.71239
    g17: LineSegment StartX=-67.5 StartY=87.5 StartZ=0 EndX=-67.5 EndY=-87.5 EndZ=0
    g18: LineSegment [constr] StartX=-55 StartY=100 StartZ=0 EndX=155 EndY=-100 EndZ=0
    g19: GeomPoint [constr] X=50 Y=0 Z=0
    g20: Circle CenterX=-55 CenterY=87.5 CenterZ=0 NormalX=0 NormalY=0 NormalZ=1 AngleXU=0 Radius=2.5
    g21: Circle CenterX=155 CenterY=87.5 CenterZ=0 NormalX=0 NormalY=0 NormalZ=1 AngleXU=0 Radius=2.5
    g22: Circle CenterX=-55 CenterY=-87.5 CenterZ=0 NormalX=0 NormalY=0 NormalZ=1 AngleXU=0 Radius=2.5
    g23: Circle CenterX=155 CenterY=-87.5 CenterZ=0 NormalX=0 NormalY=0 NormalZ=1 AngleXU=0 Radius=2.5
    g24: LineSegment StartX=-9.5 StartY=-92.5 StartZ=0 EndX=-2 EndY=-92.5 EndZ=0
    g25: LineSegment StartX=-2 StartY=-92.5 StartZ=0 EndX=-2 EndY=-100 EndZ=0
    g26: LineSegment StartX=-2 StartY=-100 StartZ=0 EndX=-55 EndY=-100 EndZ=0
    g27: LineSegment StartX=102 StartY=-92.5 StartZ=0 EndX=102 EndY=-100 EndZ=0
    g28: LineSegment StartX=102 StartY=-100 StartZ=0 EndX=155 EndY=-100 EndZ=0
    g29: LineSegment StartX=102 StartY=-92.5 StartZ=0 EndX=109.5 EndY=-92.5 EndZ=0
    g30: LineSegment StartX=-9.5 StartY=92.5 StartZ=0 EndX=-2 EndY=92.5 EndZ=0
    g31: LineSegment StartX=-2 StartY=92.5 StartZ=0 EndX=-2 EndY=100 EndZ=0
    g32: LineSegment StartX=-2 StartY=100 StartZ=0 EndX=-55 EndY=100 EndZ=0
    g33: LineSegment StartX=109.5 StartY=92.5 StartZ=0 EndX=102 EndY=92.5 EndZ=0
    g34: LineSegment StartX=102 StartY=92.5 StartZ=0 EndX=102 EndY=100 EndZ=0
    g35: LineSegment StartX=102 StartY=100 StartZ=0 EndX=155 EndY=100 EndZ=0
  constraints (84):
    c: Horizontal(g0)
    c: Horizontal(g2)
    c: Vertical(g1)
    c: Vertical(g3)
    c: Tangent(g2,g4) = -1.5708
    c: Tangent(g3,g4) = -1.5708
    c: Tangent(g2,g5) = -1.5708
    c: Tangent(g1,g5) = -1.5708
    c: Tangent(g3,g6) = -1.5708
    c: Tangent(g0,g6) = -1.5708
    c: Tangent(g0,g7) = -1.5708
    c: Tangent(g1,g7) = -1.5708
    c: Equal(g4,g5)
    c: Equal(g5,g7)
    c: DistanceX(g3,g1) = 215
    c: Diameter(g4) = 96
    c: DistanceY(g0,g2) = 185
    c: Symmetric(g2,g0,g-1)
    c: Coincident(g8,g3)
    c: Coincident(g8,g1)
    c: PointOnObject(g9,g-1)
    c: PointOnObject(g9,g8)
    c: DistanceX(g-1,g9) = 50
    c: Horizontal(g15)
    c: Horizontal(g11)
    c: Vertical(g13)
    c: Vertical(g17)
    c: Tangent(g11,g10) = -1.5708
    c: Tangent(g17,g10) = -1.5708
    c: Tangent(g11,g12) = -1.5708
    c: Tangent(g13,g12) = -1.5708
    c: Tangent(g17,g16) = -1.5708
    c: Tangent(g15,g16) = -1.5708
    c: Tangent(g15,g14) = -1.5708
    c: Tangent(g13,g14) = -1.5708
    c: Equal(g10,g12)
    c: Equal(g12,g14)
    c: DistanceX(g17,g13) = 235
    c: Diameter(g10) = 25
    c: DistanceY(g15,g11) = 200
    c: Symmetric(g10,g16,g-1)
    c: Coincident(g18,g10)
    c: Coincident(g18,g14)
    c: PointOnObject(g19,g-1)
    c: PointOnObject(g19,g18)
    c: DistanceX(g-1,g19) = 50
    c: Coincident(g20,g10)
    c: Coincident(g21,g12)
    c: Coincident(g22,g16)
    c: Coincident(g23,g14)
    c: Equal(g22,g23)
    c: Equal(g23,g21)
    c: Equal(g21,g20)
    c: Diameter(g20) = 5
    c: Coincident(g24,g6)
    c: Coincident(g25,g24)
    c: Coincident(g26,g25)
    c: Coincident(g26,g16)
    c: Coincident(g28,g27)
    c: Coincident(g28,g14)
    c: Coincident(g29,g27)
    c: Coincident(g29,g7)
    c: Coincident(g30,g4)
    c: Coincident(g31,g30)
    c: Coincident(g32,g31)
    c: Coincident(g32,g10)
    c: Coincident(g33,g5)
    c: Coincident(g34,g33)
    c: Coincident(g35,g34)
    c: Coincident(g35,g12)
    c: Vertical(g31)
    c: Vertical(g34)
    c: Horizontal(g32)
    c: Horizontal(g35)
    c: Horizontal(g33)
    c: Horizontal(g30)
    c: Horizontal(g28)
    c: Horizontal(g26)
    c: Vertical(g25)
    c: Vertical(g27)
    c: Symmetric(g24,g33,g9)
    c: Symmetric(g30,g27,g9)
    c: Equal(g26,g28)
    c: Equal(g34,g33)
FEATURE [Part::Extrusion] Extrude001  label="проставка_корпуса_штока"
  Base = -> Sketch077
  Dir = (0,0,1)
  DirMode = 2
  FaceMakerClass = Part::FaceMakerBullseye
  FaceMakerMode = 3
  LengthFwd = 10.5
  LengthRev = 0
  Solid = true
  Symmetric = false
FEATURE [PartDesign::FeatureBase] BaseFeature003
  BaseFeature = -> Extrude001
  Suppressed = false
FEATURE [PartDesign::CoordinateSystem] LCS_3
  AttacherType = Attacher::AttachEngine3D
  AttachmentSupport = -> [BaseFeature003]
  MapMode = 2
FEATURE [PartDesign::Body] Body092  label="проставка_корпуса_штока1"
  AllowCompound = false
  BaseFeature = -> Extrude001
  Group = -> [BaseFeature003,LCS_3]
  Origin = -> Origin096
  Tip = -> BaseFeature003
FEATURE [App::Link] ____________________________________________1  label="проставка_корпуса_штока002"
  AttachedBy = #LCS_3
  AttachedTo = Parent Assembly#LCS_Origin
  AttachmentOffset = pos=(0,0,-5.25) rot=(0,0,1;0rad)
  LinkPlacement = pos=(0,0,-5.25) rot=(0,0,1;0rad)
  LinkedObject = -> Body092
  Placement = pos=(0,0,-5.25) rot=(0,0,1;0rad)
  SolverId = Asm4EE
  expr: Placement = LCS_Origin.Placement * AttachmentOffset * LCS_3.Placement ^ -1
FEATURE [Mesh::Feature] Mesh006  label="polzun"
FEATURE [Mesh::Feature] Mesh011  label="crank_pad_rear001"
FEATURE [Mesh::Feature] Mesh012  label="crank_pad_rear002"
FEATURE [Mesh::Feature] Mesh013  label="case_btm"
FEATURE [Mesh::Feature] Mesh014  label="case_top"
FEATURE [Mesh::Feature] Mesh016  label="case_shtok"
FEATURE [Mesh::Feature] Mesh017  label="ecc1"
FEATURE [Mesh::Feature] Mesh018  label="ecc2"
FEATURE [Mesh::Feature] Mesh019  label="case_gear1"
FEATURE [Mesh::Feature] Mesh  label="crank1"
FEATURE [Mesh::Feature] Mesh020  label="crank2"
FEATURE [Mesh::Feature] Mesh021  label="ruchka"
FEATURE [App::DocumentObjectGroup] Group001  label="Meshes"
  Group = -> [Mesh006,Mesh011,Mesh012,Mesh013,Mesh014,Mesh016,Mesh017,Mesh018,Mesh019,Mesh,Mesh020,Mesh021]
FEATURE [PartDesign::CoordinateSystem] shtok2
  AttacherType = Attacher::AttachEngine3D
  AttachmentSupport = -> [Main]
  MapMode = 7
  Placement = pos=(-4.66e-14,1.23e-14,0) rot=(0.57735,-0.57735,-0.57735;2.0944rad)
FEATURE [PartDesign::AdditiveCylinder] Cylinder
  Angle = 360
  AttacherType = Attacher::AttachEngine3D
  AttachmentOffset = pos=(41.5,0,6.9) rot=(0,0,1;0rad)
  AttachmentSupport = -> [XY_Plane099]
  FirstAngle = 0
  Height = 13.8
  MapMode = 5
  Placement = pos=(41.5,0,6.9) rot=(0,0,1;0rad)
  Radius = 1.5
  Refine = true
  SecondAngle = 0
  Suppressed = false
  expr: .AttachmentOffset.Base.x = <<Dim_table>>.ecc_dia / 2 + 3 / 2
  expr: .AttachmentOffset.Base.z = 13.8 / 2
FEATURE [App::Link] crank_gear_002  label="crank_gear_003"
  AttachedBy = #Local_CS005
  AttachedTo = Parent Assembly#crank2_axle
  AttachmentOffset = pos=(0,-17,0) rot=(1,0,0;1.5708rad)
  LinkPlacement = pos=(-2.63e-14,21.25,-17) rot=(0.990268,0.139173,0;3.14159rad)
  LinkedObject = -> Body087
  Placement = pos=(-2.63e-14,21.25,-17) rot=(0.990268,0.139173,0;3.14159rad)
  SolverId = Asm4EE
  expr: Placement = crank2_axle.Placement * AttachmentOffset * Local_CS005.Placement ^ -1
FEATURE [App::Link] crank_int_gear_01  label="crank_int_gear_003"
  AttachedBy = #Local_CS004
  AttachedTo = Parent Assembly#LCS_Origin
  AttachmentOffset = pos=(0,0,-27) rot=(0,0,1;0rad)
  LinkPlacement = pos=(0,0,-27) rot=(0,0,1;0rad)
  LinkedObject = -> Body088
  Placement = pos=(0,0,-27) rot=(0,0,1;0rad)
  SolverId = Asm4EE
  expr: Placement = LCS_Origin.Placement * AttachmentOffset * Local_CS004.Placement ^ -1
FEATURE [App::Link] crank_int_gear_002
  AttachedBy = #Local_CS004
  AttachedTo = Parent Assembly#LCS_Origin
  AttachmentOffset = pos=(0,0,17) rot=(0,0,1;0rad)
  LinkPlacement = pos=(0,0,17) rot=(0,0,1;0rad)
  LinkedObject = -> Body088
  Placement = pos=(0,0,17) rot=(0,0,1;0rad)
  SolverId = Asm4EE
  expr: Placement = LCS_Origin.Placement * AttachmentOffset * Local_CS004.Placement ^ -1
FEATURE [App::Link] ____________________  label="Эксцентрик001"
  AttachedBy = #Eccentr
  AttachedTo = Parent Assembly#crank2_axle
  AttachmentOffset = pos=(0,0,0) rot=(1,0,0;1.5708rad)
  LinkPlacement = pos=(-2.63e-14,21.25,0) rot=(0,1,0;3.14159rad)
  LinkedObject = -> Body001
  Placement = pos=(-2.63e-14,21.25,0) rot=(0,1,0;3.14159rad)
  SolverId = Asm4EE
  expr: Placement = crank2_axle.Placement * AttachmentOffset * Eccentr.Placement ^ -1
FEATURE [App::Link] ____________________001  label="Эксцентрик002"
  AttachedBy = #Eccentr
  AttachedTo = Parent Assembly#crank2_axle
  AttachmentOffset = pos=(0,0,0) rot=(1,0,0;4.71239rad)
  LinkPlacement = pos=(-2.63e-14,21.25,0) rot=(0,0,1;3.14159rad)
  LinkedObject = -> Body001
  Placement = pos=(-2.63e-14,21.25,0) rot=(0,0,1;3.14159rad)
  SolverId = Asm4EE
  expr: Placement = crank2_axle.Placement * AttachmentOffset * Eccentr.Placement ^ -1
FEATURE [App::Link] crank_gear_01  label="crank_gear_004"
  AttachedBy = #Local_CS005
  AttachedTo = Parent Assembly#crank2_axle
  AttachmentOffset = pos=(0,27,0) rot=(1,0,0;1.5708rad)
  LinkPlacement = pos=(-2.63e-14,21.25,27) rot=(0.990268,0.139173,0;3.14159rad)
  LinkedObject = -> Body087
  Placement = pos=(-2.63e-14,21.25,27) rot=(0.990268,0.139173,0;3.14159rad)
  SolverId = Asm4EE
  expr: Placement = crank2_axle.Placement * AttachmentOffset * Local_CS005.Placement ^ -1
FEATURE [PartDesign::CoordinateSystem] LCS_Origin008
  AttacherType = Attacher::AttachEngine3D
  AttachmentSupport = -> [X_Axis098]
  MapMode = 2
FEATURE [PartDesign::AdditiveCylinder] Cylinder001
  Angle = 360
  AttacherType = Attacher::AttachEngine3D
  FirstAngle = 0
  Height = 21.8
  MapMode = 1
  Radius = 1.5
  Refine = true
  SecondAngle = 0
  Suppressed = false
FEATURE [PartDesign::Body] ___________3__21_8  label="ролик 3х21.8"
  AllowCompound = false
  Group = -> [LCS_Origin008,Cylinder001]
  Origin = -> Origin099
  Tip = -> Cylinder001
FEATURE [Sketcher::SketchObject] Sketch
  ArcFitTolerance = 1e-06
  AttachmentSupport = -> [Pad002]
  FullyConstrained = true
  MakeInternals = false
  MapMode = 5
  Placement = pos=(0,-64,0) rot=(1,0,0;1.5708rad)
  sketch-geometry (1):
    g0: Circle CenterX=0 CenterY=0 CenterZ=0 NormalX=0 NormalY=0 NormalZ=1 AngleXU=0 Radius=0.5
  constraints (2):
    c: Coincident(g0,g-1)
    c: Diameter(g0) = 1
FEATURE [PartDesign::Hole] Hole001
  BaseFeature = -> Pad002
  CustomThreadClearance = 0
  Depth = 15
  DepthType = 0
  Diameter = 11
  DrillForDepth = false
  DrillPoint = 1
  DrillPointAngle = 118
  HoleCutCountersinkAngle = 90
  HoleCutCustomValues = false
  HoleCutDepth = 0
  HoleCutDiameter = 6.1
  HoleCutType = 0
  ModelThread = false
  Profile = -> Sketch
  Refine = true
  Suppressed = false
  Tapered = false
  TaperedAngle = 90
  ThreadClass = 0
  ThreadDepth = 15
  ThreadDepthType = 0
  ThreadDirection = 0
  ThreadFit = 0
  ThreadSize = 22
  ThreadType = 2
  Threaded = false
  UseCustomThreadClearance = false
FEATURE [Sketcher::SketchObject] Sketch083
  ArcFitTolerance = 1e-06
  AttachmentSupport = -> [Hole001]
  FullyConstrained = true
  MakeInternals = false
  MapMode = 5
  Placement = pos=(0,64,0) rot=(0,0.707107,0.707107;3.14159rad)
  sketch-geometry (1):
    g0: Circle CenterX=0 CenterY=0 CenterZ=0 NormalX=0 NormalY=0 NormalZ=1 AngleXU=0 Radius=0.5
  constraints (2):
    c: Coincident(g0,g-1)
    c: Diameter(g0) = 1
FEATURE [PartDesign::Hole] Hole002
  BaseFeature = -> Hole001
  CustomThreadClearance = 0
  Depth = 15
  DepthType = 0
  Diameter = 11
  DrillForDepth = false
  DrillPoint = 1
  DrillPointAngle = 118
  HoleCutCountersinkAngle = 90
  HoleCutCustomValues = false
  HoleCutDepth = 0
  HoleCutDiameter = 6.1
  HoleCutType = 0
  ModelThread = false
  Profile = -> Sketch083
  Refine = true
  Suppressed = false
  Tapered = false
  TaperedAngle = 90
  ThreadClass = 0
  ThreadDepth = 15
  ThreadDepthType = 0
  ThreadDirection = 0
  ThreadFit = 0
  ThreadSize = 22
  ThreadType = 2
  Threaded = false
  UseCustomThreadClearance = false
FEATURE [PartDesign::Body] Body002  label="Ползун_рабочий"
  AllowCompound = false
  Group = -> [Sketch007,Pad002,Shtok,Sketch,Hole001,Sketch083,Hole002]
  Origin = -> Origin003
  Tip = -> Hole002
FEATURE [App::Link] ___________________________003  label="Ползун_рабочий002"
  AttachedBy = #Shtok
  AttachedTo = Parent Assembly#Shtok_rama
  AttachmentOffset = pos=(0,0,-8.25) rot=(0,0,1;0rad)
  LinkPlacement = pos=(-1.1e-15,42.5,-8.25) rot=(0,0,1;0rad)
  LinkedObject = -> Body002
  Placement = pos=(-1.1e-15,42.5,-8.25) rot=(0,0,1;0rad)
  SolverId = Asm4EE
  expr: Placement = Shtok_rama.Placement * AttachmentOffset * Shtok.Placement ^ -1
FEATURE [App::Link] ___________________________004  label="Ползун_рабочий003"
  AttachedBy = #Shtok
  AttachedTo = Parent Assembly#shtok2
  AttachmentOffset = pos=(0,8.25,0) rot=(1,0,0;1.5708rad)
  LinkPlacement = pos=(2.69855e-05,1.09e-14,8.25) rot=(0.707107,-0.707107,0;3.14159rad)
  LinkedObject = -> Body002
  Placement = pos=(2.69855e-05,1.09e-14,8.25) rot=(0.707107,-0.707107,0;3.14159rad)
  SolverId = Asm4EE
  expr: Placement = shtok2.Placement * AttachmentOffset * Shtok.Placement ^ -1
FEATURE [PartDesign::SubtractiveCylinder] Cylinder003
  Angle = 360
  AttacherType = Attacher::AttachEngine3D
  AttachmentOffset = pos=(0,0,-12.5) rot=(0,0,1;0rad)
  AttachmentSupport = -> [Pad001]
  BaseFeature = -> Pad001
  FirstAngle = 0
  Height = 25.2
  MapMode = 2
  Placement = pos=(0,0,-12.5) rot=(0,0,1;0rad)
  Radius = 16
  Refine = true
  SecondAngle = 0
  Suppressed = false
FEATURE [PartDesign::AdditiveCylinder] Cylinder004
  Angle = 360
  AttacherType = Attacher::AttachEngine3D
  AttachmentOffset = pos=(0,0,-0.5) rot=(0,0,1;0rad)
  AttachmentSupport = -> [BaseFeature]
  BaseFeature = -> BaseFeature
  FirstAngle = 0
  Height = 11
  MapMode = 2
  Placement = pos=(0,0,-0.5) rot=(0,0,1;0rad)
  Radius = 17
  Refine = true
  SecondAngle = 0
  Suppressed = false
FEATURE [PartDesign::SubtractiveCylinder] Cylinder005
  Angle = 360
  AttacherType = Attacher::AttachEngine3D
  AttachmentOffset = pos=(0,0,-3) rot=(0,0,1;0rad)
  AttachmentSupport = -> [BaseFeature]
  BaseFeature = -> Cylinder004
  FirstAngle = 0
  Height = 15
  MapMode = 2
  Placement = pos=(0,0,-3) rot=(0,0,1;0rad)
  Radius = 12.75
  Refine = true
  SecondAngle = 0
  Suppressed = false
FEATURE [PartDesign::Body] Body087  label="crank_gear_01"
  AllowCompound = false
  BaseFeature = -> InvoluteGear006
  Group = -> [BaseFeature,Local_CS005,Cylinder004,Cylinder005]
  Origin = -> Origin090
  Tip = -> Cylinder005
FEATURE [PartDesign::AdditiveCylinder] Cylinder006
  Angle = 360
  AttacherType = Attacher::AttachEngine3D
  FirstAngle = 0
  Height = 25
  MapMode = 2
  Radius = 16
  Refine = true
  SecondAngle = 0
  Suppressed = false
FEATURE [PartDesign::SubtractiveCylinder] Cylinder007
  Angle = 360
  AttacherType = Attacher::AttachEngine3D
  AttachmentSupport = -> [XY_Plane101]
  BaseFeature = -> Cylinder006
  FirstAngle = 0
  Height = 25
  MapMode = 5
  Radius = 12.5
  Refine = true
  SecondAngle = 0
  Suppressed = false
FEATURE [PartDesign::CoordinateSystem] LCS_1
  AttacherType = Attacher::AttachEngine3D
FEATURE [PartDesign::Body] Body095  label="Подшипник 943/25"
  AllowCompound = false
  Group = -> [Cylinder006,Cylinder007,LCS_1]
  Origin = -> Origin100
  Tip = -> Cylinder007
FEATURE [App::Link] ___________________943_25  label="Подшипник 943/025 -001"
  AttachedBy = #LCS_1
  AttachedTo = Parent Assembly#LCS_Origin
  AttachmentOffset = pos=(0,0,44) rot=(0,0,1;0rad)
  LinkPlacement = pos=(0,0,44) rot=(0,0,1;0rad)
  LinkedObject = -> Body095
  Placement = pos=(0,0,44) rot=(0,0,1;0rad)
  SolverId = Asm4EE
  expr: Placement = LCS_Origin.Placement * AttachmentOffset * LCS_1.Placement ^ -1
FEATURE [App::Link] ___________________943_026  label="Подшипник 943/025 -002"
  AttachedBy = #LCS_1
  AttachedTo = Parent Assembly#LCS_Origin
  AttachmentOffset = pos=(0,0,-69) rot=(0,0,1;0rad)
  LinkPlacement = pos=(0,0,-69) rot=(0,0,1;0rad)
  LinkedObject = -> Body095
  Placement = pos=(0,0,-69) rot=(0,0,1;0rad)
  SolverId = Asm4EE
  expr: Placement = LCS_Origin.Placement * AttachmentOffset * LCS_1.Placement ^ -1
FEATURE [PartDesign::Fillet] Fillet
  Base = -> Clone007 [Edge52,Edge1]
  BaseFeature = -> Clone007
  Radius = 0.25
  Refine = true
  SupportTransform = false
  Suppressed = false
  UseAllEdges = false
FEATURE [PartDesign::Body] Body057  label="Колевал (секция)"
  AllowCompound = false
  Group = -> [Clone007,Crank_shaft,Fillet]
  Origin = -> Origin058
  Tip = -> Fillet
FEATURE [PartDesign::Fillet] Fillet001
  Base = -> Clone [Edge12]
  BaseFeature = -> Clone
  Radius = 0.25
  Refine = true
  SupportTransform = false
  Suppressed = false
  UseAllEdges = false
FEATURE [PartDesign::Body] Body091  label="Шейка_и_щека_задняя_cl"
  AllowCompound = false
  Group = -> [Clone,LCS_2,Fillet001]
  Origin = -> Origin094
  Tip = -> Fillet001
FEATURE [PartDesign::SubtractiveCylinder] Cylinder008
  Angle = 360
  AttacherType = Attacher::AttachEngine3D
  AttachmentOffset = pos=(23,0,-13) rot=(0,0,1;0rad)
  AttachmentSupport = -> [XY_Plane002]
  BaseFeature = -> Cylinder003
  FirstAngle = 0
  Height = 25
  MapMode = 5
  Placement = pos=(23,0,-13) rot=(0,0,1;0rad)
  Radius = 4
  Refine = true
  SecondAngle = 0
  Suppressed = false
FEATURE [PartDesign::SubtractiveCylinder] Cylinder009
  Angle = 360
  AttacherType = Attacher::AttachEngine3D
  AttachmentOffset = pos=(-23,0,-13) rot=(0,0,1;0rad)
  AttachmentSupport = -> [XY_Plane002]
  BaseFeature = -> Cylinder008
  FirstAngle = 0
  Height = 25
  MapMode = 5
  Placement = pos=(-23,0,-13) rot=(0,0,1;0rad)
  Radius = 4
  Refine = true
  SecondAngle = 0
  Suppressed = false
FEATURE [App::Link] ___________________943_027  label="Подшипник 943/025 -003"
  AttachedBy = #LCS_1
  AttachedTo = Parent Assembly#crank2_axle
  AttachmentOffset = pos=(0,12.5,0) rot=(1,0,0;1.5708rad)
  LinkPlacement = pos=(-2.63e-14,21.25,12.5) rot=(1,0,0;3.14159rad)
  LinkedObject = -> Body095
  Placement = pos=(-2.63e-14,21.25,12.5) rot=(1,0,0;3.14159rad)
  SolverId = Asm4EE
  expr: Placement = crank2_axle.Placement * AttachmentOffset * LCS_1.Placement ^ -1
FEATURE [PartDesign::PolarPattern] PolarPattern
  Angle = 360
  Axis = -> Z_Axis097
  BaseFeature = -> Cylinder
  Mode = 0
  Occurrences = 87
  Offset = 120
  Originals = -> [Cylinder]
  Placement = pos=(41.5,0,6.9) rot=(0,0,1;0rad)
  Refine = true
  Suppressed = false
  TransformMode = 1
FEATURE [PartDesign::CoordinateSystem] LCS_4
  AttacherType = Attacher::AttachEngine3D
  AttachmentSupport = -> [Z_Axis097]
  MapMode = 7
  Placement = pos=(0,0,0) rot=(0,1,0;3.14159rad)
FEATURE [PartDesign::Body] Body094  label="ролик_3*13,8  - 87шт."
  AllowCompound = false
  Group = -> [Cylinder,PolarPattern,LCS_4]
  Origin = -> Origin098
  Tip = -> PolarPattern
FEATURE [App::Link] ___________3_13_8____171_____  label="ролик_3*13,8  - 87шт. 002"
  AttachedBy = #LCS_4
  AttachedTo = Parent Assembly#Shtok_rama
  AttachmentOffset = pos=(0,0,5.55) rot=(0,0,1;0rad)
  LinkPlacement = pos=(-2.5e-15,42.5,5.55) rot=(0,-1,0;3.14159rad)
  LinkedObject = -> Body094
  Placement = pos=(-2.5e-15,42.5,5.55) rot=(0,-1,0;3.14159rad)
  SolverId = Asm4EE
  expr: Placement = Shtok_rama.Placement * AttachmentOffset * LCS_4.Placement ^ -1
FEATURE [App::Link] ___________3_13_8____87_____  label="ролик_3*13,8  - 87шт. 001"
  AttachedBy = #LCS_4
  AttachedTo = Parent Assembly#shtok2
  AttachmentOffset = pos=(0,-5.55,0) rot=(1,0,0;1.5708rad)
  LinkPlacement = pos=(-4.66e-14,1.23e-14,-5.55) rot=(0,0,-1;4.71239rad)
  LinkedObject = -> Body094
  Placement = pos=(-4.66e-14,1.23e-14,-5.55) rot=(0,0,-1;4.71239rad)
  SolverId = Asm4EE
  expr: Placement = shtok2.Placement * AttachmentOffset * LCS_4.Placement ^ -1
FEATURE [Sketcher::SketchObject] Sketch084
  ArcFitTolerance = 1e-06
  AttachmentSupport = -> [XY_Plane002]
  FullyConstrained = true
  MakeInternals = false
  MapMode = 5
  expr: Constraints[2] = <<Dim_table>>.crank_len
  expr: Constraints[3] = <<Dim_table>>.ecc_dia
  expr: Constraints[4] = <<Dim_table>>.ecc_dia * 1.2
  sketch-geometry (2):
    g0: Circle CenterX=0 CenterY=-21.25 CenterZ=0 NormalX=0 NormalY=0 NormalZ=1 AngleXU=0 Radius=40
    g1: Circle CenterX=0 CenterY=-21.25 CenterZ=0 NormalX=0 NormalY=0 NormalZ=1 AngleXU=0 Radius=48
  constraints (5):
    c: PointOnObject(g0,g-2)
    c: Coincident(g1,g0)
    c: Distance(g0,g-1) = 21.25
    c: Diameter(g0) = 80
    c: Diameter(g1) = 96
FEATURE [PartDesign::Pocket] Pocket
  BaseFeature = -> Cylinder009
  Direction = (0,0,-1)
  Length = 15.25
  Length2 = -1.25
  Placement = pos=(-23,0,-13) rot=(0,0,1;0rad)
  Profile = -> Sketch084
  ReferenceAxis = -> Sketch084 [N_Axis]
  Refine = true
  Suppressed = false
  Type = 4
FEATURE [PartDesign::Body] Body001  label="Эксцентрик"
  AllowCompound = false
  Group = -> [Sketch005,Pad001,Eccentr,Cylinder003,Cylinder008,Cylinder009,Sketch084,Pocket]
  Origin = -> Origin002
  Tip = -> Pocket
FEATURE [App::Link] _____________________  label="Шток_поршня001"
  AttachedBy = #Pin
  AttachedTo = Parent Assembly#Shtok_rama
  AttachmentOffset = pos=(0,0,-8.25) rot=(0,0,1;0rad)
  LinkPlacement = pos=(-2.5e-15,42.5,-8.25) rot=(0,0,1;0rad)
  LinkedObject = -> Body
  Placement = pos=(-2.5e-15,42.5,-8.25) rot=(0,0,1;0rad)
  SolverId = Asm4EE
  expr: Placement = Shtok_rama.Placement * AttachmentOffset * Pin.Placement ^ -1
FEATURE [App::Link] _____________________001  label="Шток_поршня002"
  AttachedBy = #Pin
  AttachedTo = Parent Assembly#Shtok_rama
  AttachmentOffset = pos=(0,0,-8.25) rot=(0,0,1;3.14159rad)
  LinkPlacement = pos=(-2.5e-15,42.5,-8.25) rot=(0,0,1;3.14159rad)
  LinkedObject = -> Body
  Placement = pos=(-2.5e-15,42.5,-8.25) rot=(0,0,1;3.14159rad)
  SolverId = Asm4EE
  expr: Placement = Shtok_rama.Placement * AttachmentOffset * Pin.Placement ^ -1
FEATURE [App::Link] _____________________002  label="Шток_поршня003"
  AttachedBy = #Pin
  AttachedTo = Parent Assembly#shtok2
  AttachmentOffset = pos=(0,8.25,0) rot=(1,0,0;1.5708rad)
  LinkPlacement = pos=(-4.66e-14,1.23e-14,8.25) rot=(0.707107,-0.707107,0;3.14159rad)
  LinkedObject = -> Body
  Placement = pos=(-4.66e-14,1.23e-14,8.25) rot=(0.707107,-0.707107,0;3.14159rad)
  SolverId = Asm4EE
  expr: Placement = shtok2.Placement * AttachmentOffset * Pin.Placement ^ -1
FEATURE [App::Link] _____________________003  label="Шток_поршня004"
  AttachedBy = #Pin
  AttachedTo = Parent Assembly#shtok2
  AttachmentOffset = pos=(0,8.25,0) rot=(0,-0.707107,0.707107;3.14159rad)
  LinkPlacement = pos=(-4.66e-14,1.23e-14,8.25) rot=(-0.707107,-0.707107,0;3.14159rad)
  LinkedObject = -> Body
  Placement = pos=(-4.66e-14,1.23e-14,8.25) rot=(-0.707107,-0.707107,0;3.14159rad)
  SolverId = Asm4EE
  expr: Placement = shtok2.Placement * AttachmentOffset * Pin.Placement ^ -1
FEATURE [App::Part] Assembly  label="Assembly_total"
  AssemblyType = Part::Link
  Group = -> [LCS_Origin,Constraints,Variables,Configurations,Main,LCS_6,crank2_axle,Shtok_rama,_____________________________,____________________________________cl,_________________________,___________________________002,_________________________________________________________,____________________________________________1,shtok2,crank_gear_002,crank_int_gear_01,crank_int_gear_002,____________________,+13 more]
  Origin = -> Origin
  Type = Assembly
FEATURE [Sketcher::SketchObject] Sketch085
  ArcFitTolerance = 1e-06
  AttachmentOffset = pos=(0,0,-66) rot=(0,0,1;0rad)
  AttachmentSupport = -> [XZ_Plane001]
  ExternalGeometry = -> [Pad026]
  FullyConstrained = true
  MakeInternals = false
  MapMode = 5
  Placement = pos=(0,66,-1.47e-14) rot=(1,0,0;1.5708rad)
  sketch-geometry (7):
    g0: ArcOfCircle CenterX=0 CenterY=0 CenterZ=0 NormalX=0 NormalY=0 NormalZ=1 AngleXU=0 Radius=7.5 StartAngle=2.41186 EndAngle=3.87132
    g1: LineSegment StartX=-5.59017 StartY=5 StartZ=0 EndX=5.59017 EndY=5 EndZ=0
    g2: LineSegment StartX=-5.59017 StartY=-5 StartZ=0 EndX=5.59017 EndY=-5 EndZ=0
    g3: ArcOfCircle CenterX=0 CenterY=0 CenterZ=0 NormalX=0 NormalY=0 NormalZ=1 AngleXU=0 Radius=7.5 StartAngle=5.55346 EndAngle=7.01291
    g4: LineSegment [constr] StartX=0 StartY=5 StartZ=0 EndX=0 EndY=-5 EndZ=0
    g5: LineSegment [constr] StartX=5.59017 StartY=5 StartZ=0 EndX=5.59017 EndY=-5 EndZ=0
    g6: Circle CenterX=0 CenterY=0 CenterZ=0 NormalX=0 NormalY=0 NormalZ=1 AngleXU=0 Radius=2
  constraints (20):
    c: Coincident(g0,g-1)
    c: Horizontal(g1)
    c: Horizontal(g2)
    c: Coincident(g0,g1)
    c: Coincident(g1,g3)
    c: Equal(g0,g3)
    c: Coincident(g0,g2)
    c: Coincident(g0,g3)
    c: Equal(g3,g-3)
    c: PointOnObject(g4,g-5)
    c: PointOnObject(g4,g-5)
    c: Coincident(g5,g1)
    c: Coincident(g5,g2)
    c: Vertical(g5)
    c: Equal(g4,g5)
    c: PointOnObject(g4,g-2)
    c: Coincident(g6,g0)
    c: Equal(g6,g-4)
    c: Coincident(g2,g3)
    c: Vertical(g4)
FEATURE [PartDesign::Pad] Pad046
  BaseFeature = -> Pad026
  Direction = (0,-1,2e-16)
  Length = 2
  Length2 = 10
  Placement = pos=(0,0,0) rot=(1,0,0;1.5708rad)
  Profile = -> Sketch085
  ReferenceAxis = -> Sketch085 [N_Axis]
  Refine = true
  Suppressed = false
  Type = 0
FEATURE [PartDesign::Body] Body  label="Шток_поршня"
  AllowCompound = false
  Group = -> [Pin,Sketch053,Pad,Sketch055,Pad026,Sketch085,Pad046]
  Origin = -> Origin001
  Tip = -> Pad046
FEATURE [App::DocumentObjectGroup] Parts
  Group = -> [Body002,Body003,Body004,Body005,Body057,Body061,Body063,Body064,Body066,Body072,Body071,XY_Plane077,Body077,Body001,Body,___________________________,Extrude,InvoluteGear006,InternalInvoluteGear001,Body087,Body088,Body076,Cut,Body091,Body_2,Sketch077,Extrude001,Body092,Body094,___________3__21_8,Body095]
